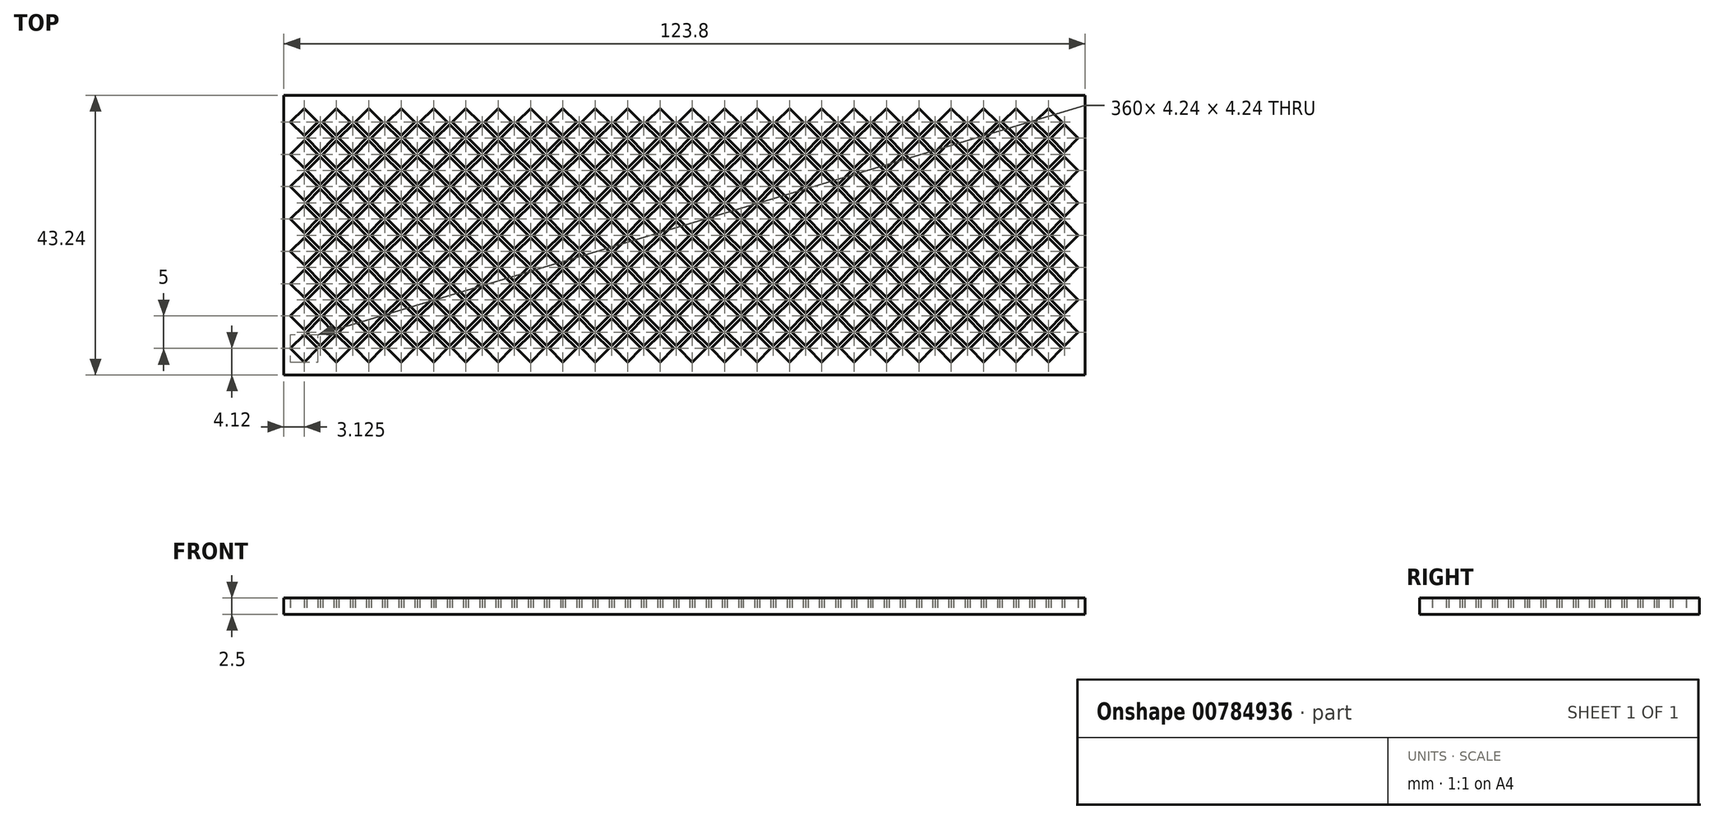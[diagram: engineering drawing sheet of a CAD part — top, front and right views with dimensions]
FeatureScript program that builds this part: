
annotation { "Feature Type Name" : "Feature", "Feature Type Description" : "" }
export const myFeature = defineFeature(function(context is Context, id is Id, definition is map)
    precondition{}
    {
        {
            var Q0;
            Q0=qCreatedBy(makeId("Top.planeOp"),FACE);
            var sketch = newSketch(context, id + "F0", { "sketchPlane" : qUnion([Q0])});
            skLineSegment(sketch, "E0.bottom", {"start": v(61.9, 21.62) * mm, "end": v(-61.9, 21.62) * mm});
            skLineSegment(sketch, "E0.top", {"start": v(61.9, -21.62) * mm, "end": v(-61.9, -21.62) * mm});
            skLineSegment(sketch, "E0.left", {"start": v(61.9, 21.62) * mm, "end": v(61.9, -21.62) * mm});
            skLineSegment(sketch, "E0.right", {"start": v(-61.9, 21.62) * mm, "end": v(-61.9, -21.62) * mm});
            skPoint(sketch, "E0.middle", {"position": v(0, 0) * mm});
            skLineSegment(sketch, "E1.bottom", {"start": v(-60.9, -17.5) * mm, "end": v(-58.77, -15.38) * mm});
            skLineSegment(sketch, "E1.top", {"start": v(-58.77, -19.62) * mm, "end": v(-56.65, -17.5) * mm});
            skLineSegment(sketch, "E1.left", {"start": v(-60.9, -17.5) * mm, "end": v(-58.77, -19.62) * mm});
            skLineSegment(sketch, "E1.right", {"start": v(-58.77, -15.38) * mm, "end": v(-56.65, -17.5) * mm});
            skLineSegment(sketch, "E2.0.1.0", {"start": v(-60.9, -12.5) * mm, "end": v(-58.77, -10.38) * mm});
            skLineSegment(sketch, "E2.0.1.1", {"start": v(-58.77, -14.62) * mm, "end": v(-56.65, -12.5) * mm});
            skLineSegment(sketch, "E2.0.1.2", {"start": v(-60.9, -12.5) * mm, "end": v(-58.77, -14.62) * mm});
            skLineSegment(sketch, "E2.0.1.3", {"start": v(-58.77, -10.38) * mm, "end": v(-56.65, -12.5) * mm});
            skLineSegment(sketch, "E2.0.2.0", {"start": v(-60.9, -7.5) * mm, "end": v(-58.77, -5.38) * mm});
            skLineSegment(sketch, "E2.0.2.1", {"start": v(-58.77, -9.62) * mm, "end": v(-56.65, -7.5) * mm});
            skLineSegment(sketch, "E2.0.2.2", {"start": v(-60.9, -7.5) * mm, "end": v(-58.77, -9.62) * mm});
            skLineSegment(sketch, "E2.0.2.3", {"start": v(-58.77, -5.38) * mm, "end": v(-56.65, -7.5) * mm});
            skLineSegment(sketch, "E2.0.3.0", {"start": v(-60.9, -2.5) * mm, "end": v(-58.77, -0.38) * mm});
            skLineSegment(sketch, "E2.0.3.1", {"start": v(-58.77, -4.62) * mm, "end": v(-56.65, -2.5) * mm});
            skLineSegment(sketch, "E2.0.3.2", {"start": v(-60.9, -2.5) * mm, "end": v(-58.77, -4.62) * mm});
            skLineSegment(sketch, "E2.0.3.3", {"start": v(-58.77, -0.38) * mm, "end": v(-56.65, -2.5) * mm});
            skLineSegment(sketch, "E2.0.4.0", {"start": v(-60.9, 2.5) * mm, "end": v(-58.77, 4.62) * mm});
            skLineSegment(sketch, "E2.0.4.1", {"start": v(-58.77, 0.38) * mm, "end": v(-56.65, 2.5) * mm});
            skLineSegment(sketch, "E2.0.4.2", {"start": v(-60.9, 2.5) * mm, "end": v(-58.77, 0.38) * mm});
            skLineSegment(sketch, "E2.0.4.3", {"start": v(-58.77, 4.62) * mm, "end": v(-56.65, 2.5) * mm});
            skLineSegment(sketch, "E2.0.5.0", {"start": v(-60.9, 7.5) * mm, "end": v(-58.77, 9.62) * mm});
            skLineSegment(sketch, "E2.0.5.1", {"start": v(-58.77, 5.38) * mm, "end": v(-56.65, 7.5) * mm});
            skLineSegment(sketch, "E2.0.5.2", {"start": v(-60.9, 7.5) * mm, "end": v(-58.77, 5.38) * mm});
            skLineSegment(sketch, "E2.0.5.3", {"start": v(-58.77, 9.62) * mm, "end": v(-56.65, 7.5) * mm});
            skLineSegment(sketch, "E2.0.6.0", {"start": v(-60.9, 12.5) * mm, "end": v(-58.77, 14.62) * mm});
            skLineSegment(sketch, "E2.0.6.1", {"start": v(-58.77, 10.38) * mm, "end": v(-56.65, 12.5) * mm});
            skLineSegment(sketch, "E2.0.6.2", {"start": v(-60.9, 12.5) * mm, "end": v(-58.77, 10.38) * mm});
            skLineSegment(sketch, "E2.0.6.3", {"start": v(-58.77, 14.62) * mm, "end": v(-56.65, 12.5) * mm});
            skLineSegment(sketch, "E2.0.7.0", {"start": v(-60.9, 17.5) * mm, "end": v(-58.77, 19.62) * mm});
            skLineSegment(sketch, "E2.0.7.1", {"start": v(-58.77, 15.38) * mm, "end": v(-56.65, 17.5) * mm});
            skLineSegment(sketch, "E2.0.7.2", {"start": v(-60.9, 17.5) * mm, "end": v(-58.77, 15.38) * mm});
            skLineSegment(sketch, "E2.0.7.3", {"start": v(-58.77, 19.62) * mm, "end": v(-56.65, 17.5) * mm});
            skLineSegment(sketch, "E2.1.0.0", {"start": v(-55.9, -17.5) * mm, "end": v(-53.77, -15.38) * mm});
            skLineSegment(sketch, "E2.1.0.1", {"start": v(-53.77, -19.62) * mm, "end": v(-51.65, -17.5) * mm});
            skLineSegment(sketch, "E2.1.0.2", {"start": v(-55.9, -17.5) * mm, "end": v(-53.77, -19.62) * mm});
            skLineSegment(sketch, "E2.1.0.3", {"start": v(-53.77, -15.38) * mm, "end": v(-51.65, -17.5) * mm});
            skLineSegment(sketch, "E2.1.1.0", {"start": v(-55.9, -12.5) * mm, "end": v(-53.77, -10.38) * mm});
            skLineSegment(sketch, "E2.1.1.1", {"start": v(-53.77, -14.62) * mm, "end": v(-51.65, -12.5) * mm});
            skLineSegment(sketch, "E2.1.1.2", {"start": v(-55.9, -12.5) * mm, "end": v(-53.77, -14.62) * mm});
            skLineSegment(sketch, "E2.1.1.3", {"start": v(-53.77, -10.38) * mm, "end": v(-51.65, -12.5) * mm});
            skLineSegment(sketch, "E2.1.2.0", {"start": v(-55.9, -7.5) * mm, "end": v(-53.77, -5.38) * mm});
            skLineSegment(sketch, "E2.1.2.1", {"start": v(-53.77, -9.62) * mm, "end": v(-51.65, -7.5) * mm});
            skLineSegment(sketch, "E2.1.2.2", {"start": v(-55.9, -7.5) * mm, "end": v(-53.77, -9.62) * mm});
            skLineSegment(sketch, "E2.1.2.3", {"start": v(-53.77, -5.38) * mm, "end": v(-51.65, -7.5) * mm});
            skLineSegment(sketch, "E2.1.3.0", {"start": v(-55.9, -2.5) * mm, "end": v(-53.77, -0.38) * mm});
            skLineSegment(sketch, "E2.1.3.1", {"start": v(-53.77, -4.62) * mm, "end": v(-51.65, -2.5) * mm});
            skLineSegment(sketch, "E2.1.3.2", {"start": v(-55.9, -2.5) * mm, "end": v(-53.77, -4.62) * mm});
            skLineSegment(sketch, "E2.1.3.3", {"start": v(-53.77, -0.38) * mm, "end": v(-51.65, -2.5) * mm});
            skLineSegment(sketch, "E2.1.4.0", {"start": v(-55.9, 2.5) * mm, "end": v(-53.77, 4.62) * mm});
            skLineSegment(sketch, "E2.1.4.1", {"start": v(-53.77, 0.38) * mm, "end": v(-51.65, 2.5) * mm});
            skLineSegment(sketch, "E2.1.4.2", {"start": v(-55.9, 2.5) * mm, "end": v(-53.77, 0.38) * mm});
            skLineSegment(sketch, "E2.1.4.3", {"start": v(-53.77, 4.62) * mm, "end": v(-51.65, 2.5) * mm});
            skLineSegment(sketch, "E2.1.5.0", {"start": v(-55.9, 7.5) * mm, "end": v(-53.77, 9.62) * mm});
            skLineSegment(sketch, "E2.1.5.1", {"start": v(-53.77, 5.38) * mm, "end": v(-51.65, 7.5) * mm});
            skLineSegment(sketch, "E2.1.5.2", {"start": v(-55.9, 7.5) * mm, "end": v(-53.77, 5.38) * mm});
            skLineSegment(sketch, "E2.1.5.3", {"start": v(-53.77, 9.62) * mm, "end": v(-51.65, 7.5) * mm});
            skLineSegment(sketch, "E2.1.6.0", {"start": v(-55.9, 12.5) * mm, "end": v(-53.77, 14.62) * mm});
            skLineSegment(sketch, "E2.1.6.1", {"start": v(-53.77, 10.38) * mm, "end": v(-51.65, 12.5) * mm});
            skLineSegment(sketch, "E2.1.6.2", {"start": v(-55.9, 12.5) * mm, "end": v(-53.77, 10.38) * mm});
            skLineSegment(sketch, "E2.1.6.3", {"start": v(-53.77, 14.62) * mm, "end": v(-51.65, 12.5) * mm});
            skLineSegment(sketch, "E2.1.7.0", {"start": v(-55.9, 17.5) * mm, "end": v(-53.77, 19.62) * mm});
            skLineSegment(sketch, "E2.1.7.1", {"start": v(-53.77, 15.38) * mm, "end": v(-51.65, 17.5) * mm});
            skLineSegment(sketch, "E2.1.7.2", {"start": v(-55.9, 17.5) * mm, "end": v(-53.77, 15.38) * mm});
            skLineSegment(sketch, "E2.1.7.3", {"start": v(-53.77, 19.62) * mm, "end": v(-51.65, 17.5) * mm});
            skLineSegment(sketch, "E2.2.0.0", {"start": v(-50.9, -17.5) * mm, "end": v(-48.77, -15.38) * mm});
            skLineSegment(sketch, "E2.2.0.1", {"start": v(-48.77, -19.62) * mm, "end": v(-46.65, -17.5) * mm});
            skLineSegment(sketch, "E2.2.0.2", {"start": v(-50.9, -17.5) * mm, "end": v(-48.77, -19.62) * mm});
            skLineSegment(sketch, "E2.2.0.3", {"start": v(-48.77, -15.38) * mm, "end": v(-46.65, -17.5) * mm});
            skLineSegment(sketch, "E2.2.1.0", {"start": v(-50.9, -12.5) * mm, "end": v(-48.77, -10.38) * mm});
            skLineSegment(sketch, "E2.2.1.1", {"start": v(-48.77, -14.62) * mm, "end": v(-46.65, -12.5) * mm});
            skLineSegment(sketch, "E2.2.1.2", {"start": v(-50.9, -12.5) * mm, "end": v(-48.77, -14.62) * mm});
            skLineSegment(sketch, "E2.2.1.3", {"start": v(-48.77, -10.38) * mm, "end": v(-46.65, -12.5) * mm});
            skLineSegment(sketch, "E2.2.2.0", {"start": v(-50.9, -7.5) * mm, "end": v(-48.77, -5.38) * mm});
            skLineSegment(sketch, "E2.2.2.1", {"start": v(-48.77, -9.62) * mm, "end": v(-46.65, -7.5) * mm});
            skLineSegment(sketch, "E2.2.2.2", {"start": v(-50.9, -7.5) * mm, "end": v(-48.77, -9.62) * mm});
            skLineSegment(sketch, "E2.2.2.3", {"start": v(-48.77, -5.38) * mm, "end": v(-46.65, -7.5) * mm});
            skLineSegment(sketch, "E2.2.3.0", {"start": v(-50.9, -2.5) * mm, "end": v(-48.77, -0.38) * mm});
            skLineSegment(sketch, "E2.2.3.1", {"start": v(-48.77, -4.62) * mm, "end": v(-46.65, -2.5) * mm});
            skLineSegment(sketch, "E2.2.3.2", {"start": v(-50.9, -2.5) * mm, "end": v(-48.77, -4.62) * mm});
            skLineSegment(sketch, "E2.2.3.3", {"start": v(-48.77, -0.38) * mm, "end": v(-46.65, -2.5) * mm});
            skLineSegment(sketch, "E2.2.4.0", {"start": v(-50.9, 2.5) * mm, "end": v(-48.77, 4.62) * mm});
            skLineSegment(sketch, "E2.2.4.1", {"start": v(-48.77, 0.38) * mm, "end": v(-46.65, 2.5) * mm});
            skLineSegment(sketch, "E2.2.4.2", {"start": v(-50.9, 2.5) * mm, "end": v(-48.77, 0.38) * mm});
            skLineSegment(sketch, "E2.2.4.3", {"start": v(-48.77, 4.62) * mm, "end": v(-46.65, 2.5) * mm});
            skLineSegment(sketch, "E2.2.5.0", {"start": v(-50.9, 7.5) * mm, "end": v(-48.77, 9.62) * mm});
            skLineSegment(sketch, "E2.2.5.1", {"start": v(-48.77, 5.38) * mm, "end": v(-46.65, 7.5) * mm});
            skLineSegment(sketch, "E2.2.5.2", {"start": v(-50.9, 7.5) * mm, "end": v(-48.77, 5.38) * mm});
            skLineSegment(sketch, "E2.2.5.3", {"start": v(-48.77, 9.62) * mm, "end": v(-46.65, 7.5) * mm});
            skLineSegment(sketch, "E2.2.6.0", {"start": v(-50.9, 12.5) * mm, "end": v(-48.77, 14.62) * mm});
            skLineSegment(sketch, "E2.2.6.1", {"start": v(-48.77, 10.38) * mm, "end": v(-46.65, 12.5) * mm});
            skLineSegment(sketch, "E2.2.6.2", {"start": v(-50.9, 12.5) * mm, "end": v(-48.77, 10.38) * mm});
            skLineSegment(sketch, "E2.2.6.3", {"start": v(-48.77, 14.62) * mm, "end": v(-46.65, 12.5) * mm});
            skLineSegment(sketch, "E2.2.7.0", {"start": v(-50.9, 17.5) * mm, "end": v(-48.77, 19.62) * mm});
            skLineSegment(sketch, "E2.2.7.1", {"start": v(-48.77, 15.38) * mm, "end": v(-46.65, 17.5) * mm});
            skLineSegment(sketch, "E2.2.7.2", {"start": v(-50.9, 17.5) * mm, "end": v(-48.77, 15.38) * mm});
            skLineSegment(sketch, "E2.2.7.3", {"start": v(-48.77, 19.62) * mm, "end": v(-46.65, 17.5) * mm});
            skLineSegment(sketch, "E2.3.0.0", {"start": v(-45.9, -17.5) * mm, "end": v(-43.77, -15.38) * mm});
            skLineSegment(sketch, "E2.3.0.1", {"start": v(-43.77, -19.62) * mm, "end": v(-41.65, -17.5) * mm});
            skLineSegment(sketch, "E2.3.0.2", {"start": v(-45.9, -17.5) * mm, "end": v(-43.77, -19.62) * mm});
            skLineSegment(sketch, "E2.3.0.3", {"start": v(-43.77, -15.38) * mm, "end": v(-41.65, -17.5) * mm});
            skLineSegment(sketch, "E2.3.1.0", {"start": v(-45.9, -12.5) * mm, "end": v(-43.77, -10.38) * mm});
            skLineSegment(sketch, "E2.3.1.1", {"start": v(-43.77, -14.62) * mm, "end": v(-41.65, -12.5) * mm});
            skLineSegment(sketch, "E2.3.1.2", {"start": v(-45.9, -12.5) * mm, "end": v(-43.77, -14.62) * mm});
            skLineSegment(sketch, "E2.3.1.3", {"start": v(-43.77, -10.38) * mm, "end": v(-41.65, -12.5) * mm});
            skLineSegment(sketch, "E2.3.2.0", {"start": v(-45.9, -7.5) * mm, "end": v(-43.77, -5.38) * mm});
            skLineSegment(sketch, "E2.3.2.1", {"start": v(-43.77, -9.62) * mm, "end": v(-41.65, -7.5) * mm});
            skLineSegment(sketch, "E2.3.2.2", {"start": v(-45.9, -7.5) * mm, "end": v(-43.77, -9.62) * mm});
            skLineSegment(sketch, "E2.3.2.3", {"start": v(-43.77, -5.38) * mm, "end": v(-41.65, -7.5) * mm});
            skLineSegment(sketch, "E2.3.3.0", {"start": v(-45.9, -2.5) * mm, "end": v(-43.77, -0.38) * mm});
            skLineSegment(sketch, "E2.3.3.1", {"start": v(-43.77, -4.62) * mm, "end": v(-41.65, -2.5) * mm});
            skLineSegment(sketch, "E2.3.3.2", {"start": v(-45.9, -2.5) * mm, "end": v(-43.77, -4.62) * mm});
            skLineSegment(sketch, "E2.3.3.3", {"start": v(-43.77, -0.38) * mm, "end": v(-41.65, -2.5) * mm});
            skLineSegment(sketch, "E2.3.4.0", {"start": v(-45.9, 2.5) * mm, "end": v(-43.77, 4.62) * mm});
            skLineSegment(sketch, "E2.3.4.1", {"start": v(-43.77, 0.38) * mm, "end": v(-41.65, 2.5) * mm});
            skLineSegment(sketch, "E2.3.4.2", {"start": v(-45.9, 2.5) * mm, "end": v(-43.77, 0.38) * mm});
            skLineSegment(sketch, "E2.3.4.3", {"start": v(-43.77, 4.62) * mm, "end": v(-41.65, 2.5) * mm});
            skLineSegment(sketch, "E2.3.5.0", {"start": v(-45.9, 7.5) * mm, "end": v(-43.77, 9.62) * mm});
            skLineSegment(sketch, "E2.3.5.1", {"start": v(-43.77, 5.38) * mm, "end": v(-41.65, 7.5) * mm});
            skLineSegment(sketch, "E2.3.5.2", {"start": v(-45.9, 7.5) * mm, "end": v(-43.77, 5.38) * mm});
            skLineSegment(sketch, "E2.3.5.3", {"start": v(-43.77, 9.62) * mm, "end": v(-41.65, 7.5) * mm});
            skLineSegment(sketch, "E2.3.6.0", {"start": v(-45.9, 12.5) * mm, "end": v(-43.77, 14.62) * mm});
            skLineSegment(sketch, "E2.3.6.1", {"start": v(-43.77, 10.38) * mm, "end": v(-41.65, 12.5) * mm});
            skLineSegment(sketch, "E2.3.6.2", {"start": v(-45.9, 12.5) * mm, "end": v(-43.77, 10.38) * mm});
            skLineSegment(sketch, "E2.3.6.3", {"start": v(-43.77, 14.62) * mm, "end": v(-41.65, 12.5) * mm});
            skLineSegment(sketch, "E2.3.7.0", {"start": v(-45.9, 17.5) * mm, "end": v(-43.77, 19.62) * mm});
            skLineSegment(sketch, "E2.3.7.1", {"start": v(-43.77, 15.38) * mm, "end": v(-41.65, 17.5) * mm});
            skLineSegment(sketch, "E2.3.7.2", {"start": v(-45.9, 17.5) * mm, "end": v(-43.77, 15.38) * mm});
            skLineSegment(sketch, "E2.3.7.3", {"start": v(-43.77, 19.62) * mm, "end": v(-41.65, 17.5) * mm});
            skLineSegment(sketch, "E2.4.0.0", {"start": v(-40.9, -17.5) * mm, "end": v(-38.77, -15.38) * mm});
            skLineSegment(sketch, "E2.4.0.1", {"start": v(-38.77, -19.62) * mm, "end": v(-36.65, -17.5) * mm});
            skLineSegment(sketch, "E2.4.0.2", {"start": v(-40.9, -17.5) * mm, "end": v(-38.77, -19.62) * mm});
            skLineSegment(sketch, "E2.4.0.3", {"start": v(-38.77, -15.38) * mm, "end": v(-36.65, -17.5) * mm});
            skLineSegment(sketch, "E2.4.1.0", {"start": v(-40.9, -12.5) * mm, "end": v(-38.77, -10.38) * mm});
            skLineSegment(sketch, "E2.4.1.1", {"start": v(-38.77, -14.62) * mm, "end": v(-36.65, -12.5) * mm});
            skLineSegment(sketch, "E2.4.1.2", {"start": v(-40.9, -12.5) * mm, "end": v(-38.77, -14.62) * mm});
            skLineSegment(sketch, "E2.4.1.3", {"start": v(-38.77, -10.38) * mm, "end": v(-36.65, -12.5) * mm});
            skLineSegment(sketch, "E2.4.2.0", {"start": v(-40.9, -7.5) * mm, "end": v(-38.77, -5.38) * mm});
            skLineSegment(sketch, "E2.4.2.1", {"start": v(-38.77, -9.62) * mm, "end": v(-36.65, -7.5) * mm});
            skLineSegment(sketch, "E2.4.2.2", {"start": v(-40.9, -7.5) * mm, "end": v(-38.77, -9.62) * mm});
            skLineSegment(sketch, "E2.4.2.3", {"start": v(-38.77, -5.38) * mm, "end": v(-36.65, -7.5) * mm});
            skLineSegment(sketch, "E2.4.3.0", {"start": v(-40.9, -2.5) * mm, "end": v(-38.77, -0.38) * mm});
            skLineSegment(sketch, "E2.4.3.1", {"start": v(-38.77, -4.62) * mm, "end": v(-36.65, -2.5) * mm});
            skLineSegment(sketch, "E2.4.3.2", {"start": v(-40.9, -2.5) * mm, "end": v(-38.77, -4.62) * mm});
            skLineSegment(sketch, "E2.4.3.3", {"start": v(-38.77, -0.38) * mm, "end": v(-36.65, -2.5) * mm});
            skLineSegment(sketch, "E2.4.4.0", {"start": v(-40.9, 2.5) * mm, "end": v(-38.77, 4.62) * mm});
            skLineSegment(sketch, "E2.4.4.1", {"start": v(-38.77, 0.38) * mm, "end": v(-36.65, 2.5) * mm});
            skLineSegment(sketch, "E2.4.4.2", {"start": v(-40.9, 2.5) * mm, "end": v(-38.77, 0.38) * mm});
            skLineSegment(sketch, "E2.4.4.3", {"start": v(-38.77, 4.62) * mm, "end": v(-36.65, 2.5) * mm});
            skLineSegment(sketch, "E2.4.5.0", {"start": v(-40.9, 7.5) * mm, "end": v(-38.77, 9.62) * mm});
            skLineSegment(sketch, "E2.4.5.1", {"start": v(-38.77, 5.38) * mm, "end": v(-36.65, 7.5) * mm});
            skLineSegment(sketch, "E2.4.5.2", {"start": v(-40.9, 7.5) * mm, "end": v(-38.77, 5.38) * mm});
            skLineSegment(sketch, "E2.4.5.3", {"start": v(-38.77, 9.62) * mm, "end": v(-36.65, 7.5) * mm});
            skLineSegment(sketch, "E2.4.6.0", {"start": v(-40.9, 12.5) * mm, "end": v(-38.77, 14.62) * mm});
            skLineSegment(sketch, "E2.4.6.1", {"start": v(-38.77, 10.38) * mm, "end": v(-36.65, 12.5) * mm});
            skLineSegment(sketch, "E2.4.6.2", {"start": v(-40.9, 12.5) * mm, "end": v(-38.77, 10.38) * mm});
            skLineSegment(sketch, "E2.4.6.3", {"start": v(-38.77, 14.62) * mm, "end": v(-36.65, 12.5) * mm});
            skLineSegment(sketch, "E2.4.7.0", {"start": v(-40.9, 17.5) * mm, "end": v(-38.77, 19.62) * mm});
            skLineSegment(sketch, "E2.4.7.1", {"start": v(-38.77, 15.38) * mm, "end": v(-36.65, 17.5) * mm});
            skLineSegment(sketch, "E2.4.7.2", {"start": v(-40.9, 17.5) * mm, "end": v(-38.77, 15.38) * mm});
            skLineSegment(sketch, "E2.4.7.3", {"start": v(-38.77, 19.62) * mm, "end": v(-36.65, 17.5) * mm});
            skLineSegment(sketch, "E2.5.0.0", {"start": v(-35.9, -17.5) * mm, "end": v(-33.77, -15.38) * mm});
            skLineSegment(sketch, "E2.5.0.1", {"start": v(-33.77, -19.62) * mm, "end": v(-31.65, -17.5) * mm});
            skLineSegment(sketch, "E2.5.0.2", {"start": v(-35.9, -17.5) * mm, "end": v(-33.77, -19.62) * mm});
            skLineSegment(sketch, "E2.5.0.3", {"start": v(-33.77, -15.38) * mm, "end": v(-31.65, -17.5) * mm});
            skLineSegment(sketch, "E2.5.1.0", {"start": v(-35.9, -12.5) * mm, "end": v(-33.77, -10.38) * mm});
            skLineSegment(sketch, "E2.5.1.1", {"start": v(-33.77, -14.62) * mm, "end": v(-31.65, -12.5) * mm});
            skLineSegment(sketch, "E2.5.1.2", {"start": v(-35.9, -12.5) * mm, "end": v(-33.77, -14.62) * mm});
            skLineSegment(sketch, "E2.5.1.3", {"start": v(-33.77, -10.38) * mm, "end": v(-31.65, -12.5) * mm});
            skLineSegment(sketch, "E2.5.2.0", {"start": v(-35.9, -7.5) * mm, "end": v(-33.77, -5.38) * mm});
            skLineSegment(sketch, "E2.5.2.1", {"start": v(-33.77, -9.62) * mm, "end": v(-31.65, -7.5) * mm});
            skLineSegment(sketch, "E2.5.2.2", {"start": v(-35.9, -7.5) * mm, "end": v(-33.77, -9.62) * mm});
            skLineSegment(sketch, "E2.5.2.3", {"start": v(-33.77, -5.38) * mm, "end": v(-31.65, -7.5) * mm});
            skLineSegment(sketch, "E2.5.3.0", {"start": v(-35.9, -2.5) * mm, "end": v(-33.77, -0.38) * mm});
            skLineSegment(sketch, "E2.5.3.1", {"start": v(-33.77, -4.62) * mm, "end": v(-31.65, -2.5) * mm});
            skLineSegment(sketch, "E2.5.3.2", {"start": v(-35.9, -2.5) * mm, "end": v(-33.77, -4.62) * mm});
            skLineSegment(sketch, "E2.5.3.3", {"start": v(-33.77, -0.38) * mm, "end": v(-31.65, -2.5) * mm});
            skLineSegment(sketch, "E2.5.4.0", {"start": v(-35.9, 2.5) * mm, "end": v(-33.77, 4.62) * mm});
            skLineSegment(sketch, "E2.5.4.1", {"start": v(-33.77, 0.38) * mm, "end": v(-31.65, 2.5) * mm});
            skLineSegment(sketch, "E2.5.4.2", {"start": v(-35.9, 2.5) * mm, "end": v(-33.77, 0.38) * mm});
            skLineSegment(sketch, "E2.5.4.3", {"start": v(-33.77, 4.62) * mm, "end": v(-31.65, 2.5) * mm});
            skLineSegment(sketch, "E2.5.5.0", {"start": v(-35.9, 7.5) * mm, "end": v(-33.77, 9.62) * mm});
            skLineSegment(sketch, "E2.5.5.1", {"start": v(-33.77, 5.38) * mm, "end": v(-31.65, 7.5) * mm});
            skLineSegment(sketch, "E2.5.5.2", {"start": v(-35.9, 7.5) * mm, "end": v(-33.77, 5.38) * mm});
            skLineSegment(sketch, "E2.5.5.3", {"start": v(-33.77, 9.62) * mm, "end": v(-31.65, 7.5) * mm});
            skLineSegment(sketch, "E2.5.6.0", {"start": v(-35.9, 12.5) * mm, "end": v(-33.77, 14.62) * mm});
            skLineSegment(sketch, "E2.5.6.1", {"start": v(-33.77, 10.38) * mm, "end": v(-31.65, 12.5) * mm});
            skLineSegment(sketch, "E2.5.6.2", {"start": v(-35.9, 12.5) * mm, "end": v(-33.77, 10.38) * mm});
            skLineSegment(sketch, "E2.5.6.3", {"start": v(-33.77, 14.62) * mm, "end": v(-31.65, 12.5) * mm});
            skLineSegment(sketch, "E2.5.7.0", {"start": v(-35.9, 17.5) * mm, "end": v(-33.77, 19.62) * mm});
            skLineSegment(sketch, "E2.5.7.1", {"start": v(-33.77, 15.38) * mm, "end": v(-31.65, 17.5) * mm});
            skLineSegment(sketch, "E2.5.7.2", {"start": v(-35.9, 17.5) * mm, "end": v(-33.77, 15.38) * mm});
            skLineSegment(sketch, "E2.5.7.3", {"start": v(-33.77, 19.62) * mm, "end": v(-31.65, 17.5) * mm});
            skLineSegment(sketch, "E2.6.0.0", {"start": v(-30.9, -17.5) * mm, "end": v(-28.77, -15.38) * mm});
            skLineSegment(sketch, "E2.6.0.1", {"start": v(-28.77, -19.62) * mm, "end": v(-26.65, -17.5) * mm});
            skLineSegment(sketch, "E2.6.0.2", {"start": v(-30.9, -17.5) * mm, "end": v(-28.77, -19.62) * mm});
            skLineSegment(sketch, "E2.6.0.3", {"start": v(-28.77, -15.38) * mm, "end": v(-26.65, -17.5) * mm});
            skLineSegment(sketch, "E2.6.1.0", {"start": v(-30.9, -12.5) * mm, "end": v(-28.77, -10.38) * mm});
            skLineSegment(sketch, "E2.6.1.1", {"start": v(-28.77, -14.62) * mm, "end": v(-26.65, -12.5) * mm});
            skLineSegment(sketch, "E2.6.1.2", {"start": v(-30.9, -12.5) * mm, "end": v(-28.77, -14.62) * mm});
            skLineSegment(sketch, "E2.6.1.3", {"start": v(-28.77, -10.38) * mm, "end": v(-26.65, -12.5) * mm});
            skLineSegment(sketch, "E2.6.2.0", {"start": v(-30.9, -7.5) * mm, "end": v(-28.77, -5.38) * mm});
            skLineSegment(sketch, "E2.6.2.1", {"start": v(-28.77, -9.62) * mm, "end": v(-26.65, -7.5) * mm});
            skLineSegment(sketch, "E2.6.2.2", {"start": v(-30.9, -7.5) * mm, "end": v(-28.77, -9.62) * mm});
            skLineSegment(sketch, "E2.6.2.3", {"start": v(-28.77, -5.38) * mm, "end": v(-26.65, -7.5) * mm});
            skLineSegment(sketch, "E2.6.3.0", {"start": v(-30.9, -2.5) * mm, "end": v(-28.77, -0.38) * mm});
            skLineSegment(sketch, "E2.6.3.1", {"start": v(-28.77, -4.62) * mm, "end": v(-26.65, -2.5) * mm});
            skLineSegment(sketch, "E2.6.3.2", {"start": v(-30.9, -2.5) * mm, "end": v(-28.77, -4.62) * mm});
            skLineSegment(sketch, "E2.6.3.3", {"start": v(-28.77, -0.38) * mm, "end": v(-26.65, -2.5) * mm});
            skLineSegment(sketch, "E2.6.4.0", {"start": v(-30.9, 2.5) * mm, "end": v(-28.77, 4.62) * mm});
            skLineSegment(sketch, "E2.6.4.1", {"start": v(-28.77, 0.38) * mm, "end": v(-26.65, 2.5) * mm});
            skLineSegment(sketch, "E2.6.4.2", {"start": v(-30.9, 2.5) * mm, "end": v(-28.77, 0.38) * mm});
            skLineSegment(sketch, "E2.6.4.3", {"start": v(-28.77, 4.62) * mm, "end": v(-26.65, 2.5) * mm});
            skLineSegment(sketch, "E2.6.5.0", {"start": v(-30.9, 7.5) * mm, "end": v(-28.77, 9.62) * mm});
            skLineSegment(sketch, "E2.6.5.1", {"start": v(-28.77, 5.38) * mm, "end": v(-26.65, 7.5) * mm});
            skLineSegment(sketch, "E2.6.5.2", {"start": v(-30.9, 7.5) * mm, "end": v(-28.77, 5.38) * mm});
            skLineSegment(sketch, "E2.6.5.3", {"start": v(-28.77, 9.62) * mm, "end": v(-26.65, 7.5) * mm});
            skLineSegment(sketch, "E2.6.6.0", {"start": v(-30.9, 12.5) * mm, "end": v(-28.77, 14.62) * mm});
            skLineSegment(sketch, "E2.6.6.1", {"start": v(-28.77, 10.38) * mm, "end": v(-26.65, 12.5) * mm});
            skLineSegment(sketch, "E2.6.6.2", {"start": v(-30.9, 12.5) * mm, "end": v(-28.77, 10.38) * mm});
            skLineSegment(sketch, "E2.6.6.3", {"start": v(-28.77, 14.62) * mm, "end": v(-26.65, 12.5) * mm});
            skLineSegment(sketch, "E2.6.7.0", {"start": v(-30.9, 17.5) * mm, "end": v(-28.77, 19.62) * mm});
            skLineSegment(sketch, "E2.6.7.1", {"start": v(-28.77, 15.38) * mm, "end": v(-26.65, 17.5) * mm});
            skLineSegment(sketch, "E2.6.7.2", {"start": v(-30.9, 17.5) * mm, "end": v(-28.77, 15.38) * mm});
            skLineSegment(sketch, "E2.6.7.3", {"start": v(-28.77, 19.62) * mm, "end": v(-26.65, 17.5) * mm});
            skLineSegment(sketch, "E2.7.0.0", {"start": v(-25.9, -17.5) * mm, "end": v(-23.77, -15.38) * mm});
            skLineSegment(sketch, "E2.7.0.1", {"start": v(-23.77, -19.62) * mm, "end": v(-21.65, -17.5) * mm});
            skLineSegment(sketch, "E2.7.0.2", {"start": v(-25.9, -17.5) * mm, "end": v(-23.77, -19.62) * mm});
            skLineSegment(sketch, "E2.7.0.3", {"start": v(-23.77, -15.38) * mm, "end": v(-21.65, -17.5) * mm});
            skLineSegment(sketch, "E2.7.1.0", {"start": v(-25.9, -12.5) * mm, "end": v(-23.77, -10.38) * mm});
            skLineSegment(sketch, "E2.7.1.1", {"start": v(-23.77, -14.62) * mm, "end": v(-21.65, -12.5) * mm});
            skLineSegment(sketch, "E2.7.1.2", {"start": v(-25.9, -12.5) * mm, "end": v(-23.77, -14.62) * mm});
            skLineSegment(sketch, "E2.7.1.3", {"start": v(-23.77, -10.38) * mm, "end": v(-21.65, -12.5) * mm});
            skLineSegment(sketch, "E2.7.2.0", {"start": v(-25.9, -7.5) * mm, "end": v(-23.77, -5.38) * mm});
            skLineSegment(sketch, "E2.7.2.1", {"start": v(-23.77, -9.62) * mm, "end": v(-21.65, -7.5) * mm});
            skLineSegment(sketch, "E2.7.2.2", {"start": v(-25.9, -7.5) * mm, "end": v(-23.77, -9.62) * mm});
            skLineSegment(sketch, "E2.7.2.3", {"start": v(-23.77, -5.38) * mm, "end": v(-21.65, -7.5) * mm});
            skLineSegment(sketch, "E2.7.3.0", {"start": v(-25.9, -2.5) * mm, "end": v(-23.77, -0.38) * mm});
            skLineSegment(sketch, "E2.7.3.1", {"start": v(-23.77, -4.62) * mm, "end": v(-21.65, -2.5) * mm});
            skLineSegment(sketch, "E2.7.3.2", {"start": v(-25.9, -2.5) * mm, "end": v(-23.77, -4.62) * mm});
            skLineSegment(sketch, "E2.7.3.3", {"start": v(-23.77, -0.38) * mm, "end": v(-21.65, -2.5) * mm});
            skLineSegment(sketch, "E2.7.4.0", {"start": v(-25.9, 2.5) * mm, "end": v(-23.77, 4.62) * mm});
            skLineSegment(sketch, "E2.7.4.1", {"start": v(-23.77, 0.38) * mm, "end": v(-21.65, 2.5) * mm});
            skLineSegment(sketch, "E2.7.4.2", {"start": v(-25.9, 2.5) * mm, "end": v(-23.77, 0.38) * mm});
            skLineSegment(sketch, "E2.7.4.3", {"start": v(-23.77, 4.62) * mm, "end": v(-21.65, 2.5) * mm});
            skLineSegment(sketch, "E2.7.5.0", {"start": v(-25.9, 7.5) * mm, "end": v(-23.77, 9.62) * mm});
            skLineSegment(sketch, "E2.7.5.1", {"start": v(-23.77, 5.38) * mm, "end": v(-21.65, 7.5) * mm});
            skLineSegment(sketch, "E2.7.5.2", {"start": v(-25.9, 7.5) * mm, "end": v(-23.77, 5.38) * mm});
            skLineSegment(sketch, "E2.7.5.3", {"start": v(-23.77, 9.62) * mm, "end": v(-21.65, 7.5) * mm});
            skLineSegment(sketch, "E2.7.6.0", {"start": v(-25.9, 12.5) * mm, "end": v(-23.77, 14.62) * mm});
            skLineSegment(sketch, "E2.7.6.1", {"start": v(-23.77, 10.38) * mm, "end": v(-21.65, 12.5) * mm});
            skLineSegment(sketch, "E2.7.6.2", {"start": v(-25.9, 12.5) * mm, "end": v(-23.77, 10.38) * mm});
            skLineSegment(sketch, "E2.7.6.3", {"start": v(-23.77, 14.62) * mm, "end": v(-21.65, 12.5) * mm});
            skLineSegment(sketch, "E2.7.7.0", {"start": v(-25.9, 17.5) * mm, "end": v(-23.77, 19.62) * mm});
            skLineSegment(sketch, "E2.7.7.1", {"start": v(-23.77, 15.38) * mm, "end": v(-21.65, 17.5) * mm});
            skLineSegment(sketch, "E2.7.7.2", {"start": v(-25.9, 17.5) * mm, "end": v(-23.77, 15.38) * mm});
            skLineSegment(sketch, "E2.7.7.3", {"start": v(-23.77, 19.62) * mm, "end": v(-21.65, 17.5) * mm});
            skLineSegment(sketch, "E2.direction1", {"start": v(-58.77, -19.62) * mm, "end": v(-53.77, -19.62) * mm, "construction": true});
            skLineSegment(sketch, "E2.direction2", {"start": v(-58.77, -19.62) * mm, "end": v(-58.77, -14.62) * mm, "construction": true});
            skLineSegment(sketch, "E3", {"start": v(-56.27, -12.88) * mm, "end": v(-54.15, -15) * mm});
            skLineSegment(sketch, "E4", {"start": v(-58.4, -15) * mm, "end": v(-56.27, -17.12) * mm});
            skLineSegment(sketch, "E5", {"start": v(-58.4, -15) * mm, "end": v(-56.27, -12.88) * mm});
            skLineSegment(sketch, "E6", {"start": v(-56.27, -17.12) * mm, "end": v(-54.15, -15) * mm});
            skLineSegment(sketch, "E7.0.1.0", {"start": v(-58.4, -10) * mm, "end": v(-56.27, -7.88) * mm});
            skLineSegment(sketch, "E7.0.1.1", {"start": v(-56.27, -7.88) * mm, "end": v(-54.15, -10) * mm});
            skLineSegment(sketch, "E7.0.1.2", {"start": v(-56.27, -12.12) * mm, "end": v(-54.15, -10) * mm});
            skLineSegment(sketch, "E7.0.1.3", {"start": v(-58.4, -10) * mm, "end": v(-56.27, -12.12) * mm});
            skLineSegment(sketch, "E7.0.2.0", {"start": v(-58.4, -5) * mm, "end": v(-56.27, -2.88) * mm});
            skLineSegment(sketch, "E7.0.2.1", {"start": v(-56.27, -2.88) * mm, "end": v(-54.15, -5) * mm});
            skLineSegment(sketch, "E7.0.2.2", {"start": v(-56.27, -7.12) * mm, "end": v(-54.15, -5) * mm});
            skLineSegment(sketch, "E7.0.2.3", {"start": v(-58.4, -5) * mm, "end": v(-56.27, -7.12) * mm});
            skLineSegment(sketch, "E7.0.3.0", {"start": v(-58.4, 0) * mm, "end": v(-56.27, 2.12) * mm});
            skLineSegment(sketch, "E7.0.3.1", {"start": v(-56.27, 2.12) * mm, "end": v(-54.15, 0) * mm});
            skLineSegment(sketch, "E7.0.3.2", {"start": v(-56.27, -2.12) * mm, "end": v(-54.15, 0) * mm});
            skLineSegment(sketch, "E7.0.3.3", {"start": v(-58.4, 0) * mm, "end": v(-56.27, -2.12) * mm});
            skLineSegment(sketch, "E7.0.4.0", {"start": v(-58.4, 5) * mm, "end": v(-56.27, 7.12) * mm});
            skLineSegment(sketch, "E7.0.4.1", {"start": v(-56.27, 7.12) * mm, "end": v(-54.15, 5) * mm});
            skLineSegment(sketch, "E7.0.4.2", {"start": v(-56.27, 2.88) * mm, "end": v(-54.15, 5) * mm});
            skLineSegment(sketch, "E7.0.4.3", {"start": v(-58.4, 5) * mm, "end": v(-56.27, 2.88) * mm});
            skLineSegment(sketch, "E7.0.5.0", {"start": v(-58.4, 10) * mm, "end": v(-56.27, 12.12) * mm});
            skLineSegment(sketch, "E7.0.5.1", {"start": v(-56.27, 12.12) * mm, "end": v(-54.15, 10) * mm});
            skLineSegment(sketch, "E7.0.5.2", {"start": v(-56.27, 7.88) * mm, "end": v(-54.15, 10) * mm});
            skLineSegment(sketch, "E7.0.5.3", {"start": v(-58.4, 10) * mm, "end": v(-56.27, 7.88) * mm});
            skLineSegment(sketch, "E7.0.6.0", {"start": v(-58.4, 15) * mm, "end": v(-56.27, 17.12) * mm});
            skLineSegment(sketch, "E7.0.6.1", {"start": v(-56.27, 17.12) * mm, "end": v(-54.15, 15) * mm});
            skLineSegment(sketch, "E7.0.6.2", {"start": v(-56.27, 12.88) * mm, "end": v(-54.15, 15) * mm});
            skLineSegment(sketch, "E7.0.6.3", {"start": v(-58.4, 15) * mm, "end": v(-56.27, 12.88) * mm});
            skLineSegment(sketch, "E7.1.0.0", {"start": v(-53.4, -15) * mm, "end": v(-51.27, -12.88) * mm});
            skLineSegment(sketch, "E7.1.0.1", {"start": v(-51.27, -12.88) * mm, "end": v(-49.15, -15) * mm});
            skLineSegment(sketch, "E7.1.0.2", {"start": v(-51.27, -17.12) * mm, "end": v(-49.15, -15) * mm});
            skLineSegment(sketch, "E7.1.0.3", {"start": v(-53.4, -15) * mm, "end": v(-51.27, -17.12) * mm});
            skLineSegment(sketch, "E7.1.1.0", {"start": v(-53.4, -10) * mm, "end": v(-51.27, -7.88) * mm});
            skLineSegment(sketch, "E7.1.1.1", {"start": v(-51.27, -7.88) * mm, "end": v(-49.15, -10) * mm});
            skLineSegment(sketch, "E7.1.1.2", {"start": v(-51.27, -12.12) * mm, "end": v(-49.15, -10) * mm});
            skLineSegment(sketch, "E7.1.1.3", {"start": v(-53.4, -10) * mm, "end": v(-51.27, -12.12) * mm});
            skLineSegment(sketch, "E7.1.2.0", {"start": v(-53.4, -5) * mm, "end": v(-51.27, -2.88) * mm});
            skLineSegment(sketch, "E7.1.2.1", {"start": v(-51.27, -2.88) * mm, "end": v(-49.15, -5) * mm});
            skLineSegment(sketch, "E7.1.2.2", {"start": v(-51.27, -7.12) * mm, "end": v(-49.15, -5) * mm});
            skLineSegment(sketch, "E7.1.2.3", {"start": v(-53.4, -5) * mm, "end": v(-51.27, -7.12) * mm});
            skLineSegment(sketch, "E7.1.3.0", {"start": v(-53.4, 0) * mm, "end": v(-51.27, 2.12) * mm});
            skLineSegment(sketch, "E7.1.3.1", {"start": v(-51.27, 2.12) * mm, "end": v(-49.15, 0) * mm});
            skLineSegment(sketch, "E7.1.3.2", {"start": v(-51.27, -2.12) * mm, "end": v(-49.15, 0) * mm});
            skLineSegment(sketch, "E7.1.3.3", {"start": v(-53.4, 0) * mm, "end": v(-51.27, -2.12) * mm});
            skLineSegment(sketch, "E7.1.4.0", {"start": v(-53.4, 5) * mm, "end": v(-51.27, 7.12) * mm});
            skLineSegment(sketch, "E7.1.4.1", {"start": v(-51.27, 7.12) * mm, "end": v(-49.15, 5) * mm});
            skLineSegment(sketch, "E7.1.4.2", {"start": v(-51.27, 2.88) * mm, "end": v(-49.15, 5) * mm});
            skLineSegment(sketch, "E7.1.4.3", {"start": v(-53.4, 5) * mm, "end": v(-51.27, 2.88) * mm});
            skLineSegment(sketch, "E7.1.5.0", {"start": v(-53.4, 10) * mm, "end": v(-51.27, 12.12) * mm});
            skLineSegment(sketch, "E7.1.5.1", {"start": v(-51.27, 12.12) * mm, "end": v(-49.15, 10) * mm});
            skLineSegment(sketch, "E7.1.5.2", {"start": v(-51.27, 7.88) * mm, "end": v(-49.15, 10) * mm});
            skLineSegment(sketch, "E7.1.5.3", {"start": v(-53.4, 10) * mm, "end": v(-51.27, 7.88) * mm});
            skLineSegment(sketch, "E7.1.6.0", {"start": v(-53.4, 15) * mm, "end": v(-51.27, 17.12) * mm});
            skLineSegment(sketch, "E7.1.6.1", {"start": v(-51.27, 17.12) * mm, "end": v(-49.15, 15) * mm});
            skLineSegment(sketch, "E7.1.6.2", {"start": v(-51.27, 12.88) * mm, "end": v(-49.15, 15) * mm});
            skLineSegment(sketch, "E7.1.6.3", {"start": v(-53.4, 15) * mm, "end": v(-51.27, 12.88) * mm});
            skLineSegment(sketch, "E7.2.0.0", {"start": v(-48.4, -15) * mm, "end": v(-46.27, -12.88) * mm});
            skLineSegment(sketch, "E7.2.0.1", {"start": v(-46.27, -12.88) * mm, "end": v(-44.15, -15) * mm});
            skLineSegment(sketch, "E7.2.0.2", {"start": v(-46.27, -17.12) * mm, "end": v(-44.15, -15) * mm});
            skLineSegment(sketch, "E7.2.0.3", {"start": v(-48.4, -15) * mm, "end": v(-46.27, -17.12) * mm});
            skLineSegment(sketch, "E7.2.1.0", {"start": v(-48.4, -10) * mm, "end": v(-46.27, -7.88) * mm});
            skLineSegment(sketch, "E7.2.1.1", {"start": v(-46.27, -7.88) * mm, "end": v(-44.15, -10) * mm});
            skLineSegment(sketch, "E7.2.1.2", {"start": v(-46.27, -12.12) * mm, "end": v(-44.15, -10) * mm});
            skLineSegment(sketch, "E7.2.1.3", {"start": v(-48.4, -10) * mm, "end": v(-46.27, -12.12) * mm});
            skLineSegment(sketch, "E7.2.2.0", {"start": v(-48.4, -5) * mm, "end": v(-46.27, -2.88) * mm});
            skLineSegment(sketch, "E7.2.2.1", {"start": v(-46.27, -2.88) * mm, "end": v(-44.15, -5) * mm});
            skLineSegment(sketch, "E7.2.2.2", {"start": v(-46.27, -7.12) * mm, "end": v(-44.15, -5) * mm});
            skLineSegment(sketch, "E7.2.2.3", {"start": v(-48.4, -5) * mm, "end": v(-46.27, -7.12) * mm});
            skLineSegment(sketch, "E7.2.3.0", {"start": v(-48.4, 0) * mm, "end": v(-46.27, 2.12) * mm});
            skLineSegment(sketch, "E7.2.3.1", {"start": v(-46.27, 2.12) * mm, "end": v(-44.15, 0) * mm});
            skLineSegment(sketch, "E7.2.3.2", {"start": v(-46.27, -2.12) * mm, "end": v(-44.15, 0) * mm});
            skLineSegment(sketch, "E7.2.3.3", {"start": v(-48.4, 0) * mm, "end": v(-46.27, -2.12) * mm});
            skLineSegment(sketch, "E7.2.4.0", {"start": v(-48.4, 5) * mm, "end": v(-46.27, 7.12) * mm});
            skLineSegment(sketch, "E7.2.4.1", {"start": v(-46.27, 7.12) * mm, "end": v(-44.15, 5) * mm});
            skLineSegment(sketch, "E7.2.4.2", {"start": v(-46.27, 2.88) * mm, "end": v(-44.15, 5) * mm});
            skLineSegment(sketch, "E7.2.4.3", {"start": v(-48.4, 5) * mm, "end": v(-46.27, 2.88) * mm});
            skLineSegment(sketch, "E7.2.5.0", {"start": v(-48.4, 10) * mm, "end": v(-46.27, 12.12) * mm});
            skLineSegment(sketch, "E7.2.5.1", {"start": v(-46.27, 12.12) * mm, "end": v(-44.15, 10) * mm});
            skLineSegment(sketch, "E7.2.5.2", {"start": v(-46.27, 7.88) * mm, "end": v(-44.15, 10) * mm});
            skLineSegment(sketch, "E7.2.5.3", {"start": v(-48.4, 10) * mm, "end": v(-46.27, 7.88) * mm});
            skLineSegment(sketch, "E7.2.6.0", {"start": v(-48.4, 15) * mm, "end": v(-46.27, 17.12) * mm});
            skLineSegment(sketch, "E7.2.6.1", {"start": v(-46.27, 17.12) * mm, "end": v(-44.15, 15) * mm});
            skLineSegment(sketch, "E7.2.6.2", {"start": v(-46.27, 12.88) * mm, "end": v(-44.15, 15) * mm});
            skLineSegment(sketch, "E7.2.6.3", {"start": v(-48.4, 15) * mm, "end": v(-46.27, 12.88) * mm});
            skLineSegment(sketch, "E7.3.0.0", {"start": v(-43.4, -15) * mm, "end": v(-41.27, -12.88) * mm});
            skLineSegment(sketch, "E7.3.0.1", {"start": v(-41.27, -12.88) * mm, "end": v(-39.15, -15) * mm});
            skLineSegment(sketch, "E7.3.0.2", {"start": v(-41.27, -17.12) * mm, "end": v(-39.15, -15) * mm});
            skLineSegment(sketch, "E7.3.0.3", {"start": v(-43.4, -15) * mm, "end": v(-41.27, -17.12) * mm});
            skLineSegment(sketch, "E7.3.1.0", {"start": v(-43.4, -10) * mm, "end": v(-41.27, -7.88) * mm});
            skLineSegment(sketch, "E7.3.1.1", {"start": v(-41.27, -7.88) * mm, "end": v(-39.15, -10) * mm});
            skLineSegment(sketch, "E7.3.1.2", {"start": v(-41.27, -12.12) * mm, "end": v(-39.15, -10) * mm});
            skLineSegment(sketch, "E7.3.1.3", {"start": v(-43.4, -10) * mm, "end": v(-41.27, -12.12) * mm});
            skLineSegment(sketch, "E7.3.2.0", {"start": v(-43.4, -5) * mm, "end": v(-41.27, -2.88) * mm});
            skLineSegment(sketch, "E7.3.2.1", {"start": v(-41.27, -2.88) * mm, "end": v(-39.15, -5) * mm});
            skLineSegment(sketch, "E7.3.2.2", {"start": v(-41.27, -7.12) * mm, "end": v(-39.15, -5) * mm});
            skLineSegment(sketch, "E7.3.2.3", {"start": v(-43.4, -5) * mm, "end": v(-41.27, -7.12) * mm});
            skLineSegment(sketch, "E7.3.3.0", {"start": v(-43.4, 0) * mm, "end": v(-41.27, 2.12) * mm});
            skLineSegment(sketch, "E7.3.3.1", {"start": v(-41.27, 2.12) * mm, "end": v(-39.15, 0) * mm});
            skLineSegment(sketch, "E7.3.3.2", {"start": v(-41.27, -2.12) * mm, "end": v(-39.15, 0) * mm});
            skLineSegment(sketch, "E7.3.3.3", {"start": v(-43.4, 0) * mm, "end": v(-41.27, -2.12) * mm});
            skLineSegment(sketch, "E7.3.4.0", {"start": v(-43.4, 5) * mm, "end": v(-41.27, 7.12) * mm});
            skLineSegment(sketch, "E7.3.4.1", {"start": v(-41.27, 7.12) * mm, "end": v(-39.15, 5) * mm});
            skLineSegment(sketch, "E7.3.4.2", {"start": v(-41.27, 2.88) * mm, "end": v(-39.15, 5) * mm});
            skLineSegment(sketch, "E7.3.4.3", {"start": v(-43.4, 5) * mm, "end": v(-41.27, 2.88) * mm});
            skLineSegment(sketch, "E7.3.5.0", {"start": v(-43.4, 10) * mm, "end": v(-41.27, 12.12) * mm});
            skLineSegment(sketch, "E7.3.5.1", {"start": v(-41.27, 12.12) * mm, "end": v(-39.15, 10) * mm});
            skLineSegment(sketch, "E7.3.5.2", {"start": v(-41.27, 7.88) * mm, "end": v(-39.15, 10) * mm});
            skLineSegment(sketch, "E7.3.5.3", {"start": v(-43.4, 10) * mm, "end": v(-41.27, 7.88) * mm});
            skLineSegment(sketch, "E7.3.6.0", {"start": v(-43.4, 15) * mm, "end": v(-41.27, 17.12) * mm});
            skLineSegment(sketch, "E7.3.6.1", {"start": v(-41.27, 17.12) * mm, "end": v(-39.15, 15) * mm});
            skLineSegment(sketch, "E7.3.6.2", {"start": v(-41.27, 12.88) * mm, "end": v(-39.15, 15) * mm});
            skLineSegment(sketch, "E7.3.6.3", {"start": v(-43.4, 15) * mm, "end": v(-41.27, 12.88) * mm});
            skLineSegment(sketch, "E7.4.0.0", {"start": v(-38.4, -15) * mm, "end": v(-36.27, -12.88) * mm});
            skLineSegment(sketch, "E7.4.0.1", {"start": v(-36.27, -12.88) * mm, "end": v(-34.15, -15) * mm});
            skLineSegment(sketch, "E7.4.0.2", {"start": v(-36.27, -17.12) * mm, "end": v(-34.15, -15) * mm});
            skLineSegment(sketch, "E7.4.0.3", {"start": v(-38.4, -15) * mm, "end": v(-36.27, -17.12) * mm});
            skLineSegment(sketch, "E7.4.1.0", {"start": v(-38.4, -10) * mm, "end": v(-36.27, -7.88) * mm});
            skLineSegment(sketch, "E7.4.1.1", {"start": v(-36.27, -7.88) * mm, "end": v(-34.15, -10) * mm});
            skLineSegment(sketch, "E7.4.1.2", {"start": v(-36.27, -12.12) * mm, "end": v(-34.15, -10) * mm});
            skLineSegment(sketch, "E7.4.1.3", {"start": v(-38.4, -10) * mm, "end": v(-36.27, -12.12) * mm});
            skLineSegment(sketch, "E7.4.2.0", {"start": v(-38.4, -5) * mm, "end": v(-36.27, -2.88) * mm});
            skLineSegment(sketch, "E7.4.2.1", {"start": v(-36.27, -2.88) * mm, "end": v(-34.15, -5) * mm});
            skLineSegment(sketch, "E7.4.2.2", {"start": v(-36.27, -7.12) * mm, "end": v(-34.15, -5) * mm});
            skLineSegment(sketch, "E7.4.2.3", {"start": v(-38.4, -5) * mm, "end": v(-36.27, -7.12) * mm});
            skLineSegment(sketch, "E7.4.3.0", {"start": v(-38.4, 0) * mm, "end": v(-36.27, 2.12) * mm});
            skLineSegment(sketch, "E7.4.3.1", {"start": v(-36.27, 2.12) * mm, "end": v(-34.15, 0) * mm});
            skLineSegment(sketch, "E7.4.3.2", {"start": v(-36.27, -2.12) * mm, "end": v(-34.15, 0) * mm});
            skLineSegment(sketch, "E7.4.3.3", {"start": v(-38.4, 0) * mm, "end": v(-36.27, -2.12) * mm});
            skLineSegment(sketch, "E7.4.4.0", {"start": v(-38.4, 5) * mm, "end": v(-36.27, 7.12) * mm});
            skLineSegment(sketch, "E7.4.4.1", {"start": v(-36.27, 7.12) * mm, "end": v(-34.15, 5) * mm});
            skLineSegment(sketch, "E7.4.4.2", {"start": v(-36.27, 2.88) * mm, "end": v(-34.15, 5) * mm});
            skLineSegment(sketch, "E7.4.4.3", {"start": v(-38.4, 5) * mm, "end": v(-36.27, 2.88) * mm});
            skLineSegment(sketch, "E7.4.5.0", {"start": v(-38.4, 10) * mm, "end": v(-36.27, 12.12) * mm});
            skLineSegment(sketch, "E7.4.5.1", {"start": v(-36.27, 12.12) * mm, "end": v(-34.15, 10) * mm});
            skLineSegment(sketch, "E7.4.5.2", {"start": v(-36.27, 7.88) * mm, "end": v(-34.15, 10) * mm});
            skLineSegment(sketch, "E7.4.5.3", {"start": v(-38.4, 10) * mm, "end": v(-36.27, 7.88) * mm});
            skLineSegment(sketch, "E7.4.6.0", {"start": v(-38.4, 15) * mm, "end": v(-36.27, 17.12) * mm});
            skLineSegment(sketch, "E7.4.6.1", {"start": v(-36.27, 17.12) * mm, "end": v(-34.15, 15) * mm});
            skLineSegment(sketch, "E7.4.6.2", {"start": v(-36.27, 12.88) * mm, "end": v(-34.15, 15) * mm});
            skLineSegment(sketch, "E7.4.6.3", {"start": v(-38.4, 15) * mm, "end": v(-36.27, 12.88) * mm});
            skLineSegment(sketch, "E7.5.0.0", {"start": v(-33.4, -15) * mm, "end": v(-31.27, -12.88) * mm});
            skLineSegment(sketch, "E7.5.0.1", {"start": v(-31.27, -12.88) * mm, "end": v(-29.15, -15) * mm});
            skLineSegment(sketch, "E7.5.0.2", {"start": v(-31.27, -17.12) * mm, "end": v(-29.15, -15) * mm});
            skLineSegment(sketch, "E7.5.0.3", {"start": v(-33.4, -15) * mm, "end": v(-31.27, -17.12) * mm});
            skLineSegment(sketch, "E7.5.1.0", {"start": v(-33.4, -10) * mm, "end": v(-31.27, -7.88) * mm});
            skLineSegment(sketch, "E7.5.1.1", {"start": v(-31.27, -7.88) * mm, "end": v(-29.15, -10) * mm});
            skLineSegment(sketch, "E7.5.1.2", {"start": v(-31.27, -12.12) * mm, "end": v(-29.15, -10) * mm});
            skLineSegment(sketch, "E7.5.1.3", {"start": v(-33.4, -10) * mm, "end": v(-31.27, -12.12) * mm});
            skLineSegment(sketch, "E7.5.2.0", {"start": v(-33.4, -5) * mm, "end": v(-31.27, -2.88) * mm});
            skLineSegment(sketch, "E7.5.2.1", {"start": v(-31.27, -2.88) * mm, "end": v(-29.15, -5) * mm});
            skLineSegment(sketch, "E7.5.2.2", {"start": v(-31.27, -7.12) * mm, "end": v(-29.15, -5) * mm});
            skLineSegment(sketch, "E7.5.2.3", {"start": v(-33.4, -5) * mm, "end": v(-31.27, -7.12) * mm});
            skLineSegment(sketch, "E7.5.3.0", {"start": v(-33.4, 0) * mm, "end": v(-31.27, 2.12) * mm});
            skLineSegment(sketch, "E7.5.3.1", {"start": v(-31.27, 2.12) * mm, "end": v(-29.15, 0) * mm});
            skLineSegment(sketch, "E7.5.3.2", {"start": v(-31.27, -2.12) * mm, "end": v(-29.15, 0) * mm});
            skLineSegment(sketch, "E7.5.3.3", {"start": v(-33.4, 0) * mm, "end": v(-31.27, -2.12) * mm});
            skLineSegment(sketch, "E7.5.4.0", {"start": v(-33.4, 5) * mm, "end": v(-31.27, 7.12) * mm});
            skLineSegment(sketch, "E7.5.4.1", {"start": v(-31.27, 7.12) * mm, "end": v(-29.15, 5) * mm});
            skLineSegment(sketch, "E7.5.4.2", {"start": v(-31.27, 2.88) * mm, "end": v(-29.15, 5) * mm});
            skLineSegment(sketch, "E7.5.4.3", {"start": v(-33.4, 5) * mm, "end": v(-31.27, 2.88) * mm});
            skLineSegment(sketch, "E7.5.5.0", {"start": v(-33.4, 10) * mm, "end": v(-31.27, 12.12) * mm});
            skLineSegment(sketch, "E7.5.5.1", {"start": v(-31.27, 12.12) * mm, "end": v(-29.15, 10) * mm});
            skLineSegment(sketch, "E7.5.5.2", {"start": v(-31.27, 7.88) * mm, "end": v(-29.15, 10) * mm});
            skLineSegment(sketch, "E7.5.5.3", {"start": v(-33.4, 10) * mm, "end": v(-31.27, 7.88) * mm});
            skLineSegment(sketch, "E7.5.6.0", {"start": v(-33.4, 15) * mm, "end": v(-31.27, 17.12) * mm});
            skLineSegment(sketch, "E7.5.6.1", {"start": v(-31.27, 17.12) * mm, "end": v(-29.15, 15) * mm});
            skLineSegment(sketch, "E7.5.6.2", {"start": v(-31.27, 12.88) * mm, "end": v(-29.15, 15) * mm});
            skLineSegment(sketch, "E7.5.6.3", {"start": v(-33.4, 15) * mm, "end": v(-31.27, 12.88) * mm});
            skLineSegment(sketch, "E7.6.0.0", {"start": v(-28.4, -15) * mm, "end": v(-26.27, -12.88) * mm});
            skLineSegment(sketch, "E7.6.0.1", {"start": v(-26.27, -12.88) * mm, "end": v(-24.15, -15) * mm});
            skLineSegment(sketch, "E7.6.0.2", {"start": v(-26.27, -17.12) * mm, "end": v(-24.15, -15) * mm});
            skLineSegment(sketch, "E7.6.0.3", {"start": v(-28.4, -15) * mm, "end": v(-26.27, -17.12) * mm});
            skLineSegment(sketch, "E7.6.1.0", {"start": v(-28.4, -10) * mm, "end": v(-26.27, -7.88) * mm});
            skLineSegment(sketch, "E7.6.1.1", {"start": v(-26.27, -7.88) * mm, "end": v(-24.15, -10) * mm});
            skLineSegment(sketch, "E7.6.1.2", {"start": v(-26.27, -12.12) * mm, "end": v(-24.15, -10) * mm});
            skLineSegment(sketch, "E7.6.1.3", {"start": v(-28.4, -10) * mm, "end": v(-26.27, -12.12) * mm});
            skLineSegment(sketch, "E7.6.2.0", {"start": v(-28.4, -5) * mm, "end": v(-26.27, -2.88) * mm});
            skLineSegment(sketch, "E7.6.2.1", {"start": v(-26.27, -2.88) * mm, "end": v(-24.15, -5) * mm});
            skLineSegment(sketch, "E7.6.2.2", {"start": v(-26.27, -7.12) * mm, "end": v(-24.15, -5) * mm});
            skLineSegment(sketch, "E7.6.2.3", {"start": v(-28.4, -5) * mm, "end": v(-26.27, -7.12) * mm});
            skLineSegment(sketch, "E7.6.3.0", {"start": v(-28.4, 0) * mm, "end": v(-26.27, 2.12) * mm});
            skLineSegment(sketch, "E7.6.3.1", {"start": v(-26.27, 2.12) * mm, "end": v(-24.15, 0) * mm});
            skLineSegment(sketch, "E7.6.3.2", {"start": v(-26.27, -2.12) * mm, "end": v(-24.15, 0) * mm});
            skLineSegment(sketch, "E7.6.3.3", {"start": v(-28.4, 0) * mm, "end": v(-26.27, -2.12) * mm});
            skLineSegment(sketch, "E7.6.4.0", {"start": v(-28.4, 5) * mm, "end": v(-26.27, 7.12) * mm});
            skLineSegment(sketch, "E7.6.4.1", {"start": v(-26.27, 7.12) * mm, "end": v(-24.15, 5) * mm});
            skLineSegment(sketch, "E7.6.4.2", {"start": v(-26.27, 2.88) * mm, "end": v(-24.15, 5) * mm});
            skLineSegment(sketch, "E7.6.4.3", {"start": v(-28.4, 5) * mm, "end": v(-26.27, 2.88) * mm});
            skLineSegment(sketch, "E7.6.5.0", {"start": v(-28.4, 10) * mm, "end": v(-26.27, 12.12) * mm});
            skLineSegment(sketch, "E7.6.5.1", {"start": v(-26.27, 12.12) * mm, "end": v(-24.15, 10) * mm});
            skLineSegment(sketch, "E7.6.5.2", {"start": v(-26.27, 7.88) * mm, "end": v(-24.15, 10) * mm});
            skLineSegment(sketch, "E7.6.5.3", {"start": v(-28.4, 10) * mm, "end": v(-26.27, 7.88) * mm});
            skLineSegment(sketch, "E7.6.6.0", {"start": v(-28.4, 15) * mm, "end": v(-26.27, 17.12) * mm});
            skLineSegment(sketch, "E7.6.6.1", {"start": v(-26.27, 17.12) * mm, "end": v(-24.15, 15) * mm});
            skLineSegment(sketch, "E7.6.6.2", {"start": v(-26.27, 12.88) * mm, "end": v(-24.15, 15) * mm});
            skLineSegment(sketch, "E7.6.6.3", {"start": v(-28.4, 15) * mm, "end": v(-26.27, 12.88) * mm});
            skLineSegment(sketch, "E7.direction1", {"start": v(-58.4, -15) * mm, "end": v(-53.4, -15) * mm, "construction": true});
            skLineSegment(sketch, "E7.direction2", {"start": v(-58.4, -15) * mm, "end": v(-58.4, -10) * mm, "construction": true});
            skLineSegment(sketch, "E8.0.8.0", {"start": v(-20.9, -17.5) * mm, "end": v(-18.77, -15.38) * mm});
            skLineSegment(sketch, "E8.3.8.0", {"start": v(-18.77, -19.62) * mm, "end": v(-16.65, -17.5) * mm});
            skLineSegment(sketch, "E8.6.8.0", {"start": v(-20.9, -17.5) * mm, "end": v(-18.77, -19.62) * mm});
            skLineSegment(sketch, "E8.9.8.0", {"start": v(-18.77, -15.38) * mm, "end": v(-16.65, -17.5) * mm});
            skLineSegment(sketch, "E8.0.8.1", {"start": v(-20.9, -12.5) * mm, "end": v(-18.77, -10.38) * mm});
            skLineSegment(sketch, "E8.3.8.1", {"start": v(-18.77, -14.62) * mm, "end": v(-16.65, -12.5) * mm});
            skLineSegment(sketch, "E8.6.8.1", {"start": v(-20.9, -12.5) * mm, "end": v(-18.77, -14.62) * mm});
            skLineSegment(sketch, "E8.9.8.1", {"start": v(-18.77, -10.38) * mm, "end": v(-16.65, -12.5) * mm});
            skLineSegment(sketch, "E8.0.8.2", {"start": v(-20.9, -7.5) * mm, "end": v(-18.77, -5.38) * mm});
            skLineSegment(sketch, "E8.3.8.2", {"start": v(-18.77, -9.62) * mm, "end": v(-16.65, -7.5) * mm});
            skLineSegment(sketch, "E8.6.8.2", {"start": v(-20.9, -7.5) * mm, "end": v(-18.77, -9.62) * mm});
            skLineSegment(sketch, "E8.9.8.2", {"start": v(-18.77, -5.38) * mm, "end": v(-16.65, -7.5) * mm});
            skLineSegment(sketch, "E8.0.8.3", {"start": v(-20.9, -2.5) * mm, "end": v(-18.77, -0.38) * mm});
            skLineSegment(sketch, "E8.3.8.3", {"start": v(-18.77, -4.62) * mm, "end": v(-16.65, -2.5) * mm});
            skLineSegment(sketch, "E8.6.8.3", {"start": v(-20.9, -2.5) * mm, "end": v(-18.77, -4.62) * mm});
            skLineSegment(sketch, "E8.9.8.3", {"start": v(-18.77, -0.38) * mm, "end": v(-16.65, -2.5) * mm});
            skLineSegment(sketch, "E8.0.8.4", {"start": v(-20.9, 2.5) * mm, "end": v(-18.77, 4.62) * mm});
            skLineSegment(sketch, "E8.3.8.4", {"start": v(-18.77, 0.38) * mm, "end": v(-16.65, 2.5) * mm});
            skLineSegment(sketch, "E8.6.8.4", {"start": v(-20.9, 2.5) * mm, "end": v(-18.77, 0.38) * mm});
            skLineSegment(sketch, "E8.9.8.4", {"start": v(-18.77, 4.62) * mm, "end": v(-16.65, 2.5) * mm});
            skLineSegment(sketch, "E8.0.8.5", {"start": v(-20.9, 7.5) * mm, "end": v(-18.77, 9.62) * mm});
            skLineSegment(sketch, "E8.3.8.5", {"start": v(-18.77, 5.38) * mm, "end": v(-16.65, 7.5) * mm});
            skLineSegment(sketch, "E8.6.8.5", {"start": v(-20.9, 7.5) * mm, "end": v(-18.77, 5.38) * mm});
            skLineSegment(sketch, "E8.9.8.5", {"start": v(-18.77, 9.62) * mm, "end": v(-16.65, 7.5) * mm});
            skLineSegment(sketch, "E8.0.8.6", {"start": v(-20.9, 12.5) * mm, "end": v(-18.77, 14.62) * mm});
            skLineSegment(sketch, "E8.3.8.6", {"start": v(-18.77, 10.38) * mm, "end": v(-16.65, 12.5) * mm});
            skLineSegment(sketch, "E8.6.8.6", {"start": v(-20.9, 12.5) * mm, "end": v(-18.77, 10.38) * mm});
            skLineSegment(sketch, "E8.9.8.6", {"start": v(-18.77, 14.62) * mm, "end": v(-16.65, 12.5) * mm});
            skLineSegment(sketch, "E8.0.8.7", {"start": v(-20.9, 17.5) * mm, "end": v(-18.77, 19.62) * mm});
            skLineSegment(sketch, "E8.3.8.7", {"start": v(-18.77, 15.38) * mm, "end": v(-16.65, 17.5) * mm});
            skLineSegment(sketch, "E8.6.8.7", {"start": v(-20.9, 17.5) * mm, "end": v(-18.77, 15.38) * mm});
            skLineSegment(sketch, "E8.9.8.7", {"start": v(-18.77, 19.62) * mm, "end": v(-16.65, 17.5) * mm});
            skLineSegment(sketch, "E8.0.9.0", {"start": v(-15.9, -17.5) * mm, "end": v(-13.77, -15.38) * mm});
            skLineSegment(sketch, "E8.3.9.0", {"start": v(-13.77, -19.62) * mm, "end": v(-11.65, -17.5) * mm});
            skLineSegment(sketch, "E8.6.9.0", {"start": v(-15.9, -17.5) * mm, "end": v(-13.77, -19.62) * mm});
            skLineSegment(sketch, "E8.9.9.0", {"start": v(-13.77, -15.38) * mm, "end": v(-11.65, -17.5) * mm});
            skLineSegment(sketch, "E8.0.9.1", {"start": v(-15.9, -12.5) * mm, "end": v(-13.77, -10.38) * mm});
            skLineSegment(sketch, "E8.3.9.1", {"start": v(-13.77, -14.62) * mm, "end": v(-11.65, -12.5) * mm});
            skLineSegment(sketch, "E8.6.9.1", {"start": v(-15.9, -12.5) * mm, "end": v(-13.77, -14.62) * mm});
            skLineSegment(sketch, "E8.9.9.1", {"start": v(-13.77, -10.38) * mm, "end": v(-11.65, -12.5) * mm});
            skLineSegment(sketch, "E8.0.9.2", {"start": v(-15.9, -7.5) * mm, "end": v(-13.77, -5.38) * mm});
            skLineSegment(sketch, "E8.3.9.2", {"start": v(-13.77, -9.62) * mm, "end": v(-11.65, -7.5) * mm});
            skLineSegment(sketch, "E8.6.9.2", {"start": v(-15.9, -7.5) * mm, "end": v(-13.77, -9.62) * mm});
            skLineSegment(sketch, "E8.9.9.2", {"start": v(-13.77, -5.38) * mm, "end": v(-11.65, -7.5) * mm});
            skLineSegment(sketch, "E8.0.9.3", {"start": v(-15.9, -2.5) * mm, "end": v(-13.77, -0.38) * mm});
            skLineSegment(sketch, "E8.3.9.3", {"start": v(-13.77, -4.62) * mm, "end": v(-11.65, -2.5) * mm});
            skLineSegment(sketch, "E8.6.9.3", {"start": v(-15.9, -2.5) * mm, "end": v(-13.77, -4.62) * mm});
            skLineSegment(sketch, "E8.9.9.3", {"start": v(-13.77, -0.38) * mm, "end": v(-11.65, -2.5) * mm});
            skLineSegment(sketch, "E8.0.9.4", {"start": v(-15.9, 2.5) * mm, "end": v(-13.77, 4.62) * mm});
            skLineSegment(sketch, "E8.3.9.4", {"start": v(-13.77, 0.38) * mm, "end": v(-11.65, 2.5) * mm});
            skLineSegment(sketch, "E8.6.9.4", {"start": v(-15.9, 2.5) * mm, "end": v(-13.77, 0.38) * mm});
            skLineSegment(sketch, "E8.9.9.4", {"start": v(-13.77, 4.62) * mm, "end": v(-11.65, 2.5) * mm});
            skLineSegment(sketch, "E8.0.9.5", {"start": v(-15.9, 7.5) * mm, "end": v(-13.77, 9.62) * mm});
            skLineSegment(sketch, "E8.3.9.5", {"start": v(-13.77, 5.38) * mm, "end": v(-11.65, 7.5) * mm});
            skLineSegment(sketch, "E8.6.9.5", {"start": v(-15.9, 7.5) * mm, "end": v(-13.77, 5.38) * mm});
            skLineSegment(sketch, "E8.9.9.5", {"start": v(-13.77, 9.62) * mm, "end": v(-11.65, 7.5) * mm});
            skLineSegment(sketch, "E8.0.9.6", {"start": v(-15.9, 12.5) * mm, "end": v(-13.77, 14.62) * mm});
            skLineSegment(sketch, "E8.3.9.6", {"start": v(-13.77, 10.38) * mm, "end": v(-11.65, 12.5) * mm});
            skLineSegment(sketch, "E8.6.9.6", {"start": v(-15.9, 12.5) * mm, "end": v(-13.77, 10.38) * mm});
            skLineSegment(sketch, "E8.9.9.6", {"start": v(-13.77, 14.62) * mm, "end": v(-11.65, 12.5) * mm});
            skLineSegment(sketch, "E8.0.9.7", {"start": v(-15.9, 17.5) * mm, "end": v(-13.77, 19.62) * mm});
            skLineSegment(sketch, "E8.3.9.7", {"start": v(-13.77, 15.38) * mm, "end": v(-11.65, 17.5) * mm});
            skLineSegment(sketch, "E8.6.9.7", {"start": v(-15.9, 17.5) * mm, "end": v(-13.77, 15.38) * mm});
            skLineSegment(sketch, "E8.9.9.7", {"start": v(-13.77, 19.62) * mm, "end": v(-11.65, 17.5) * mm});
            skLineSegment(sketch, "E8.0.10.0", {"start": v(-10.9, -17.5) * mm, "end": v(-8.77, -15.38) * mm});
            skLineSegment(sketch, "E8.3.10.0", {"start": v(-8.77, -19.62) * mm, "end": v(-6.65, -17.5) * mm});
            skLineSegment(sketch, "E8.6.10.0", {"start": v(-10.9, -17.5) * mm, "end": v(-8.77, -19.62) * mm});
            skLineSegment(sketch, "E8.9.10.0", {"start": v(-8.77, -15.38) * mm, "end": v(-6.65, -17.5) * mm});
            skLineSegment(sketch, "E8.0.10.1", {"start": v(-10.9, -12.5) * mm, "end": v(-8.77, -10.38) * mm});
            skLineSegment(sketch, "E8.3.10.1", {"start": v(-8.77, -14.62) * mm, "end": v(-6.65, -12.5) * mm});
            skLineSegment(sketch, "E8.6.10.1", {"start": v(-10.9, -12.5) * mm, "end": v(-8.77, -14.62) * mm});
            skLineSegment(sketch, "E8.9.10.1", {"start": v(-8.77, -10.38) * mm, "end": v(-6.65, -12.5) * mm});
            skLineSegment(sketch, "E8.0.10.2", {"start": v(-10.9, -7.5) * mm, "end": v(-8.77, -5.38) * mm});
            skLineSegment(sketch, "E8.3.10.2", {"start": v(-8.77, -9.62) * mm, "end": v(-6.65, -7.5) * mm});
            skLineSegment(sketch, "E8.6.10.2", {"start": v(-10.9, -7.5) * mm, "end": v(-8.77, -9.62) * mm});
            skLineSegment(sketch, "E8.9.10.2", {"start": v(-8.77, -5.38) * mm, "end": v(-6.65, -7.5) * mm});
            skLineSegment(sketch, "E8.0.10.3", {"start": v(-10.9, -2.5) * mm, "end": v(-8.77, -0.38) * mm});
            skLineSegment(sketch, "E8.3.10.3", {"start": v(-8.77, -4.62) * mm, "end": v(-6.65, -2.5) * mm});
            skLineSegment(sketch, "E8.6.10.3", {"start": v(-10.9, -2.5) * mm, "end": v(-8.77, -4.62) * mm});
            skLineSegment(sketch, "E8.9.10.3", {"start": v(-8.77, -0.38) * mm, "end": v(-6.65, -2.5) * mm});
            skLineSegment(sketch, "E8.0.10.4", {"start": v(-10.9, 2.5) * mm, "end": v(-8.77, 4.62) * mm});
            skLineSegment(sketch, "E8.3.10.4", {"start": v(-8.77, 0.38) * mm, "end": v(-6.65, 2.5) * mm});
            skLineSegment(sketch, "E8.6.10.4", {"start": v(-10.9, 2.5) * mm, "end": v(-8.77, 0.38) * mm});
            skLineSegment(sketch, "E8.9.10.4", {"start": v(-8.77, 4.62) * mm, "end": v(-6.65, 2.5) * mm});
            skLineSegment(sketch, "E8.0.10.5", {"start": v(-10.9, 7.5) * mm, "end": v(-8.77, 9.62) * mm});
            skLineSegment(sketch, "E8.3.10.5", {"start": v(-8.77, 5.38) * mm, "end": v(-6.65, 7.5) * mm});
            skLineSegment(sketch, "E8.6.10.5", {"start": v(-10.9, 7.5) * mm, "end": v(-8.77, 5.38) * mm});
            skLineSegment(sketch, "E8.9.10.5", {"start": v(-8.77, 9.62) * mm, "end": v(-6.65, 7.5) * mm});
            skLineSegment(sketch, "E8.0.10.6", {"start": v(-10.9, 12.5) * mm, "end": v(-8.77, 14.62) * mm});
            skLineSegment(sketch, "E8.3.10.6", {"start": v(-8.77, 10.38) * mm, "end": v(-6.65, 12.5) * mm});
            skLineSegment(sketch, "E8.6.10.6", {"start": v(-10.9, 12.5) * mm, "end": v(-8.77, 10.38) * mm});
            skLineSegment(sketch, "E8.9.10.6", {"start": v(-8.77, 14.62) * mm, "end": v(-6.65, 12.5) * mm});
            skLineSegment(sketch, "E8.0.10.7", {"start": v(-10.9, 17.5) * mm, "end": v(-8.77, 19.62) * mm});
            skLineSegment(sketch, "E8.3.10.7", {"start": v(-8.77, 15.38) * mm, "end": v(-6.65, 17.5) * mm});
            skLineSegment(sketch, "E8.6.10.7", {"start": v(-10.9, 17.5) * mm, "end": v(-8.77, 15.38) * mm});
            skLineSegment(sketch, "E8.9.10.7", {"start": v(-8.77, 19.62) * mm, "end": v(-6.65, 17.5) * mm});
            skLineSegment(sketch, "E8.0.11.0", {"start": v(-5.9, -17.5) * mm, "end": v(-3.77, -15.38) * mm});
            skLineSegment(sketch, "E8.3.11.0", {"start": v(-3.77, -19.62) * mm, "end": v(-1.65, -17.5) * mm});
            skLineSegment(sketch, "E8.6.11.0", {"start": v(-5.9, -17.5) * mm, "end": v(-3.77, -19.62) * mm});
            skLineSegment(sketch, "E8.9.11.0", {"start": v(-3.77, -15.38) * mm, "end": v(-1.65, -17.5) * mm});
            skLineSegment(sketch, "E8.0.11.1", {"start": v(-5.9, -12.5) * mm, "end": v(-3.77, -10.38) * mm});
            skLineSegment(sketch, "E8.3.11.1", {"start": v(-3.77, -14.62) * mm, "end": v(-1.65, -12.5) * mm});
            skLineSegment(sketch, "E8.6.11.1", {"start": v(-5.9, -12.5) * mm, "end": v(-3.77, -14.62) * mm});
            skLineSegment(sketch, "E8.9.11.1", {"start": v(-3.77, -10.38) * mm, "end": v(-1.65, -12.5) * mm});
            skLineSegment(sketch, "E8.0.11.2", {"start": v(-5.9, -7.5) * mm, "end": v(-3.77, -5.38) * mm});
            skLineSegment(sketch, "E8.3.11.2", {"start": v(-3.77, -9.62) * mm, "end": v(-1.65, -7.5) * mm});
            skLineSegment(sketch, "E8.6.11.2", {"start": v(-5.9, -7.5) * mm, "end": v(-3.77, -9.62) * mm});
            skLineSegment(sketch, "E8.9.11.2", {"start": v(-3.77, -5.38) * mm, "end": v(-1.65, -7.5) * mm});
            skLineSegment(sketch, "E8.0.11.3", {"start": v(-5.9, -2.5) * mm, "end": v(-3.77, -0.38) * mm});
            skLineSegment(sketch, "E8.3.11.3", {"start": v(-3.77, -4.62) * mm, "end": v(-1.65, -2.5) * mm});
            skLineSegment(sketch, "E8.6.11.3", {"start": v(-5.9, -2.5) * mm, "end": v(-3.77, -4.62) * mm});
            skLineSegment(sketch, "E8.9.11.3", {"start": v(-3.77, -0.38) * mm, "end": v(-1.65, -2.5) * mm});
            skLineSegment(sketch, "E8.0.11.4", {"start": v(-5.9, 2.5) * mm, "end": v(-3.77, 4.62) * mm});
            skLineSegment(sketch, "E8.3.11.4", {"start": v(-3.77, 0.38) * mm, "end": v(-1.65, 2.5) * mm});
            skLineSegment(sketch, "E8.6.11.4", {"start": v(-5.9, 2.5) * mm, "end": v(-3.77, 0.38) * mm});
            skLineSegment(sketch, "E8.9.11.4", {"start": v(-3.77, 4.62) * mm, "end": v(-1.65, 2.5) * mm});
            skLineSegment(sketch, "E8.0.11.5", {"start": v(-5.9, 7.5) * mm, "end": v(-3.77, 9.62) * mm});
            skLineSegment(sketch, "E8.3.11.5", {"start": v(-3.77, 5.38) * mm, "end": v(-1.65, 7.5) * mm});
            skLineSegment(sketch, "E8.6.11.5", {"start": v(-5.9, 7.5) * mm, "end": v(-3.77, 5.38) * mm});
            skLineSegment(sketch, "E8.9.11.5", {"start": v(-3.77, 9.62) * mm, "end": v(-1.65, 7.5) * mm});
            skLineSegment(sketch, "E8.0.11.6", {"start": v(-5.9, 12.5) * mm, "end": v(-3.77, 14.62) * mm});
            skLineSegment(sketch, "E8.3.11.6", {"start": v(-3.77, 10.38) * mm, "end": v(-1.65, 12.5) * mm});
            skLineSegment(sketch, "E8.6.11.6", {"start": v(-5.9, 12.5) * mm, "end": v(-3.77, 10.38) * mm});
            skLineSegment(sketch, "E8.9.11.6", {"start": v(-3.77, 14.62) * mm, "end": v(-1.65, 12.5) * mm});
            skLineSegment(sketch, "E8.0.11.7", {"start": v(-5.9, 17.5) * mm, "end": v(-3.77, 19.62) * mm});
            skLineSegment(sketch, "E8.3.11.7", {"start": v(-3.77, 15.38) * mm, "end": v(-1.65, 17.5) * mm});
            skLineSegment(sketch, "E8.6.11.7", {"start": v(-5.9, 17.5) * mm, "end": v(-3.77, 15.38) * mm});
            skLineSegment(sketch, "E8.9.11.7", {"start": v(-3.77, 19.62) * mm, "end": v(-1.65, 17.5) * mm});
            skLineSegment(sketch, "E8.0.12.0", {"start": v(-0.9, -17.5) * mm, "end": v(1.23, -15.38) * mm});
            skLineSegment(sketch, "E8.3.12.0", {"start": v(1.23, -19.62) * mm, "end": v(3.35, -17.5) * mm});
            skLineSegment(sketch, "E8.6.12.0", {"start": v(-0.9, -17.5) * mm, "end": v(1.23, -19.62) * mm});
            skLineSegment(sketch, "E8.9.12.0", {"start": v(1.23, -15.38) * mm, "end": v(3.35, -17.5) * mm});
            skLineSegment(sketch, "E8.0.12.1", {"start": v(-0.9, -12.5) * mm, "end": v(1.23, -10.38) * mm});
            skLineSegment(sketch, "E8.3.12.1", {"start": v(1.23, -14.62) * mm, "end": v(3.35, -12.5) * mm});
            skLineSegment(sketch, "E8.6.12.1", {"start": v(-0.9, -12.5) * mm, "end": v(1.23, -14.62) * mm});
            skLineSegment(sketch, "E8.9.12.1", {"start": v(1.23, -10.38) * mm, "end": v(3.35, -12.5) * mm});
            skLineSegment(sketch, "E8.0.12.2", {"start": v(-0.9, -7.5) * mm, "end": v(1.23, -5.38) * mm});
            skLineSegment(sketch, "E8.3.12.2", {"start": v(1.23, -9.62) * mm, "end": v(3.35, -7.5) * mm});
            skLineSegment(sketch, "E8.6.12.2", {"start": v(-0.9, -7.5) * mm, "end": v(1.23, -9.62) * mm});
            skLineSegment(sketch, "E8.9.12.2", {"start": v(1.23, -5.38) * mm, "end": v(3.35, -7.5) * mm});
            skLineSegment(sketch, "E8.0.12.3", {"start": v(-0.9, -2.5) * mm, "end": v(1.23, -0.38) * mm});
            skLineSegment(sketch, "E8.3.12.3", {"start": v(1.23, -4.62) * mm, "end": v(3.35, -2.5) * mm});
            skLineSegment(sketch, "E8.6.12.3", {"start": v(-0.9, -2.5) * mm, "end": v(1.23, -4.62) * mm});
            skLineSegment(sketch, "E8.9.12.3", {"start": v(1.23, -0.38) * mm, "end": v(3.35, -2.5) * mm});
            skLineSegment(sketch, "E8.0.12.4", {"start": v(-0.9, 2.5) * mm, "end": v(1.23, 4.62) * mm});
            skLineSegment(sketch, "E8.3.12.4", {"start": v(1.23, 0.38) * mm, "end": v(3.35, 2.5) * mm});
            skLineSegment(sketch, "E8.6.12.4", {"start": v(-0.9, 2.5) * mm, "end": v(1.23, 0.38) * mm});
            skLineSegment(sketch, "E8.9.12.4", {"start": v(1.23, 4.62) * mm, "end": v(3.35, 2.5) * mm});
            skLineSegment(sketch, "E8.0.12.5", {"start": v(-0.9, 7.5) * mm, "end": v(1.23, 9.62) * mm});
            skLineSegment(sketch, "E8.3.12.5", {"start": v(1.23, 5.38) * mm, "end": v(3.35, 7.5) * mm});
            skLineSegment(sketch, "E8.6.12.5", {"start": v(-0.9, 7.5) * mm, "end": v(1.23, 5.38) * mm});
            skLineSegment(sketch, "E8.9.12.5", {"start": v(1.23, 9.62) * mm, "end": v(3.35, 7.5) * mm});
            skLineSegment(sketch, "E8.0.12.6", {"start": v(-0.9, 12.5) * mm, "end": v(1.23, 14.62) * mm});
            skLineSegment(sketch, "E8.3.12.6", {"start": v(1.23, 10.38) * mm, "end": v(3.35, 12.5) * mm});
            skLineSegment(sketch, "E8.6.12.6", {"start": v(-0.9, 12.5) * mm, "end": v(1.23, 10.38) * mm});
            skLineSegment(sketch, "E8.9.12.6", {"start": v(1.23, 14.62) * mm, "end": v(3.35, 12.5) * mm});
            skLineSegment(sketch, "E8.0.12.7", {"start": v(-0.9, 17.5) * mm, "end": v(1.23, 19.62) * mm});
            skLineSegment(sketch, "E8.3.12.7", {"start": v(1.23, 15.38) * mm, "end": v(3.35, 17.5) * mm});
            skLineSegment(sketch, "E8.6.12.7", {"start": v(-0.9, 17.5) * mm, "end": v(1.23, 15.38) * mm});
            skLineSegment(sketch, "E8.9.12.7", {"start": v(1.23, 19.62) * mm, "end": v(3.35, 17.5) * mm});
            skLineSegment(sketch, "E8.0.13.0", {"start": v(4.1, -17.5) * mm, "end": v(6.23, -15.38) * mm});
            skLineSegment(sketch, "E8.3.13.0", {"start": v(6.23, -19.62) * mm, "end": v(8.35, -17.5) * mm});
            skLineSegment(sketch, "E8.6.13.0", {"start": v(4.1, -17.5) * mm, "end": v(6.23, -19.62) * mm});
            skLineSegment(sketch, "E8.9.13.0", {"start": v(6.23, -15.38) * mm, "end": v(8.35, -17.5) * mm});
            skLineSegment(sketch, "E8.0.13.1", {"start": v(4.1, -12.5) * mm, "end": v(6.23, -10.38) * mm});
            skLineSegment(sketch, "E8.3.13.1", {"start": v(6.23, -14.62) * mm, "end": v(8.35, -12.5) * mm});
            skLineSegment(sketch, "E8.6.13.1", {"start": v(4.1, -12.5) * mm, "end": v(6.23, -14.62) * mm});
            skLineSegment(sketch, "E8.9.13.1", {"start": v(6.23, -10.38) * mm, "end": v(8.35, -12.5) * mm});
            skLineSegment(sketch, "E8.0.13.2", {"start": v(4.1, -7.5) * mm, "end": v(6.23, -5.38) * mm});
            skLineSegment(sketch, "E8.3.13.2", {"start": v(6.23, -9.62) * mm, "end": v(8.35, -7.5) * mm});
            skLineSegment(sketch, "E8.6.13.2", {"start": v(4.1, -7.5) * mm, "end": v(6.23, -9.62) * mm});
            skLineSegment(sketch, "E8.9.13.2", {"start": v(6.23, -5.38) * mm, "end": v(8.35, -7.5) * mm});
            skLineSegment(sketch, "E8.0.13.3", {"start": v(4.1, -2.5) * mm, "end": v(6.23, -0.38) * mm});
            skLineSegment(sketch, "E8.3.13.3", {"start": v(6.23, -4.62) * mm, "end": v(8.35, -2.5) * mm});
            skLineSegment(sketch, "E8.6.13.3", {"start": v(4.1, -2.5) * mm, "end": v(6.23, -4.62) * mm});
            skLineSegment(sketch, "E8.9.13.3", {"start": v(6.23, -0.38) * mm, "end": v(8.35, -2.5) * mm});
            skLineSegment(sketch, "E8.0.13.4", {"start": v(4.1, 2.5) * mm, "end": v(6.23, 4.62) * mm});
            skLineSegment(sketch, "E8.3.13.4", {"start": v(6.23, 0.38) * mm, "end": v(8.35, 2.5) * mm});
            skLineSegment(sketch, "E8.6.13.4", {"start": v(4.1, 2.5) * mm, "end": v(6.23, 0.38) * mm});
            skLineSegment(sketch, "E8.9.13.4", {"start": v(6.23, 4.62) * mm, "end": v(8.35, 2.5) * mm});
            skLineSegment(sketch, "E8.0.13.5", {"start": v(4.1, 7.5) * mm, "end": v(6.23, 9.62) * mm});
            skLineSegment(sketch, "E8.3.13.5", {"start": v(6.23, 5.38) * mm, "end": v(8.35, 7.5) * mm});
            skLineSegment(sketch, "E8.6.13.5", {"start": v(4.1, 7.5) * mm, "end": v(6.23, 5.38) * mm});
            skLineSegment(sketch, "E8.9.13.5", {"start": v(6.23, 9.62) * mm, "end": v(8.35, 7.5) * mm});
            skLineSegment(sketch, "E8.0.13.6", {"start": v(4.1, 12.5) * mm, "end": v(6.23, 14.62) * mm});
            skLineSegment(sketch, "E8.3.13.6", {"start": v(6.23, 10.38) * mm, "end": v(8.35, 12.5) * mm});
            skLineSegment(sketch, "E8.6.13.6", {"start": v(4.1, 12.5) * mm, "end": v(6.23, 10.38) * mm});
            skLineSegment(sketch, "E8.9.13.6", {"start": v(6.23, 14.62) * mm, "end": v(8.35, 12.5) * mm});
            skLineSegment(sketch, "E8.0.13.7", {"start": v(4.1, 17.5) * mm, "end": v(6.23, 19.62) * mm});
            skLineSegment(sketch, "E8.3.13.7", {"start": v(6.23, 15.38) * mm, "end": v(8.35, 17.5) * mm});
            skLineSegment(sketch, "E8.6.13.7", {"start": v(4.1, 17.5) * mm, "end": v(6.23, 15.38) * mm});
            skLineSegment(sketch, "E8.9.13.7", {"start": v(6.23, 19.62) * mm, "end": v(8.35, 17.5) * mm});
            skLineSegment(sketch, "E8.0.14.0", {"start": v(9.1, -17.5) * mm, "end": v(11.23, -15.38) * mm});
            skLineSegment(sketch, "E8.3.14.0", {"start": v(11.23, -19.62) * mm, "end": v(13.35, -17.5) * mm});
            skLineSegment(sketch, "E8.6.14.0", {"start": v(9.1, -17.5) * mm, "end": v(11.23, -19.62) * mm});
            skLineSegment(sketch, "E8.9.14.0", {"start": v(11.23, -15.38) * mm, "end": v(13.35, -17.5) * mm});
            skLineSegment(sketch, "E8.0.14.1", {"start": v(9.1, -12.5) * mm, "end": v(11.23, -10.38) * mm});
            skLineSegment(sketch, "E8.3.14.1", {"start": v(11.23, -14.62) * mm, "end": v(13.35, -12.5) * mm});
            skLineSegment(sketch, "E8.6.14.1", {"start": v(9.1, -12.5) * mm, "end": v(11.23, -14.62) * mm});
            skLineSegment(sketch, "E8.9.14.1", {"start": v(11.23, -10.38) * mm, "end": v(13.35, -12.5) * mm});
            skLineSegment(sketch, "E8.0.14.2", {"start": v(9.1, -7.5) * mm, "end": v(11.23, -5.38) * mm});
            skLineSegment(sketch, "E8.3.14.2", {"start": v(11.23, -9.62) * mm, "end": v(13.35, -7.5) * mm});
            skLineSegment(sketch, "E8.6.14.2", {"start": v(9.1, -7.5) * mm, "end": v(11.23, -9.62) * mm});
            skLineSegment(sketch, "E8.9.14.2", {"start": v(11.23, -5.38) * mm, "end": v(13.35, -7.5) * mm});
            skLineSegment(sketch, "E8.0.14.3", {"start": v(9.1, -2.5) * mm, "end": v(11.23, -0.38) * mm});
            skLineSegment(sketch, "E8.3.14.3", {"start": v(11.23, -4.62) * mm, "end": v(13.35, -2.5) * mm});
            skLineSegment(sketch, "E8.6.14.3", {"start": v(9.1, -2.5) * mm, "end": v(11.23, -4.62) * mm});
            skLineSegment(sketch, "E8.9.14.3", {"start": v(11.23, -0.38) * mm, "end": v(13.35, -2.5) * mm});
            skLineSegment(sketch, "E8.0.14.4", {"start": v(9.1, 2.5) * mm, "end": v(11.23, 4.62) * mm});
            skLineSegment(sketch, "E8.3.14.4", {"start": v(11.23, 0.38) * mm, "end": v(13.35, 2.5) * mm});
            skLineSegment(sketch, "E8.6.14.4", {"start": v(9.1, 2.5) * mm, "end": v(11.23, 0.38) * mm});
            skLineSegment(sketch, "E8.9.14.4", {"start": v(11.23, 4.62) * mm, "end": v(13.35, 2.5) * mm});
            skLineSegment(sketch, "E8.0.14.5", {"start": v(9.1, 7.5) * mm, "end": v(11.23, 9.62) * mm});
            skLineSegment(sketch, "E8.3.14.5", {"start": v(11.23, 5.38) * mm, "end": v(13.35, 7.5) * mm});
            skLineSegment(sketch, "E8.6.14.5", {"start": v(9.1, 7.5) * mm, "end": v(11.23, 5.38) * mm});
            skLineSegment(sketch, "E8.9.14.5", {"start": v(11.23, 9.62) * mm, "end": v(13.35, 7.5) * mm});
            skLineSegment(sketch, "E8.0.14.6", {"start": v(9.1, 12.5) * mm, "end": v(11.23, 14.62) * mm});
            skLineSegment(sketch, "E8.3.14.6", {"start": v(11.23, 10.38) * mm, "end": v(13.35, 12.5) * mm});
            skLineSegment(sketch, "E8.6.14.6", {"start": v(9.1, 12.5) * mm, "end": v(11.23, 10.38) * mm});
            skLineSegment(sketch, "E8.9.14.6", {"start": v(11.23, 14.62) * mm, "end": v(13.35, 12.5) * mm});
            skLineSegment(sketch, "E8.0.14.7", {"start": v(9.1, 17.5) * mm, "end": v(11.23, 19.62) * mm});
            skLineSegment(sketch, "E8.3.14.7", {"start": v(11.23, 15.38) * mm, "end": v(13.35, 17.5) * mm});
            skLineSegment(sketch, "E8.6.14.7", {"start": v(9.1, 17.5) * mm, "end": v(11.23, 15.38) * mm});
            skLineSegment(sketch, "E8.9.14.7", {"start": v(11.23, 19.62) * mm, "end": v(13.35, 17.5) * mm});
            skLineSegment(sketch, "E8.0.15.0", {"start": v(14.1, -17.5) * mm, "end": v(16.23, -15.38) * mm});
            skLineSegment(sketch, "E8.3.15.0", {"start": v(16.23, -19.62) * mm, "end": v(18.35, -17.5) * mm});
            skLineSegment(sketch, "E8.6.15.0", {"start": v(14.1, -17.5) * mm, "end": v(16.23, -19.62) * mm});
            skLineSegment(sketch, "E8.9.15.0", {"start": v(16.23, -15.38) * mm, "end": v(18.35, -17.5) * mm});
            skLineSegment(sketch, "E8.0.15.1", {"start": v(14.1, -12.5) * mm, "end": v(16.23, -10.38) * mm});
            skLineSegment(sketch, "E8.3.15.1", {"start": v(16.23, -14.62) * mm, "end": v(18.35, -12.5) * mm});
            skLineSegment(sketch, "E8.6.15.1", {"start": v(14.1, -12.5) * mm, "end": v(16.23, -14.62) * mm});
            skLineSegment(sketch, "E8.9.15.1", {"start": v(16.23, -10.38) * mm, "end": v(18.35, -12.5) * mm});
            skLineSegment(sketch, "E8.0.15.2", {"start": v(14.1, -7.5) * mm, "end": v(16.23, -5.38) * mm});
            skLineSegment(sketch, "E8.3.15.2", {"start": v(16.23, -9.62) * mm, "end": v(18.35, -7.5) * mm});
            skLineSegment(sketch, "E8.6.15.2", {"start": v(14.1, -7.5) * mm, "end": v(16.23, -9.62) * mm});
            skLineSegment(sketch, "E8.9.15.2", {"start": v(16.23, -5.38) * mm, "end": v(18.35, -7.5) * mm});
            skLineSegment(sketch, "E8.0.15.3", {"start": v(14.1, -2.5) * mm, "end": v(16.23, -0.38) * mm});
            skLineSegment(sketch, "E8.3.15.3", {"start": v(16.23, -4.62) * mm, "end": v(18.35, -2.5) * mm});
            skLineSegment(sketch, "E8.6.15.3", {"start": v(14.1, -2.5) * mm, "end": v(16.23, -4.62) * mm});
            skLineSegment(sketch, "E8.9.15.3", {"start": v(16.23, -0.38) * mm, "end": v(18.35, -2.5) * mm});
            skLineSegment(sketch, "E8.0.15.4", {"start": v(14.1, 2.5) * mm, "end": v(16.23, 4.62) * mm});
            skLineSegment(sketch, "E8.3.15.4", {"start": v(16.23, 0.38) * mm, "end": v(18.35, 2.5) * mm});
            skLineSegment(sketch, "E8.6.15.4", {"start": v(14.1, 2.5) * mm, "end": v(16.23, 0.38) * mm});
            skLineSegment(sketch, "E8.9.15.4", {"start": v(16.23, 4.62) * mm, "end": v(18.35, 2.5) * mm});
            skLineSegment(sketch, "E8.0.15.5", {"start": v(14.1, 7.5) * mm, "end": v(16.23, 9.62) * mm});
            skLineSegment(sketch, "E8.3.15.5", {"start": v(16.23, 5.38) * mm, "end": v(18.35, 7.5) * mm});
            skLineSegment(sketch, "E8.6.15.5", {"start": v(14.1, 7.5) * mm, "end": v(16.23, 5.38) * mm});
            skLineSegment(sketch, "E8.9.15.5", {"start": v(16.23, 9.62) * mm, "end": v(18.35, 7.5) * mm});
            skLineSegment(sketch, "E8.0.15.6", {"start": v(14.1, 12.5) * mm, "end": v(16.23, 14.62) * mm});
            skLineSegment(sketch, "E8.3.15.6", {"start": v(16.23, 10.38) * mm, "end": v(18.35, 12.5) * mm});
            skLineSegment(sketch, "E8.6.15.6", {"start": v(14.1, 12.5) * mm, "end": v(16.23, 10.38) * mm});
            skLineSegment(sketch, "E8.9.15.6", {"start": v(16.23, 14.62) * mm, "end": v(18.35, 12.5) * mm});
            skLineSegment(sketch, "E8.0.15.7", {"start": v(14.1, 17.5) * mm, "end": v(16.23, 19.62) * mm});
            skLineSegment(sketch, "E8.3.15.7", {"start": v(16.23, 15.38) * mm, "end": v(18.35, 17.5) * mm});
            skLineSegment(sketch, "E8.6.15.7", {"start": v(14.1, 17.5) * mm, "end": v(16.23, 15.38) * mm});
            skLineSegment(sketch, "E8.9.15.7", {"start": v(16.23, 19.62) * mm, "end": v(18.35, 17.5) * mm});
            skLineSegment(sketch, "E8.0.16.0", {"start": v(19.1, -17.5) * mm, "end": v(21.23, -15.38) * mm});
            skLineSegment(sketch, "E8.3.16.0", {"start": v(21.23, -19.62) * mm, "end": v(23.35, -17.5) * mm});
            skLineSegment(sketch, "E8.6.16.0", {"start": v(19.1, -17.5) * mm, "end": v(21.23, -19.62) * mm});
            skLineSegment(sketch, "E8.9.16.0", {"start": v(21.23, -15.38) * mm, "end": v(23.35, -17.5) * mm});
            skLineSegment(sketch, "E8.0.16.1", {"start": v(19.1, -12.5) * mm, "end": v(21.23, -10.38) * mm});
            skLineSegment(sketch, "E8.3.16.1", {"start": v(21.23, -14.62) * mm, "end": v(23.35, -12.5) * mm});
            skLineSegment(sketch, "E8.6.16.1", {"start": v(19.1, -12.5) * mm, "end": v(21.23, -14.62) * mm});
            skLineSegment(sketch, "E8.9.16.1", {"start": v(21.23, -10.38) * mm, "end": v(23.35, -12.5) * mm});
            skLineSegment(sketch, "E8.0.16.2", {"start": v(19.1, -7.5) * mm, "end": v(21.23, -5.38) * mm});
            skLineSegment(sketch, "E8.3.16.2", {"start": v(21.23, -9.62) * mm, "end": v(23.35, -7.5) * mm});
            skLineSegment(sketch, "E8.6.16.2", {"start": v(19.1, -7.5) * mm, "end": v(21.23, -9.62) * mm});
            skLineSegment(sketch, "E8.9.16.2", {"start": v(21.23, -5.38) * mm, "end": v(23.35, -7.5) * mm});
            skLineSegment(sketch, "E8.0.16.3", {"start": v(19.1, -2.5) * mm, "end": v(21.23, -0.38) * mm});
            skLineSegment(sketch, "E8.3.16.3", {"start": v(21.23, -4.62) * mm, "end": v(23.35, -2.5) * mm});
            skLineSegment(sketch, "E8.6.16.3", {"start": v(19.1, -2.5) * mm, "end": v(21.23, -4.62) * mm});
            skLineSegment(sketch, "E8.9.16.3", {"start": v(21.23, -0.38) * mm, "end": v(23.35, -2.5) * mm});
            skLineSegment(sketch, "E8.0.16.4", {"start": v(19.1, 2.5) * mm, "end": v(21.23, 4.62) * mm});
            skLineSegment(sketch, "E8.3.16.4", {"start": v(21.23, 0.38) * mm, "end": v(23.35, 2.5) * mm});
            skLineSegment(sketch, "E8.6.16.4", {"start": v(19.1, 2.5) * mm, "end": v(21.23, 0.38) * mm});
            skLineSegment(sketch, "E8.9.16.4", {"start": v(21.23, 4.62) * mm, "end": v(23.35, 2.5) * mm});
            skLineSegment(sketch, "E8.0.16.5", {"start": v(19.1, 7.5) * mm, "end": v(21.23, 9.62) * mm});
            skLineSegment(sketch, "E8.3.16.5", {"start": v(21.23, 5.38) * mm, "end": v(23.35, 7.5) * mm});
            skLineSegment(sketch, "E8.6.16.5", {"start": v(19.1, 7.5) * mm, "end": v(21.23, 5.38) * mm});
            skLineSegment(sketch, "E8.9.16.5", {"start": v(21.23, 9.62) * mm, "end": v(23.35, 7.5) * mm});
            skLineSegment(sketch, "E8.0.16.6", {"start": v(19.1, 12.5) * mm, "end": v(21.23, 14.62) * mm});
            skLineSegment(sketch, "E8.3.16.6", {"start": v(21.23, 10.38) * mm, "end": v(23.35, 12.5) * mm});
            skLineSegment(sketch, "E8.6.16.6", {"start": v(19.1, 12.5) * mm, "end": v(21.23, 10.38) * mm});
            skLineSegment(sketch, "E8.9.16.6", {"start": v(21.23, 14.62) * mm, "end": v(23.35, 12.5) * mm});
            skLineSegment(sketch, "E8.0.16.7", {"start": v(19.1, 17.5) * mm, "end": v(21.23, 19.62) * mm});
            skLineSegment(sketch, "E8.3.16.7", {"start": v(21.23, 15.38) * mm, "end": v(23.35, 17.5) * mm});
            skLineSegment(sketch, "E8.6.16.7", {"start": v(19.1, 17.5) * mm, "end": v(21.23, 15.38) * mm});
            skLineSegment(sketch, "E8.9.16.7", {"start": v(21.23, 19.62) * mm, "end": v(23.35, 17.5) * mm});
            skLineSegment(sketch, "E8.0.17.0", {"start": v(24.1, -17.5) * mm, "end": v(26.23, -15.38) * mm});
            skLineSegment(sketch, "E8.3.17.0", {"start": v(26.23, -19.62) * mm, "end": v(28.35, -17.5) * mm});
            skLineSegment(sketch, "E8.6.17.0", {"start": v(24.1, -17.5) * mm, "end": v(26.23, -19.62) * mm});
            skLineSegment(sketch, "E8.9.17.0", {"start": v(26.23, -15.38) * mm, "end": v(28.35, -17.5) * mm});
            skLineSegment(sketch, "E8.0.17.1", {"start": v(24.1, -12.5) * mm, "end": v(26.23, -10.38) * mm});
            skLineSegment(sketch, "E8.3.17.1", {"start": v(26.23, -14.62) * mm, "end": v(28.35, -12.5) * mm});
            skLineSegment(sketch, "E8.6.17.1", {"start": v(24.1, -12.5) * mm, "end": v(26.23, -14.62) * mm});
            skLineSegment(sketch, "E8.9.17.1", {"start": v(26.23, -10.38) * mm, "end": v(28.35, -12.5) * mm});
            skLineSegment(sketch, "E8.0.17.2", {"start": v(24.1, -7.5) * mm, "end": v(26.23, -5.38) * mm});
            skLineSegment(sketch, "E8.3.17.2", {"start": v(26.23, -9.62) * mm, "end": v(28.35, -7.5) * mm});
            skLineSegment(sketch, "E8.6.17.2", {"start": v(24.1, -7.5) * mm, "end": v(26.23, -9.62) * mm});
            skLineSegment(sketch, "E8.9.17.2", {"start": v(26.23, -5.38) * mm, "end": v(28.35, -7.5) * mm});
            skLineSegment(sketch, "E8.0.17.3", {"start": v(24.1, -2.5) * mm, "end": v(26.23, -0.38) * mm});
            skLineSegment(sketch, "E8.3.17.3", {"start": v(26.23, -4.62) * mm, "end": v(28.35, -2.5) * mm});
            skLineSegment(sketch, "E8.6.17.3", {"start": v(24.1, -2.5) * mm, "end": v(26.23, -4.62) * mm});
            skLineSegment(sketch, "E8.9.17.3", {"start": v(26.23, -0.38) * mm, "end": v(28.35, -2.5) * mm});
            skLineSegment(sketch, "E8.0.17.4", {"start": v(24.1, 2.5) * mm, "end": v(26.23, 4.62) * mm});
            skLineSegment(sketch, "E8.3.17.4", {"start": v(26.23, 0.38) * mm, "end": v(28.35, 2.5) * mm});
            skLineSegment(sketch, "E8.6.17.4", {"start": v(24.1, 2.5) * mm, "end": v(26.23, 0.38) * mm});
            skLineSegment(sketch, "E8.9.17.4", {"start": v(26.23, 4.62) * mm, "end": v(28.35, 2.5) * mm});
            skLineSegment(sketch, "E8.0.17.5", {"start": v(24.1, 7.5) * mm, "end": v(26.23, 9.62) * mm});
            skLineSegment(sketch, "E8.3.17.5", {"start": v(26.23, 5.38) * mm, "end": v(28.35, 7.5) * mm});
            skLineSegment(sketch, "E8.6.17.5", {"start": v(24.1, 7.5) * mm, "end": v(26.23, 5.38) * mm});
            skLineSegment(sketch, "E8.9.17.5", {"start": v(26.23, 9.62) * mm, "end": v(28.35, 7.5) * mm});
            skLineSegment(sketch, "E8.0.17.6", {"start": v(24.1, 12.5) * mm, "end": v(26.23, 14.62) * mm});
            skLineSegment(sketch, "E8.3.17.6", {"start": v(26.23, 10.38) * mm, "end": v(28.35, 12.5) * mm});
            skLineSegment(sketch, "E8.6.17.6", {"start": v(24.1, 12.5) * mm, "end": v(26.23, 10.38) * mm});
            skLineSegment(sketch, "E8.9.17.6", {"start": v(26.23, 14.62) * mm, "end": v(28.35, 12.5) * mm});
            skLineSegment(sketch, "E8.0.17.7", {"start": v(24.1, 17.5) * mm, "end": v(26.23, 19.62) * mm});
            skLineSegment(sketch, "E8.3.17.7", {"start": v(26.23, 15.38) * mm, "end": v(28.35, 17.5) * mm});
            skLineSegment(sketch, "E8.6.17.7", {"start": v(24.1, 17.5) * mm, "end": v(26.23, 15.38) * mm});
            skLineSegment(sketch, "E8.9.17.7", {"start": v(26.23, 19.62) * mm, "end": v(28.35, 17.5) * mm});
            skLineSegment(sketch, "E8.0.18.0", {"start": v(29.1, -17.5) * mm, "end": v(31.23, -15.38) * mm});
            skLineSegment(sketch, "E8.3.18.0", {"start": v(31.23, -19.62) * mm, "end": v(33.35, -17.5) * mm});
            skLineSegment(sketch, "E8.6.18.0", {"start": v(29.1, -17.5) * mm, "end": v(31.23, -19.62) * mm});
            skLineSegment(sketch, "E8.9.18.0", {"start": v(31.23, -15.38) * mm, "end": v(33.35, -17.5) * mm});
            skLineSegment(sketch, "E8.0.18.1", {"start": v(29.1, -12.5) * mm, "end": v(31.23, -10.38) * mm});
            skLineSegment(sketch, "E8.3.18.1", {"start": v(31.23, -14.62) * mm, "end": v(33.35, -12.5) * mm});
            skLineSegment(sketch, "E8.6.18.1", {"start": v(29.1, -12.5) * mm, "end": v(31.23, -14.62) * mm});
            skLineSegment(sketch, "E8.9.18.1", {"start": v(31.23, -10.38) * mm, "end": v(33.35, -12.5) * mm});
            skLineSegment(sketch, "E8.0.18.2", {"start": v(29.1, -7.5) * mm, "end": v(31.23, -5.38) * mm});
            skLineSegment(sketch, "E8.3.18.2", {"start": v(31.23, -9.62) * mm, "end": v(33.35, -7.5) * mm});
            skLineSegment(sketch, "E8.6.18.2", {"start": v(29.1, -7.5) * mm, "end": v(31.23, -9.62) * mm});
            skLineSegment(sketch, "E8.9.18.2", {"start": v(31.23, -5.38) * mm, "end": v(33.35, -7.5) * mm});
            skLineSegment(sketch, "E8.0.18.3", {"start": v(29.1, -2.5) * mm, "end": v(31.23, -0.38) * mm});
            skLineSegment(sketch, "E8.3.18.3", {"start": v(31.23, -4.62) * mm, "end": v(33.35, -2.5) * mm});
            skLineSegment(sketch, "E8.6.18.3", {"start": v(29.1, -2.5) * mm, "end": v(31.23, -4.62) * mm});
            skLineSegment(sketch, "E8.9.18.3", {"start": v(31.23, -0.38) * mm, "end": v(33.35, -2.5) * mm});
            skLineSegment(sketch, "E8.0.18.4", {"start": v(29.1, 2.5) * mm, "end": v(31.23, 4.62) * mm});
            skLineSegment(sketch, "E8.3.18.4", {"start": v(31.23, 0.38) * mm, "end": v(33.35, 2.5) * mm});
            skLineSegment(sketch, "E8.6.18.4", {"start": v(29.1, 2.5) * mm, "end": v(31.23, 0.38) * mm});
            skLineSegment(sketch, "E8.9.18.4", {"start": v(31.23, 4.62) * mm, "end": v(33.35, 2.5) * mm});
            skLineSegment(sketch, "E8.0.18.5", {"start": v(29.1, 7.5) * mm, "end": v(31.23, 9.62) * mm});
            skLineSegment(sketch, "E8.3.18.5", {"start": v(31.23, 5.38) * mm, "end": v(33.35, 7.5) * mm});
            skLineSegment(sketch, "E8.6.18.5", {"start": v(29.1, 7.5) * mm, "end": v(31.23, 5.38) * mm});
            skLineSegment(sketch, "E8.9.18.5", {"start": v(31.23, 9.62) * mm, "end": v(33.35, 7.5) * mm});
            skLineSegment(sketch, "E8.0.18.6", {"start": v(29.1, 12.5) * mm, "end": v(31.23, 14.62) * mm});
            skLineSegment(sketch, "E8.3.18.6", {"start": v(31.23, 10.38) * mm, "end": v(33.35, 12.5) * mm});
            skLineSegment(sketch, "E8.6.18.6", {"start": v(29.1, 12.5) * mm, "end": v(31.23, 10.38) * mm});
            skLineSegment(sketch, "E8.9.18.6", {"start": v(31.23, 14.62) * mm, "end": v(33.35, 12.5) * mm});
            skLineSegment(sketch, "E8.0.18.7", {"start": v(29.1, 17.5) * mm, "end": v(31.23, 19.62) * mm});
            skLineSegment(sketch, "E8.3.18.7", {"start": v(31.23, 15.38) * mm, "end": v(33.35, 17.5) * mm});
            skLineSegment(sketch, "E8.6.18.7", {"start": v(29.1, 17.5) * mm, "end": v(31.23, 15.38) * mm});
            skLineSegment(sketch, "E8.9.18.7", {"start": v(31.23, 19.62) * mm, "end": v(33.35, 17.5) * mm});
            skLineSegment(sketch, "E8.0.19.0", {"start": v(34.1, -17.5) * mm, "end": v(36.23, -15.38) * mm});
            skLineSegment(sketch, "E8.3.19.0", {"start": v(36.23, -19.62) * mm, "end": v(38.35, -17.5) * mm});
            skLineSegment(sketch, "E8.6.19.0", {"start": v(34.1, -17.5) * mm, "end": v(36.23, -19.62) * mm});
            skLineSegment(sketch, "E8.9.19.0", {"start": v(36.23, -15.38) * mm, "end": v(38.35, -17.5) * mm});
            skLineSegment(sketch, "E8.0.19.1", {"start": v(34.1, -12.5) * mm, "end": v(36.23, -10.38) * mm});
            skLineSegment(sketch, "E8.3.19.1", {"start": v(36.23, -14.62) * mm, "end": v(38.35, -12.5) * mm});
            skLineSegment(sketch, "E8.6.19.1", {"start": v(34.1, -12.5) * mm, "end": v(36.23, -14.62) * mm});
            skLineSegment(sketch, "E8.9.19.1", {"start": v(36.23, -10.38) * mm, "end": v(38.35, -12.5) * mm});
            skLineSegment(sketch, "E8.0.19.2", {"start": v(34.1, -7.5) * mm, "end": v(36.23, -5.38) * mm});
            skLineSegment(sketch, "E8.3.19.2", {"start": v(36.23, -9.62) * mm, "end": v(38.35, -7.5) * mm});
            skLineSegment(sketch, "E8.6.19.2", {"start": v(34.1, -7.5) * mm, "end": v(36.23, -9.62) * mm});
            skLineSegment(sketch, "E8.9.19.2", {"start": v(36.23, -5.38) * mm, "end": v(38.35, -7.5) * mm});
            skLineSegment(sketch, "E8.0.19.3", {"start": v(34.1, -2.5) * mm, "end": v(36.23, -0.38) * mm});
            skLineSegment(sketch, "E8.3.19.3", {"start": v(36.23, -4.62) * mm, "end": v(38.35, -2.5) * mm});
            skLineSegment(sketch, "E8.6.19.3", {"start": v(34.1, -2.5) * mm, "end": v(36.23, -4.62) * mm});
            skLineSegment(sketch, "E8.9.19.3", {"start": v(36.23, -0.38) * mm, "end": v(38.35, -2.5) * mm});
            skLineSegment(sketch, "E8.0.19.4", {"start": v(34.1, 2.5) * mm, "end": v(36.23, 4.62) * mm});
            skLineSegment(sketch, "E8.3.19.4", {"start": v(36.23, 0.38) * mm, "end": v(38.35, 2.5) * mm});
            skLineSegment(sketch, "E8.6.19.4", {"start": v(34.1, 2.5) * mm, "end": v(36.23, 0.38) * mm});
            skLineSegment(sketch, "E8.9.19.4", {"start": v(36.23, 4.62) * mm, "end": v(38.35, 2.5) * mm});
            skLineSegment(sketch, "E8.0.19.5", {"start": v(34.1, 7.5) * mm, "end": v(36.23, 9.62) * mm});
            skLineSegment(sketch, "E8.3.19.5", {"start": v(36.23, 5.38) * mm, "end": v(38.35, 7.5) * mm});
            skLineSegment(sketch, "E8.6.19.5", {"start": v(34.1, 7.5) * mm, "end": v(36.23, 5.38) * mm});
            skLineSegment(sketch, "E8.9.19.5", {"start": v(36.23, 9.62) * mm, "end": v(38.35, 7.5) * mm});
            skLineSegment(sketch, "E8.0.19.6", {"start": v(34.1, 12.5) * mm, "end": v(36.23, 14.62) * mm});
            skLineSegment(sketch, "E8.3.19.6", {"start": v(36.23, 10.38) * mm, "end": v(38.35, 12.5) * mm});
            skLineSegment(sketch, "E8.6.19.6", {"start": v(34.1, 12.5) * mm, "end": v(36.23, 10.38) * mm});
            skLineSegment(sketch, "E8.9.19.6", {"start": v(36.23, 14.62) * mm, "end": v(38.35, 12.5) * mm});
            skLineSegment(sketch, "E8.0.19.7", {"start": v(34.1, 17.5) * mm, "end": v(36.23, 19.62) * mm});
            skLineSegment(sketch, "E8.3.19.7", {"start": v(36.23, 15.38) * mm, "end": v(38.35, 17.5) * mm});
            skLineSegment(sketch, "E8.6.19.7", {"start": v(34.1, 17.5) * mm, "end": v(36.23, 15.38) * mm});
            skLineSegment(sketch, "E8.9.19.7", {"start": v(36.23, 19.62) * mm, "end": v(38.35, 17.5) * mm});
            skLineSegment(sketch, "E8.0.20.0", {"start": v(39.1, -17.5) * mm, "end": v(41.23, -15.38) * mm});
            skLineSegment(sketch, "E8.3.20.0", {"start": v(41.23, -19.62) * mm, "end": v(43.35, -17.5) * mm});
            skLineSegment(sketch, "E8.6.20.0", {"start": v(39.1, -17.5) * mm, "end": v(41.23, -19.62) * mm});
            skLineSegment(sketch, "E8.9.20.0", {"start": v(41.23, -15.38) * mm, "end": v(43.35, -17.5) * mm});
            skLineSegment(sketch, "E8.0.20.1", {"start": v(39.1, -12.5) * mm, "end": v(41.23, -10.38) * mm});
            skLineSegment(sketch, "E8.3.20.1", {"start": v(41.23, -14.62) * mm, "end": v(43.35, -12.5) * mm});
            skLineSegment(sketch, "E8.6.20.1", {"start": v(39.1, -12.5) * mm, "end": v(41.23, -14.62) * mm});
            skLineSegment(sketch, "E8.9.20.1", {"start": v(41.23, -10.38) * mm, "end": v(43.35, -12.5) * mm});
            skLineSegment(sketch, "E8.0.20.2", {"start": v(39.1, -7.5) * mm, "end": v(41.23, -5.38) * mm});
            skLineSegment(sketch, "E8.3.20.2", {"start": v(41.23, -9.62) * mm, "end": v(43.35, -7.5) * mm});
            skLineSegment(sketch, "E8.6.20.2", {"start": v(39.1, -7.5) * mm, "end": v(41.23, -9.62) * mm});
            skLineSegment(sketch, "E8.9.20.2", {"start": v(41.23, -5.38) * mm, "end": v(43.35, -7.5) * mm});
            skLineSegment(sketch, "E8.0.20.3", {"start": v(39.1, -2.5) * mm, "end": v(41.23, -0.38) * mm});
            skLineSegment(sketch, "E8.3.20.3", {"start": v(41.23, -4.62) * mm, "end": v(43.35, -2.5) * mm});
            skLineSegment(sketch, "E8.6.20.3", {"start": v(39.1, -2.5) * mm, "end": v(41.23, -4.62) * mm});
            skLineSegment(sketch, "E8.9.20.3", {"start": v(41.23, -0.38) * mm, "end": v(43.35, -2.5) * mm});
            skLineSegment(sketch, "E8.0.20.4", {"start": v(39.1, 2.5) * mm, "end": v(41.23, 4.62) * mm});
            skLineSegment(sketch, "E8.3.20.4", {"start": v(41.23, 0.38) * mm, "end": v(43.35, 2.5) * mm});
            skLineSegment(sketch, "E8.6.20.4", {"start": v(39.1, 2.5) * mm, "end": v(41.23, 0.38) * mm});
            skLineSegment(sketch, "E8.9.20.4", {"start": v(41.23, 4.62) * mm, "end": v(43.35, 2.5) * mm});
            skLineSegment(sketch, "E8.0.20.5", {"start": v(39.1, 7.5) * mm, "end": v(41.23, 9.62) * mm});
            skLineSegment(sketch, "E8.3.20.5", {"start": v(41.23, 5.38) * mm, "end": v(43.35, 7.5) * mm});
            skLineSegment(sketch, "E8.6.20.5", {"start": v(39.1, 7.5) * mm, "end": v(41.23, 5.38) * mm});
            skLineSegment(sketch, "E8.9.20.5", {"start": v(41.23, 9.62) * mm, "end": v(43.35, 7.5) * mm});
            skLineSegment(sketch, "E8.0.20.6", {"start": v(39.1, 12.5) * mm, "end": v(41.23, 14.62) * mm});
            skLineSegment(sketch, "E8.3.20.6", {"start": v(41.23, 10.38) * mm, "end": v(43.35, 12.5) * mm});
            skLineSegment(sketch, "E8.6.20.6", {"start": v(39.1, 12.5) * mm, "end": v(41.23, 10.38) * mm});
            skLineSegment(sketch, "E8.9.20.6", {"start": v(41.23, 14.62) * mm, "end": v(43.35, 12.5) * mm});
            skLineSegment(sketch, "E8.0.20.7", {"start": v(39.1, 17.5) * mm, "end": v(41.23, 19.62) * mm});
            skLineSegment(sketch, "E8.3.20.7", {"start": v(41.23, 15.38) * mm, "end": v(43.35, 17.5) * mm});
            skLineSegment(sketch, "E8.6.20.7", {"start": v(39.1, 17.5) * mm, "end": v(41.23, 15.38) * mm});
            skLineSegment(sketch, "E8.9.20.7", {"start": v(41.23, 19.62) * mm, "end": v(43.35, 17.5) * mm});
            skLineSegment(sketch, "E8.0.21.0", {"start": v(44.1, -17.5) * mm, "end": v(46.23, -15.38) * mm});
            skLineSegment(sketch, "E8.3.21.0", {"start": v(46.23, -19.62) * mm, "end": v(48.35, -17.5) * mm});
            skLineSegment(sketch, "E8.6.21.0", {"start": v(44.1, -17.5) * mm, "end": v(46.23, -19.62) * mm});
            skLineSegment(sketch, "E8.9.21.0", {"start": v(46.23, -15.38) * mm, "end": v(48.35, -17.5) * mm});
            skLineSegment(sketch, "E8.0.21.1", {"start": v(44.1, -12.5) * mm, "end": v(46.23, -10.38) * mm});
            skLineSegment(sketch, "E8.3.21.1", {"start": v(46.23, -14.62) * mm, "end": v(48.35, -12.5) * mm});
            skLineSegment(sketch, "E8.6.21.1", {"start": v(44.1, -12.5) * mm, "end": v(46.23, -14.62) * mm});
            skLineSegment(sketch, "E8.9.21.1", {"start": v(46.23, -10.38) * mm, "end": v(48.35, -12.5) * mm});
            skLineSegment(sketch, "E8.0.21.2", {"start": v(44.1, -7.5) * mm, "end": v(46.23, -5.38) * mm});
            skLineSegment(sketch, "E8.3.21.2", {"start": v(46.23, -9.62) * mm, "end": v(48.35, -7.5) * mm});
            skLineSegment(sketch, "E8.6.21.2", {"start": v(44.1, -7.5) * mm, "end": v(46.23, -9.62) * mm});
            skLineSegment(sketch, "E8.9.21.2", {"start": v(46.23, -5.38) * mm, "end": v(48.35, -7.5) * mm});
            skLineSegment(sketch, "E8.0.21.3", {"start": v(44.1, -2.5) * mm, "end": v(46.23, -0.38) * mm});
            skLineSegment(sketch, "E8.3.21.3", {"start": v(46.23, -4.62) * mm, "end": v(48.35, -2.5) * mm});
            skLineSegment(sketch, "E8.6.21.3", {"start": v(44.1, -2.5) * mm, "end": v(46.23, -4.62) * mm});
            skLineSegment(sketch, "E8.9.21.3", {"start": v(46.23, -0.38) * mm, "end": v(48.35, -2.5) * mm});
            skLineSegment(sketch, "E8.0.21.4", {"start": v(44.1, 2.5) * mm, "end": v(46.23, 4.62) * mm});
            skLineSegment(sketch, "E8.3.21.4", {"start": v(46.23, 0.38) * mm, "end": v(48.35, 2.5) * mm});
            skLineSegment(sketch, "E8.6.21.4", {"start": v(44.1, 2.5) * mm, "end": v(46.23, 0.38) * mm});
            skLineSegment(sketch, "E8.9.21.4", {"start": v(46.23, 4.62) * mm, "end": v(48.35, 2.5) * mm});
            skLineSegment(sketch, "E8.0.21.5", {"start": v(44.1, 7.5) * mm, "end": v(46.23, 9.62) * mm});
            skLineSegment(sketch, "E8.3.21.5", {"start": v(46.23, 5.38) * mm, "end": v(48.35, 7.5) * mm});
            skLineSegment(sketch, "E8.6.21.5", {"start": v(44.1, 7.5) * mm, "end": v(46.23, 5.38) * mm});
            skLineSegment(sketch, "E8.9.21.5", {"start": v(46.23, 9.62) * mm, "end": v(48.35, 7.5) * mm});
            skLineSegment(sketch, "E8.0.21.6", {"start": v(44.1, 12.5) * mm, "end": v(46.23, 14.62) * mm});
            skLineSegment(sketch, "E8.3.21.6", {"start": v(46.23, 10.38) * mm, "end": v(48.35, 12.5) * mm});
            skLineSegment(sketch, "E8.6.21.6", {"start": v(44.1, 12.5) * mm, "end": v(46.23, 10.38) * mm});
            skLineSegment(sketch, "E8.9.21.6", {"start": v(46.23, 14.62) * mm, "end": v(48.35, 12.5) * mm});
            skLineSegment(sketch, "E8.0.21.7", {"start": v(44.1, 17.5) * mm, "end": v(46.23, 19.62) * mm});
            skLineSegment(sketch, "E8.3.21.7", {"start": v(46.23, 15.38) * mm, "end": v(48.35, 17.5) * mm});
            skLineSegment(sketch, "E8.6.21.7", {"start": v(44.1, 17.5) * mm, "end": v(46.23, 15.38) * mm});
            skLineSegment(sketch, "E8.9.21.7", {"start": v(46.23, 19.62) * mm, "end": v(48.35, 17.5) * mm});
            skLineSegment(sketch, "E8.0.22.0", {"start": v(49.1, -17.5) * mm, "end": v(51.23, -15.38) * mm});
            skLineSegment(sketch, "E8.3.22.0", {"start": v(51.23, -19.62) * mm, "end": v(53.35, -17.5) * mm});
            skLineSegment(sketch, "E8.6.22.0", {"start": v(49.1, -17.5) * mm, "end": v(51.23, -19.62) * mm});
            skLineSegment(sketch, "E8.9.22.0", {"start": v(51.23, -15.38) * mm, "end": v(53.35, -17.5) * mm});
            skLineSegment(sketch, "E8.0.22.1", {"start": v(49.1, -12.5) * mm, "end": v(51.23, -10.38) * mm});
            skLineSegment(sketch, "E8.3.22.1", {"start": v(51.23, -14.62) * mm, "end": v(53.35, -12.5) * mm});
            skLineSegment(sketch, "E8.6.22.1", {"start": v(49.1, -12.5) * mm, "end": v(51.23, -14.62) * mm});
            skLineSegment(sketch, "E8.9.22.1", {"start": v(51.23, -10.38) * mm, "end": v(53.35, -12.5) * mm});
            skLineSegment(sketch, "E8.0.22.2", {"start": v(49.1, -7.5) * mm, "end": v(51.23, -5.38) * mm});
            skLineSegment(sketch, "E8.3.22.2", {"start": v(51.23, -9.62) * mm, "end": v(53.35, -7.5) * mm});
            skLineSegment(sketch, "E8.6.22.2", {"start": v(49.1, -7.5) * mm, "end": v(51.23, -9.62) * mm});
            skLineSegment(sketch, "E8.9.22.2", {"start": v(51.23, -5.38) * mm, "end": v(53.35, -7.5) * mm});
            skLineSegment(sketch, "E8.0.22.3", {"start": v(49.1, -2.5) * mm, "end": v(51.23, -0.38) * mm});
            skLineSegment(sketch, "E8.3.22.3", {"start": v(51.23, -4.62) * mm, "end": v(53.35, -2.5) * mm});
            skLineSegment(sketch, "E8.6.22.3", {"start": v(49.1, -2.5) * mm, "end": v(51.23, -4.62) * mm});
            skLineSegment(sketch, "E8.9.22.3", {"start": v(51.23, -0.38) * mm, "end": v(53.35, -2.5) * mm});
            skLineSegment(sketch, "E8.0.22.4", {"start": v(49.1, 2.5) * mm, "end": v(51.23, 4.62) * mm});
            skLineSegment(sketch, "E8.3.22.4", {"start": v(51.23, 0.38) * mm, "end": v(53.35, 2.5) * mm});
            skLineSegment(sketch, "E8.6.22.4", {"start": v(49.1, 2.5) * mm, "end": v(51.23, 0.38) * mm});
            skLineSegment(sketch, "E8.9.22.4", {"start": v(51.23, 4.62) * mm, "end": v(53.35, 2.5) * mm});
            skLineSegment(sketch, "E8.0.22.5", {"start": v(49.1, 7.5) * mm, "end": v(51.23, 9.62) * mm});
            skLineSegment(sketch, "E8.3.22.5", {"start": v(51.23, 5.38) * mm, "end": v(53.35, 7.5) * mm});
            skLineSegment(sketch, "E8.6.22.5", {"start": v(49.1, 7.5) * mm, "end": v(51.23, 5.38) * mm});
            skLineSegment(sketch, "E8.9.22.5", {"start": v(51.23, 9.62) * mm, "end": v(53.35, 7.5) * mm});
            skLineSegment(sketch, "E8.0.22.6", {"start": v(49.1, 12.5) * mm, "end": v(51.23, 14.62) * mm});
            skLineSegment(sketch, "E8.3.22.6", {"start": v(51.23, 10.38) * mm, "end": v(53.35, 12.5) * mm});
            skLineSegment(sketch, "E8.6.22.6", {"start": v(49.1, 12.5) * mm, "end": v(51.23, 10.38) * mm});
            skLineSegment(sketch, "E8.9.22.6", {"start": v(51.23, 14.62) * mm, "end": v(53.35, 12.5) * mm});
            skLineSegment(sketch, "E8.0.22.7", {"start": v(49.1, 17.5) * mm, "end": v(51.23, 19.62) * mm});
            skLineSegment(sketch, "E8.3.22.7", {"start": v(51.23, 15.38) * mm, "end": v(53.35, 17.5) * mm});
            skLineSegment(sketch, "E8.6.22.7", {"start": v(49.1, 17.5) * mm, "end": v(51.23, 15.38) * mm});
            skLineSegment(sketch, "E8.9.22.7", {"start": v(51.23, 19.62) * mm, "end": v(53.35, 17.5) * mm});
            skLineSegment(sketch, "E8.0.23.0", {"start": v(54.1, -17.5) * mm, "end": v(56.23, -15.38) * mm});
            skLineSegment(sketch, "E8.3.23.0", {"start": v(56.23, -19.62) * mm, "end": v(58.35, -17.5) * mm});
            skLineSegment(sketch, "E8.6.23.0", {"start": v(54.1, -17.5) * mm, "end": v(56.23, -19.62) * mm});
            skLineSegment(sketch, "E8.9.23.0", {"start": v(56.23, -15.38) * mm, "end": v(58.35, -17.5) * mm});
            skLineSegment(sketch, "E8.0.23.1", {"start": v(54.1, -12.5) * mm, "end": v(56.23, -10.38) * mm});
            skLineSegment(sketch, "E8.3.23.1", {"start": v(56.23, -14.62) * mm, "end": v(58.35, -12.5) * mm});
            skLineSegment(sketch, "E8.6.23.1", {"start": v(54.1, -12.5) * mm, "end": v(56.23, -14.62) * mm});
            skLineSegment(sketch, "E8.9.23.1", {"start": v(56.23, -10.38) * mm, "end": v(58.35, -12.5) * mm});
            skLineSegment(sketch, "E8.0.23.2", {"start": v(54.1, -7.5) * mm, "end": v(56.23, -5.38) * mm});
            skLineSegment(sketch, "E8.3.23.2", {"start": v(56.23, -9.62) * mm, "end": v(58.35, -7.5) * mm});
            skLineSegment(sketch, "E8.6.23.2", {"start": v(54.1, -7.5) * mm, "end": v(56.23, -9.62) * mm});
            skLineSegment(sketch, "E8.9.23.2", {"start": v(56.23, -5.38) * mm, "end": v(58.35, -7.5) * mm});
            skLineSegment(sketch, "E8.0.23.3", {"start": v(54.1, -2.5) * mm, "end": v(56.23, -0.38) * mm});
            skLineSegment(sketch, "E8.3.23.3", {"start": v(56.23, -4.62) * mm, "end": v(58.35, -2.5) * mm});
            skLineSegment(sketch, "E8.6.23.3", {"start": v(54.1, -2.5) * mm, "end": v(56.23, -4.62) * mm});
            skLineSegment(sketch, "E8.9.23.3", {"start": v(56.23, -0.38) * mm, "end": v(58.35, -2.5) * mm});
            skLineSegment(sketch, "E8.0.23.4", {"start": v(54.1, 2.5) * mm, "end": v(56.23, 4.62) * mm});
            skLineSegment(sketch, "E8.3.23.4", {"start": v(56.23, 0.38) * mm, "end": v(58.35, 2.5) * mm});
            skLineSegment(sketch, "E8.6.23.4", {"start": v(54.1, 2.5) * mm, "end": v(56.23, 0.38) * mm});
            skLineSegment(sketch, "E8.9.23.4", {"start": v(56.23, 4.62) * mm, "end": v(58.35, 2.5) * mm});
            skLineSegment(sketch, "E8.0.23.5", {"start": v(54.1, 7.5) * mm, "end": v(56.23, 9.62) * mm});
            skLineSegment(sketch, "E8.3.23.5", {"start": v(56.23, 5.38) * mm, "end": v(58.35, 7.5) * mm});
            skLineSegment(sketch, "E8.6.23.5", {"start": v(54.1, 7.5) * mm, "end": v(56.23, 5.38) * mm});
            skLineSegment(sketch, "E8.9.23.5", {"start": v(56.23, 9.62) * mm, "end": v(58.35, 7.5) * mm});
            skLineSegment(sketch, "E8.0.23.6", {"start": v(54.1, 12.5) * mm, "end": v(56.23, 14.62) * mm});
            skLineSegment(sketch, "E8.3.23.6", {"start": v(56.23, 10.38) * mm, "end": v(58.35, 12.5) * mm});
            skLineSegment(sketch, "E8.6.23.6", {"start": v(54.1, 12.5) * mm, "end": v(56.23, 10.38) * mm});
            skLineSegment(sketch, "E8.9.23.6", {"start": v(56.23, 14.62) * mm, "end": v(58.35, 12.5) * mm});
            skLineSegment(sketch, "E8.0.23.7", {"start": v(54.1, 17.5) * mm, "end": v(56.23, 19.62) * mm});
            skLineSegment(sketch, "E8.3.23.7", {"start": v(56.23, 15.38) * mm, "end": v(58.35, 17.5) * mm});
            skLineSegment(sketch, "E8.6.23.7", {"start": v(54.1, 17.5) * mm, "end": v(56.23, 15.38) * mm});
            skLineSegment(sketch, "E8.9.23.7", {"start": v(56.23, 19.62) * mm, "end": v(58.35, 17.5) * mm});
            skLineSegment(sketch, "E9.0.7.0", {"start": v(-23.4, -15) * mm, "end": v(-21.27, -12.88) * mm});
            skLineSegment(sketch, "E9.3.7.0", {"start": v(-21.27, -12.88) * mm, "end": v(-19.15, -15) * mm});
            skLineSegment(sketch, "E9.6.7.0", {"start": v(-21.27, -17.12) * mm, "end": v(-19.15, -15) * mm});
            skLineSegment(sketch, "E9.9.7.0", {"start": v(-23.4, -15) * mm, "end": v(-21.27, -17.12) * mm});
            skLineSegment(sketch, "E9.0.7.1", {"start": v(-23.4, -10) * mm, "end": v(-21.27, -7.88) * mm});
            skLineSegment(sketch, "E9.3.7.1", {"start": v(-21.27, -7.88) * mm, "end": v(-19.15, -10) * mm});
            skLineSegment(sketch, "E9.6.7.1", {"start": v(-21.27, -12.12) * mm, "end": v(-19.15, -10) * mm});
            skLineSegment(sketch, "E9.9.7.1", {"start": v(-23.4, -10) * mm, "end": v(-21.27, -12.12) * mm});
            skLineSegment(sketch, "E9.0.7.2", {"start": v(-23.4, -5) * mm, "end": v(-21.27, -2.88) * mm});
            skLineSegment(sketch, "E9.3.7.2", {"start": v(-21.27, -2.88) * mm, "end": v(-19.15, -5) * mm});
            skLineSegment(sketch, "E9.6.7.2", {"start": v(-21.27, -7.12) * mm, "end": v(-19.15, -5) * mm});
            skLineSegment(sketch, "E9.9.7.2", {"start": v(-23.4, -5) * mm, "end": v(-21.27, -7.12) * mm});
            skLineSegment(sketch, "E9.0.7.3", {"start": v(-23.4, 0) * mm, "end": v(-21.27, 2.12) * mm});
            skLineSegment(sketch, "E9.3.7.3", {"start": v(-21.27, 2.12) * mm, "end": v(-19.15, 0) * mm});
            skLineSegment(sketch, "E9.6.7.3", {"start": v(-21.27, -2.12) * mm, "end": v(-19.15, 0) * mm});
            skLineSegment(sketch, "E9.9.7.3", {"start": v(-23.4, 0) * mm, "end": v(-21.27, -2.12) * mm});
            skLineSegment(sketch, "E9.0.7.4", {"start": v(-23.4, 5) * mm, "end": v(-21.27, 7.12) * mm});
            skLineSegment(sketch, "E9.3.7.4", {"start": v(-21.27, 7.12) * mm, "end": v(-19.15, 5) * mm});
            skLineSegment(sketch, "E9.6.7.4", {"start": v(-21.27, 2.88) * mm, "end": v(-19.15, 5) * mm});
            skLineSegment(sketch, "E9.9.7.4", {"start": v(-23.4, 5) * mm, "end": v(-21.27, 2.88) * mm});
            skLineSegment(sketch, "E9.0.7.5", {"start": v(-23.4, 10) * mm, "end": v(-21.27, 12.12) * mm});
            skLineSegment(sketch, "E9.3.7.5", {"start": v(-21.27, 12.12) * mm, "end": v(-19.15, 10) * mm});
            skLineSegment(sketch, "E9.6.7.5", {"start": v(-21.27, 7.88) * mm, "end": v(-19.15, 10) * mm});
            skLineSegment(sketch, "E9.9.7.5", {"start": v(-23.4, 10) * mm, "end": v(-21.27, 7.88) * mm});
            skLineSegment(sketch, "E9.0.7.6", {"start": v(-23.4, 15) * mm, "end": v(-21.27, 17.12) * mm});
            skLineSegment(sketch, "E9.3.7.6", {"start": v(-21.27, 17.12) * mm, "end": v(-19.15, 15) * mm});
            skLineSegment(sketch, "E9.6.7.6", {"start": v(-21.27, 12.88) * mm, "end": v(-19.15, 15) * mm});
            skLineSegment(sketch, "E9.9.7.6", {"start": v(-23.4, 15) * mm, "end": v(-21.27, 12.88) * mm});
            skLineSegment(sketch, "E9.0.8.0", {"start": v(-18.4, -15) * mm, "end": v(-16.27, -12.88) * mm});
            skLineSegment(sketch, "E9.3.8.0", {"start": v(-16.27, -12.88) * mm, "end": v(-14.15, -15) * mm});
            skLineSegment(sketch, "E9.6.8.0", {"start": v(-16.27, -17.12) * mm, "end": v(-14.15, -15) * mm});
            skLineSegment(sketch, "E9.9.8.0", {"start": v(-18.4, -15) * mm, "end": v(-16.27, -17.12) * mm});
            skLineSegment(sketch, "E9.0.8.1", {"start": v(-18.4, -10) * mm, "end": v(-16.27, -7.88) * mm});
            skLineSegment(sketch, "E9.3.8.1", {"start": v(-16.27, -7.88) * mm, "end": v(-14.15, -10) * mm});
            skLineSegment(sketch, "E9.6.8.1", {"start": v(-16.27, -12.12) * mm, "end": v(-14.15, -10) * mm});
            skLineSegment(sketch, "E9.9.8.1", {"start": v(-18.4, -10) * mm, "end": v(-16.27, -12.12) * mm});
            skLineSegment(sketch, "E9.0.8.2", {"start": v(-18.4, -5) * mm, "end": v(-16.27, -2.88) * mm});
            skLineSegment(sketch, "E9.3.8.2", {"start": v(-16.27, -2.88) * mm, "end": v(-14.15, -5) * mm});
            skLineSegment(sketch, "E9.6.8.2", {"start": v(-16.27, -7.12) * mm, "end": v(-14.15, -5) * mm});
            skLineSegment(sketch, "E9.9.8.2", {"start": v(-18.4, -5) * mm, "end": v(-16.27, -7.12) * mm});
            skLineSegment(sketch, "E9.0.8.3", {"start": v(-18.4, 0) * mm, "end": v(-16.27, 2.12) * mm});
            skLineSegment(sketch, "E9.3.8.3", {"start": v(-16.27, 2.12) * mm, "end": v(-14.15, 0) * mm});
            skLineSegment(sketch, "E9.6.8.3", {"start": v(-16.27, -2.12) * mm, "end": v(-14.15, 0) * mm});
            skLineSegment(sketch, "E9.9.8.3", {"start": v(-18.4, 0) * mm, "end": v(-16.27, -2.12) * mm});
            skLineSegment(sketch, "E9.0.8.4", {"start": v(-18.4, 5) * mm, "end": v(-16.27, 7.12) * mm});
            skLineSegment(sketch, "E9.3.8.4", {"start": v(-16.27, 7.12) * mm, "end": v(-14.15, 5) * mm});
            skLineSegment(sketch, "E9.6.8.4", {"start": v(-16.27, 2.88) * mm, "end": v(-14.15, 5) * mm});
            skLineSegment(sketch, "E9.9.8.4", {"start": v(-18.4, 5) * mm, "end": v(-16.27, 2.88) * mm});
            skLineSegment(sketch, "E9.0.8.5", {"start": v(-18.4, 10) * mm, "end": v(-16.27, 12.12) * mm});
            skLineSegment(sketch, "E9.3.8.5", {"start": v(-16.27, 12.12) * mm, "end": v(-14.15, 10) * mm});
            skLineSegment(sketch, "E9.6.8.5", {"start": v(-16.27, 7.88) * mm, "end": v(-14.15, 10) * mm});
            skLineSegment(sketch, "E9.9.8.5", {"start": v(-18.4, 10) * mm, "end": v(-16.27, 7.88) * mm});
            skLineSegment(sketch, "E9.0.8.6", {"start": v(-18.4, 15) * mm, "end": v(-16.27, 17.12) * mm});
            skLineSegment(sketch, "E9.3.8.6", {"start": v(-16.27, 17.12) * mm, "end": v(-14.15, 15) * mm});
            skLineSegment(sketch, "E9.6.8.6", {"start": v(-16.27, 12.88) * mm, "end": v(-14.15, 15) * mm});
            skLineSegment(sketch, "E9.9.8.6", {"start": v(-18.4, 15) * mm, "end": v(-16.27, 12.88) * mm});
            skLineSegment(sketch, "E9.0.9.0", {"start": v(-13.4, -15) * mm, "end": v(-11.27, -12.88) * mm});
            skLineSegment(sketch, "E9.3.9.0", {"start": v(-11.27, -12.88) * mm, "end": v(-9.15, -15) * mm});
            skLineSegment(sketch, "E9.6.9.0", {"start": v(-11.27, -17.12) * mm, "end": v(-9.15, -15) * mm});
            skLineSegment(sketch, "E9.9.9.0", {"start": v(-13.4, -15) * mm, "end": v(-11.27, -17.12) * mm});
            skLineSegment(sketch, "E9.0.9.1", {"start": v(-13.4, -10) * mm, "end": v(-11.27, -7.88) * mm});
            skLineSegment(sketch, "E9.3.9.1", {"start": v(-11.27, -7.88) * mm, "end": v(-9.15, -10) * mm});
            skLineSegment(sketch, "E9.6.9.1", {"start": v(-11.27, -12.12) * mm, "end": v(-9.15, -10) * mm});
            skLineSegment(sketch, "E9.9.9.1", {"start": v(-13.4, -10) * mm, "end": v(-11.27, -12.12) * mm});
            skLineSegment(sketch, "E9.0.9.2", {"start": v(-13.4, -5) * mm, "end": v(-11.27, -2.88) * mm});
            skLineSegment(sketch, "E9.3.9.2", {"start": v(-11.27, -2.88) * mm, "end": v(-9.15, -5) * mm});
            skLineSegment(sketch, "E9.6.9.2", {"start": v(-11.27, -7.12) * mm, "end": v(-9.15, -5) * mm});
            skLineSegment(sketch, "E9.9.9.2", {"start": v(-13.4, -5) * mm, "end": v(-11.27, -7.12) * mm});
            skLineSegment(sketch, "E9.0.9.3", {"start": v(-13.4, 0) * mm, "end": v(-11.27, 2.12) * mm});
            skLineSegment(sketch, "E9.3.9.3", {"start": v(-11.27, 2.12) * mm, "end": v(-9.15, 0) * mm});
            skLineSegment(sketch, "E9.6.9.3", {"start": v(-11.27, -2.12) * mm, "end": v(-9.15, 0) * mm});
            skLineSegment(sketch, "E9.9.9.3", {"start": v(-13.4, 0) * mm, "end": v(-11.27, -2.12) * mm});
            skLineSegment(sketch, "E9.0.9.4", {"start": v(-13.4, 5) * mm, "end": v(-11.27, 7.12) * mm});
            skLineSegment(sketch, "E9.3.9.4", {"start": v(-11.27, 7.12) * mm, "end": v(-9.15, 5) * mm});
            skLineSegment(sketch, "E9.6.9.4", {"start": v(-11.27, 2.88) * mm, "end": v(-9.15, 5) * mm});
            skLineSegment(sketch, "E9.9.9.4", {"start": v(-13.4, 5) * mm, "end": v(-11.27, 2.88) * mm});
            skLineSegment(sketch, "E9.0.9.5", {"start": v(-13.4, 10) * mm, "end": v(-11.27, 12.12) * mm});
            skLineSegment(sketch, "E9.3.9.5", {"start": v(-11.27, 12.12) * mm, "end": v(-9.15, 10) * mm});
            skLineSegment(sketch, "E9.6.9.5", {"start": v(-11.27, 7.88) * mm, "end": v(-9.15, 10) * mm});
            skLineSegment(sketch, "E9.9.9.5", {"start": v(-13.4, 10) * mm, "end": v(-11.27, 7.88) * mm});
            skLineSegment(sketch, "E9.0.9.6", {"start": v(-13.4, 15) * mm, "end": v(-11.27, 17.12) * mm});
            skLineSegment(sketch, "E9.3.9.6", {"start": v(-11.27, 17.12) * mm, "end": v(-9.15, 15) * mm});
            skLineSegment(sketch, "E9.6.9.6", {"start": v(-11.27, 12.88) * mm, "end": v(-9.15, 15) * mm});
            skLineSegment(sketch, "E9.9.9.6", {"start": v(-13.4, 15) * mm, "end": v(-11.27, 12.88) * mm});
            skLineSegment(sketch, "E9.0.10.0", {"start": v(-8.4, -15) * mm, "end": v(-6.27, -12.88) * mm});
            skLineSegment(sketch, "E9.3.10.0", {"start": v(-6.27, -12.88) * mm, "end": v(-4.15, -15) * mm});
            skLineSegment(sketch, "E9.6.10.0", {"start": v(-6.27, -17.12) * mm, "end": v(-4.15, -15) * mm});
            skLineSegment(sketch, "E9.9.10.0", {"start": v(-8.4, -15) * mm, "end": v(-6.27, -17.12) * mm});
            skLineSegment(sketch, "E9.0.10.1", {"start": v(-8.4, -10) * mm, "end": v(-6.27, -7.88) * mm});
            skLineSegment(sketch, "E9.3.10.1", {"start": v(-6.27, -7.88) * mm, "end": v(-4.15, -10) * mm});
            skLineSegment(sketch, "E9.6.10.1", {"start": v(-6.27, -12.12) * mm, "end": v(-4.15, -10) * mm});
            skLineSegment(sketch, "E9.9.10.1", {"start": v(-8.4, -10) * mm, "end": v(-6.27, -12.12) * mm});
            skLineSegment(sketch, "E9.0.10.2", {"start": v(-8.4, -5) * mm, "end": v(-6.27, -2.88) * mm});
            skLineSegment(sketch, "E9.3.10.2", {"start": v(-6.27, -2.88) * mm, "end": v(-4.15, -5) * mm});
            skLineSegment(sketch, "E9.6.10.2", {"start": v(-6.27, -7.12) * mm, "end": v(-4.15, -5) * mm});
            skLineSegment(sketch, "E9.9.10.2", {"start": v(-8.4, -5) * mm, "end": v(-6.27, -7.12) * mm});
            skLineSegment(sketch, "E9.0.10.3", {"start": v(-8.4, 0) * mm, "end": v(-6.27, 2.12) * mm});
            skLineSegment(sketch, "E9.3.10.3", {"start": v(-6.27, 2.12) * mm, "end": v(-4.15, 0) * mm});
            skLineSegment(sketch, "E9.6.10.3", {"start": v(-6.27, -2.12) * mm, "end": v(-4.15, 0) * mm});
            skLineSegment(sketch, "E9.9.10.3", {"start": v(-8.4, 0) * mm, "end": v(-6.27, -2.12) * mm});
            skLineSegment(sketch, "E9.0.10.4", {"start": v(-8.4, 5) * mm, "end": v(-6.27, 7.12) * mm});
            skLineSegment(sketch, "E9.3.10.4", {"start": v(-6.27, 7.12) * mm, "end": v(-4.15, 5) * mm});
            skLineSegment(sketch, "E9.6.10.4", {"start": v(-6.27, 2.88) * mm, "end": v(-4.15, 5) * mm});
            skLineSegment(sketch, "E9.9.10.4", {"start": v(-8.4, 5) * mm, "end": v(-6.27, 2.88) * mm});
            skLineSegment(sketch, "E9.0.10.5", {"start": v(-8.4, 10) * mm, "end": v(-6.27, 12.12) * mm});
            skLineSegment(sketch, "E9.3.10.5", {"start": v(-6.27, 12.12) * mm, "end": v(-4.15, 10) * mm});
            skLineSegment(sketch, "E9.6.10.5", {"start": v(-6.27, 7.88) * mm, "end": v(-4.15, 10) * mm});
            skLineSegment(sketch, "E9.9.10.5", {"start": v(-8.4, 10) * mm, "end": v(-6.27, 7.88) * mm});
            skLineSegment(sketch, "E9.0.10.6", {"start": v(-8.4, 15) * mm, "end": v(-6.27, 17.12) * mm});
            skLineSegment(sketch, "E9.3.10.6", {"start": v(-6.27, 17.12) * mm, "end": v(-4.15, 15) * mm});
            skLineSegment(sketch, "E9.6.10.6", {"start": v(-6.27, 12.88) * mm, "end": v(-4.15, 15) * mm});
            skLineSegment(sketch, "E9.9.10.6", {"start": v(-8.4, 15) * mm, "end": v(-6.27, 12.88) * mm});
            skLineSegment(sketch, "E9.0.11.0", {"start": v(-3.4, -15) * mm, "end": v(-1.27, -12.88) * mm});
            skLineSegment(sketch, "E9.3.11.0", {"start": v(-1.27, -12.88) * mm, "end": v(0.85, -15) * mm});
            skLineSegment(sketch, "E9.6.11.0", {"start": v(-1.27, -17.12) * mm, "end": v(0.85, -15) * mm});
            skLineSegment(sketch, "E9.9.11.0", {"start": v(-3.4, -15) * mm, "end": v(-1.27, -17.12) * mm});
            skLineSegment(sketch, "E9.0.11.1", {"start": v(-3.4, -10) * mm, "end": v(-1.27, -7.88) * mm});
            skLineSegment(sketch, "E9.3.11.1", {"start": v(-1.27, -7.88) * mm, "end": v(0.85, -10) * mm});
            skLineSegment(sketch, "E9.6.11.1", {"start": v(-1.27, -12.12) * mm, "end": v(0.85, -10) * mm});
            skLineSegment(sketch, "E9.9.11.1", {"start": v(-3.4, -10) * mm, "end": v(-1.27, -12.12) * mm});
            skLineSegment(sketch, "E9.0.11.2", {"start": v(-3.4, -5) * mm, "end": v(-1.27, -2.88) * mm});
            skLineSegment(sketch, "E9.3.11.2", {"start": v(-1.27, -2.88) * mm, "end": v(0.85, -5) * mm});
            skLineSegment(sketch, "E9.6.11.2", {"start": v(-1.27, -7.12) * mm, "end": v(0.85, -5) * mm});
            skLineSegment(sketch, "E9.9.11.2", {"start": v(-3.4, -5) * mm, "end": v(-1.27, -7.12) * mm});
            skLineSegment(sketch, "E9.0.11.3", {"start": v(-3.4, 0) * mm, "end": v(-1.27, 2.12) * mm});
            skLineSegment(sketch, "E9.3.11.3", {"start": v(-1.27, 2.12) * mm, "end": v(0.85, 0) * mm});
            skLineSegment(sketch, "E9.6.11.3", {"start": v(-1.27, -2.12) * mm, "end": v(0.85, 0) * mm});
            skLineSegment(sketch, "E9.9.11.3", {"start": v(-3.4, 0) * mm, "end": v(-1.27, -2.12) * mm});
            skLineSegment(sketch, "E9.0.11.4", {"start": v(-3.4, 5) * mm, "end": v(-1.27, 7.12) * mm});
            skLineSegment(sketch, "E9.3.11.4", {"start": v(-1.27, 7.12) * mm, "end": v(0.85, 5) * mm});
            skLineSegment(sketch, "E9.6.11.4", {"start": v(-1.27, 2.88) * mm, "end": v(0.85, 5) * mm});
            skLineSegment(sketch, "E9.9.11.4", {"start": v(-3.4, 5) * mm, "end": v(-1.27, 2.88) * mm});
            skLineSegment(sketch, "E9.0.11.5", {"start": v(-3.4, 10) * mm, "end": v(-1.27, 12.12) * mm});
            skLineSegment(sketch, "E9.3.11.5", {"start": v(-1.27, 12.12) * mm, "end": v(0.85, 10) * mm});
            skLineSegment(sketch, "E9.6.11.5", {"start": v(-1.27, 7.88) * mm, "end": v(0.85, 10) * mm});
            skLineSegment(sketch, "E9.9.11.5", {"start": v(-3.4, 10) * mm, "end": v(-1.27, 7.88) * mm});
            skLineSegment(sketch, "E9.0.11.6", {"start": v(-3.4, 15) * mm, "end": v(-1.27, 17.12) * mm});
            skLineSegment(sketch, "E9.3.11.6", {"start": v(-1.27, 17.12) * mm, "end": v(0.85, 15) * mm});
            skLineSegment(sketch, "E9.6.11.6", {"start": v(-1.27, 12.88) * mm, "end": v(0.85, 15) * mm});
            skLineSegment(sketch, "E9.9.11.6", {"start": v(-3.4, 15) * mm, "end": v(-1.27, 12.88) * mm});
            skLineSegment(sketch, "E9.0.12.0", {"start": v(1.6, -15) * mm, "end": v(3.73, -12.88) * mm});
            skLineSegment(sketch, "E9.3.12.0", {"start": v(3.73, -12.88) * mm, "end": v(5.85, -15) * mm});
            skLineSegment(sketch, "E9.6.12.0", {"start": v(3.73, -17.12) * mm, "end": v(5.85, -15) * mm});
            skLineSegment(sketch, "E9.9.12.0", {"start": v(1.6, -15) * mm, "end": v(3.73, -17.12) * mm});
            skLineSegment(sketch, "E9.0.12.1", {"start": v(1.6, -10) * mm, "end": v(3.73, -7.88) * mm});
            skLineSegment(sketch, "E9.3.12.1", {"start": v(3.73, -7.88) * mm, "end": v(5.85, -10) * mm});
            skLineSegment(sketch, "E9.6.12.1", {"start": v(3.73, -12.12) * mm, "end": v(5.85, -10) * mm});
            skLineSegment(sketch, "E9.9.12.1", {"start": v(1.6, -10) * mm, "end": v(3.73, -12.12) * mm});
            skLineSegment(sketch, "E9.0.12.2", {"start": v(1.6, -5) * mm, "end": v(3.73, -2.88) * mm});
            skLineSegment(sketch, "E9.3.12.2", {"start": v(3.73, -2.88) * mm, "end": v(5.85, -5) * mm});
            skLineSegment(sketch, "E9.6.12.2", {"start": v(3.73, -7.12) * mm, "end": v(5.85, -5) * mm});
            skLineSegment(sketch, "E9.9.12.2", {"start": v(1.6, -5) * mm, "end": v(3.73, -7.12) * mm});
            skLineSegment(sketch, "E9.0.12.3", {"start": v(1.6, 0) * mm, "end": v(3.73, 2.12) * mm});
            skLineSegment(sketch, "E9.3.12.3", {"start": v(3.73, 2.12) * mm, "end": v(5.85, 0) * mm});
            skLineSegment(sketch, "E9.6.12.3", {"start": v(3.73, -2.12) * mm, "end": v(5.85, 0) * mm});
            skLineSegment(sketch, "E9.9.12.3", {"start": v(1.6, 0) * mm, "end": v(3.73, -2.12) * mm});
            skLineSegment(sketch, "E9.0.12.4", {"start": v(1.6, 5) * mm, "end": v(3.73, 7.12) * mm});
            skLineSegment(sketch, "E9.3.12.4", {"start": v(3.73, 7.12) * mm, "end": v(5.85, 5) * mm});
            skLineSegment(sketch, "E9.6.12.4", {"start": v(3.73, 2.88) * mm, "end": v(5.85, 5) * mm});
            skLineSegment(sketch, "E9.9.12.4", {"start": v(1.6, 5) * mm, "end": v(3.73, 2.88) * mm});
            skLineSegment(sketch, "E9.0.12.5", {"start": v(1.6, 10) * mm, "end": v(3.73, 12.12) * mm});
            skLineSegment(sketch, "E9.3.12.5", {"start": v(3.73, 12.12) * mm, "end": v(5.85, 10) * mm});
            skLineSegment(sketch, "E9.6.12.5", {"start": v(3.73, 7.88) * mm, "end": v(5.85, 10) * mm});
            skLineSegment(sketch, "E9.9.12.5", {"start": v(1.6, 10) * mm, "end": v(3.73, 7.88) * mm});
            skLineSegment(sketch, "E9.0.12.6", {"start": v(1.6, 15) * mm, "end": v(3.73, 17.12) * mm});
            skLineSegment(sketch, "E9.3.12.6", {"start": v(3.73, 17.12) * mm, "end": v(5.85, 15) * mm});
            skLineSegment(sketch, "E9.6.12.6", {"start": v(3.73, 12.88) * mm, "end": v(5.85, 15) * mm});
            skLineSegment(sketch, "E9.9.12.6", {"start": v(1.6, 15) * mm, "end": v(3.73, 12.88) * mm});
            skLineSegment(sketch, "E9.0.13.0", {"start": v(6.6, -15) * mm, "end": v(8.73, -12.88) * mm});
            skLineSegment(sketch, "E9.3.13.0", {"start": v(8.73, -12.88) * mm, "end": v(10.85, -15) * mm});
            skLineSegment(sketch, "E9.6.13.0", {"start": v(8.73, -17.12) * mm, "end": v(10.85, -15) * mm});
            skLineSegment(sketch, "E9.9.13.0", {"start": v(6.6, -15) * mm, "end": v(8.73, -17.12) * mm});
            skLineSegment(sketch, "E9.0.13.1", {"start": v(6.6, -10) * mm, "end": v(8.73, -7.88) * mm});
            skLineSegment(sketch, "E9.3.13.1", {"start": v(8.73, -7.88) * mm, "end": v(10.85, -10) * mm});
            skLineSegment(sketch, "E9.6.13.1", {"start": v(8.73, -12.12) * mm, "end": v(10.85, -10) * mm});
            skLineSegment(sketch, "E9.9.13.1", {"start": v(6.6, -10) * mm, "end": v(8.73, -12.12) * mm});
            skLineSegment(sketch, "E9.0.13.2", {"start": v(6.6, -5) * mm, "end": v(8.73, -2.88) * mm});
            skLineSegment(sketch, "E9.3.13.2", {"start": v(8.73, -2.88) * mm, "end": v(10.85, -5) * mm});
            skLineSegment(sketch, "E9.6.13.2", {"start": v(8.73, -7.12) * mm, "end": v(10.85, -5) * mm});
            skLineSegment(sketch, "E9.9.13.2", {"start": v(6.6, -5) * mm, "end": v(8.73, -7.12) * mm});
            skLineSegment(sketch, "E9.0.13.3", {"start": v(6.6, 0) * mm, "end": v(8.73, 2.12) * mm});
            skLineSegment(sketch, "E9.3.13.3", {"start": v(8.73, 2.12) * mm, "end": v(10.85, 0) * mm});
            skLineSegment(sketch, "E9.6.13.3", {"start": v(8.73, -2.12) * mm, "end": v(10.85, 0) * mm});
            skLineSegment(sketch, "E9.9.13.3", {"start": v(6.6, 0) * mm, "end": v(8.73, -2.12) * mm});
            skLineSegment(sketch, "E9.0.13.4", {"start": v(6.6, 5) * mm, "end": v(8.73, 7.12) * mm});
            skLineSegment(sketch, "E9.3.13.4", {"start": v(8.73, 7.12) * mm, "end": v(10.85, 5) * mm});
            skLineSegment(sketch, "E9.6.13.4", {"start": v(8.73, 2.88) * mm, "end": v(10.85, 5) * mm});
            skLineSegment(sketch, "E9.9.13.4", {"start": v(6.6, 5) * mm, "end": v(8.73, 2.88) * mm});
            skLineSegment(sketch, "E9.0.13.5", {"start": v(6.6, 10) * mm, "end": v(8.73, 12.12) * mm});
            skLineSegment(sketch, "E9.3.13.5", {"start": v(8.73, 12.12) * mm, "end": v(10.85, 10) * mm});
            skLineSegment(sketch, "E9.6.13.5", {"start": v(8.73, 7.88) * mm, "end": v(10.85, 10) * mm});
            skLineSegment(sketch, "E9.9.13.5", {"start": v(6.6, 10) * mm, "end": v(8.73, 7.88) * mm});
            skLineSegment(sketch, "E9.0.13.6", {"start": v(6.6, 15) * mm, "end": v(8.73, 17.12) * mm});
            skLineSegment(sketch, "E9.3.13.6", {"start": v(8.73, 17.12) * mm, "end": v(10.85, 15) * mm});
            skLineSegment(sketch, "E9.6.13.6", {"start": v(8.73, 12.88) * mm, "end": v(10.85, 15) * mm});
            skLineSegment(sketch, "E9.9.13.6", {"start": v(6.6, 15) * mm, "end": v(8.73, 12.88) * mm});
            skLineSegment(sketch, "E9.0.14.0", {"start": v(11.6, -15) * mm, "end": v(13.73, -12.88) * mm});
            skLineSegment(sketch, "E9.3.14.0", {"start": v(13.73, -12.88) * mm, "end": v(15.85, -15) * mm});
            skLineSegment(sketch, "E9.6.14.0", {"start": v(13.73, -17.12) * mm, "end": v(15.85, -15) * mm});
            skLineSegment(sketch, "E9.9.14.0", {"start": v(11.6, -15) * mm, "end": v(13.73, -17.12) * mm});
            skLineSegment(sketch, "E9.0.14.1", {"start": v(11.6, -10) * mm, "end": v(13.73, -7.88) * mm});
            skLineSegment(sketch, "E9.3.14.1", {"start": v(13.73, -7.88) * mm, "end": v(15.85, -10) * mm});
            skLineSegment(sketch, "E9.6.14.1", {"start": v(13.73, -12.12) * mm, "end": v(15.85, -10) * mm});
            skLineSegment(sketch, "E9.9.14.1", {"start": v(11.6, -10) * mm, "end": v(13.73, -12.12) * mm});
            skLineSegment(sketch, "E9.0.14.2", {"start": v(11.6, -5) * mm, "end": v(13.73, -2.88) * mm});
            skLineSegment(sketch, "E9.3.14.2", {"start": v(13.73, -2.88) * mm, "end": v(15.85, -5) * mm});
            skLineSegment(sketch, "E9.6.14.2", {"start": v(13.73, -7.12) * mm, "end": v(15.85, -5) * mm});
            skLineSegment(sketch, "E9.9.14.2", {"start": v(11.6, -5) * mm, "end": v(13.73, -7.12) * mm});
            skLineSegment(sketch, "E9.0.14.3", {"start": v(11.6, 0) * mm, "end": v(13.73, 2.12) * mm});
            skLineSegment(sketch, "E9.3.14.3", {"start": v(13.73, 2.12) * mm, "end": v(15.85, 0) * mm});
            skLineSegment(sketch, "E9.6.14.3", {"start": v(13.73, -2.12) * mm, "end": v(15.85, 0) * mm});
            skLineSegment(sketch, "E9.9.14.3", {"start": v(11.6, 0) * mm, "end": v(13.73, -2.12) * mm});
            skLineSegment(sketch, "E9.0.14.4", {"start": v(11.6, 5) * mm, "end": v(13.73, 7.12) * mm});
            skLineSegment(sketch, "E9.3.14.4", {"start": v(13.73, 7.12) * mm, "end": v(15.85, 5) * mm});
            skLineSegment(sketch, "E9.6.14.4", {"start": v(13.73, 2.88) * mm, "end": v(15.85, 5) * mm});
            skLineSegment(sketch, "E9.9.14.4", {"start": v(11.6, 5) * mm, "end": v(13.73, 2.88) * mm});
            skLineSegment(sketch, "E9.0.14.5", {"start": v(11.6, 10) * mm, "end": v(13.73, 12.12) * mm});
            skLineSegment(sketch, "E9.3.14.5", {"start": v(13.73, 12.12) * mm, "end": v(15.85, 10) * mm});
            skLineSegment(sketch, "E9.6.14.5", {"start": v(13.73, 7.88) * mm, "end": v(15.85, 10) * mm});
            skLineSegment(sketch, "E9.9.14.5", {"start": v(11.6, 10) * mm, "end": v(13.73, 7.88) * mm});
            skLineSegment(sketch, "E9.0.14.6", {"start": v(11.6, 15) * mm, "end": v(13.73, 17.12) * mm});
            skLineSegment(sketch, "E9.3.14.6", {"start": v(13.73, 17.12) * mm, "end": v(15.85, 15) * mm});
            skLineSegment(sketch, "E9.6.14.6", {"start": v(13.73, 12.88) * mm, "end": v(15.85, 15) * mm});
            skLineSegment(sketch, "E9.9.14.6", {"start": v(11.6, 15) * mm, "end": v(13.73, 12.88) * mm});
            skLineSegment(sketch, "E9.0.15.0", {"start": v(16.6, -15) * mm, "end": v(18.73, -12.88) * mm});
            skLineSegment(sketch, "E9.3.15.0", {"start": v(18.73, -12.88) * mm, "end": v(20.85, -15) * mm});
            skLineSegment(sketch, "E9.6.15.0", {"start": v(18.73, -17.12) * mm, "end": v(20.85, -15) * mm});
            skLineSegment(sketch, "E9.9.15.0", {"start": v(16.6, -15) * mm, "end": v(18.73, -17.12) * mm});
            skLineSegment(sketch, "E9.0.15.1", {"start": v(16.6, -10) * mm, "end": v(18.73, -7.88) * mm});
            skLineSegment(sketch, "E9.3.15.1", {"start": v(18.73, -7.88) * mm, "end": v(20.85, -10) * mm});
            skLineSegment(sketch, "E9.6.15.1", {"start": v(18.73, -12.12) * mm, "end": v(20.85, -10) * mm});
            skLineSegment(sketch, "E9.9.15.1", {"start": v(16.6, -10) * mm, "end": v(18.73, -12.12) * mm});
            skLineSegment(sketch, "E9.0.15.2", {"start": v(16.6, -5) * mm, "end": v(18.73, -2.88) * mm});
            skLineSegment(sketch, "E9.3.15.2", {"start": v(18.73, -2.88) * mm, "end": v(20.85, -5) * mm});
            skLineSegment(sketch, "E9.6.15.2", {"start": v(18.73, -7.12) * mm, "end": v(20.85, -5) * mm});
            skLineSegment(sketch, "E9.9.15.2", {"start": v(16.6, -5) * mm, "end": v(18.73, -7.12) * mm});
            skLineSegment(sketch, "E9.0.15.3", {"start": v(16.6, 0) * mm, "end": v(18.73, 2.12) * mm});
            skLineSegment(sketch, "E9.3.15.3", {"start": v(18.73, 2.12) * mm, "end": v(20.85, 0) * mm});
            skLineSegment(sketch, "E9.6.15.3", {"start": v(18.73, -2.12) * mm, "end": v(20.85, 0) * mm});
            skLineSegment(sketch, "E9.9.15.3", {"start": v(16.6, 0) * mm, "end": v(18.73, -2.12) * mm});
            skLineSegment(sketch, "E9.0.15.4", {"start": v(16.6, 5) * mm, "end": v(18.73, 7.12) * mm});
            skLineSegment(sketch, "E9.3.15.4", {"start": v(18.73, 7.12) * mm, "end": v(20.85, 5) * mm});
            skLineSegment(sketch, "E9.6.15.4", {"start": v(18.73, 2.88) * mm, "end": v(20.85, 5) * mm});
            skLineSegment(sketch, "E9.9.15.4", {"start": v(16.6, 5) * mm, "end": v(18.73, 2.88) * mm});
            skLineSegment(sketch, "E9.0.15.5", {"start": v(16.6, 10) * mm, "end": v(18.73, 12.12) * mm});
            skLineSegment(sketch, "E9.3.15.5", {"start": v(18.73, 12.12) * mm, "end": v(20.85, 10) * mm});
            skLineSegment(sketch, "E9.6.15.5", {"start": v(18.73, 7.88) * mm, "end": v(20.85, 10) * mm});
            skLineSegment(sketch, "E9.9.15.5", {"start": v(16.6, 10) * mm, "end": v(18.73, 7.88) * mm});
            skLineSegment(sketch, "E9.0.15.6", {"start": v(16.6, 15) * mm, "end": v(18.73, 17.12) * mm});
            skLineSegment(sketch, "E9.3.15.6", {"start": v(18.73, 17.12) * mm, "end": v(20.85, 15) * mm});
            skLineSegment(sketch, "E9.6.15.6", {"start": v(18.73, 12.88) * mm, "end": v(20.85, 15) * mm});
            skLineSegment(sketch, "E9.9.15.6", {"start": v(16.6, 15) * mm, "end": v(18.73, 12.88) * mm});
            skLineSegment(sketch, "E9.0.16.0", {"start": v(21.6, -15) * mm, "end": v(23.73, -12.88) * mm});
            skLineSegment(sketch, "E9.3.16.0", {"start": v(23.73, -12.88) * mm, "end": v(25.85, -15) * mm});
            skLineSegment(sketch, "E9.6.16.0", {"start": v(23.73, -17.12) * mm, "end": v(25.85, -15) * mm});
            skLineSegment(sketch, "E9.9.16.0", {"start": v(21.6, -15) * mm, "end": v(23.73, -17.12) * mm});
            skLineSegment(sketch, "E9.0.16.1", {"start": v(21.6, -10) * mm, "end": v(23.73, -7.88) * mm});
            skLineSegment(sketch, "E9.3.16.1", {"start": v(23.73, -7.88) * mm, "end": v(25.85, -10) * mm});
            skLineSegment(sketch, "E9.6.16.1", {"start": v(23.73, -12.12) * mm, "end": v(25.85, -10) * mm});
            skLineSegment(sketch, "E9.9.16.1", {"start": v(21.6, -10) * mm, "end": v(23.73, -12.12) * mm});
            skLineSegment(sketch, "E9.0.16.2", {"start": v(21.6, -5) * mm, "end": v(23.73, -2.88) * mm});
            skLineSegment(sketch, "E9.3.16.2", {"start": v(23.73, -2.88) * mm, "end": v(25.85, -5) * mm});
            skLineSegment(sketch, "E9.6.16.2", {"start": v(23.73, -7.12) * mm, "end": v(25.85, -5) * mm});
            skLineSegment(sketch, "E9.9.16.2", {"start": v(21.6, -5) * mm, "end": v(23.73, -7.12) * mm});
            skLineSegment(sketch, "E9.0.16.3", {"start": v(21.6, 0) * mm, "end": v(23.73, 2.12) * mm});
            skLineSegment(sketch, "E9.3.16.3", {"start": v(23.73, 2.12) * mm, "end": v(25.85, 0) * mm});
            skLineSegment(sketch, "E9.6.16.3", {"start": v(23.73, -2.12) * mm, "end": v(25.85, 0) * mm});
            skLineSegment(sketch, "E9.9.16.3", {"start": v(21.6, 0) * mm, "end": v(23.73, -2.12) * mm});
            skLineSegment(sketch, "E9.0.16.4", {"start": v(21.6, 5) * mm, "end": v(23.73, 7.12) * mm});
            skLineSegment(sketch, "E9.3.16.4", {"start": v(23.73, 7.12) * mm, "end": v(25.85, 5) * mm});
            skLineSegment(sketch, "E9.6.16.4", {"start": v(23.73, 2.88) * mm, "end": v(25.85, 5) * mm});
            skLineSegment(sketch, "E9.9.16.4", {"start": v(21.6, 5) * mm, "end": v(23.73, 2.88) * mm});
            skLineSegment(sketch, "E9.0.16.5", {"start": v(21.6, 10) * mm, "end": v(23.73, 12.12) * mm});
            skLineSegment(sketch, "E9.3.16.5", {"start": v(23.73, 12.12) * mm, "end": v(25.85, 10) * mm});
            skLineSegment(sketch, "E9.6.16.5", {"start": v(23.73, 7.88) * mm, "end": v(25.85, 10) * mm});
            skLineSegment(sketch, "E9.9.16.5", {"start": v(21.6, 10) * mm, "end": v(23.73, 7.88) * mm});
            skLineSegment(sketch, "E9.0.16.6", {"start": v(21.6, 15) * mm, "end": v(23.73, 17.12) * mm});
            skLineSegment(sketch, "E9.3.16.6", {"start": v(23.73, 17.12) * mm, "end": v(25.85, 15) * mm});
            skLineSegment(sketch, "E9.6.16.6", {"start": v(23.73, 12.88) * mm, "end": v(25.85, 15) * mm});
            skLineSegment(sketch, "E9.9.16.6", {"start": v(21.6, 15) * mm, "end": v(23.73, 12.88) * mm});
            skLineSegment(sketch, "E9.0.17.0", {"start": v(26.6, -15) * mm, "end": v(28.73, -12.88) * mm});
            skLineSegment(sketch, "E9.3.17.0", {"start": v(28.73, -12.88) * mm, "end": v(30.85, -15) * mm});
            skLineSegment(sketch, "E9.6.17.0", {"start": v(28.73, -17.12) * mm, "end": v(30.85, -15) * mm});
            skLineSegment(sketch, "E9.9.17.0", {"start": v(26.6, -15) * mm, "end": v(28.73, -17.12) * mm});
            skLineSegment(sketch, "E9.0.17.1", {"start": v(26.6, -10) * mm, "end": v(28.73, -7.88) * mm});
            skLineSegment(sketch, "E9.3.17.1", {"start": v(28.73, -7.88) * mm, "end": v(30.85, -10) * mm});
            skLineSegment(sketch, "E9.6.17.1", {"start": v(28.73, -12.12) * mm, "end": v(30.85, -10) * mm});
            skLineSegment(sketch, "E9.9.17.1", {"start": v(26.6, -10) * mm, "end": v(28.73, -12.12) * mm});
            skLineSegment(sketch, "E9.0.17.2", {"start": v(26.6, -5) * mm, "end": v(28.73, -2.88) * mm});
            skLineSegment(sketch, "E9.3.17.2", {"start": v(28.73, -2.88) * mm, "end": v(30.85, -5) * mm});
            skLineSegment(sketch, "E9.6.17.2", {"start": v(28.73, -7.12) * mm, "end": v(30.85, -5) * mm});
            skLineSegment(sketch, "E9.9.17.2", {"start": v(26.6, -5) * mm, "end": v(28.73, -7.12) * mm});
            skLineSegment(sketch, "E9.0.17.3", {"start": v(26.6, 0) * mm, "end": v(28.73, 2.12) * mm});
            skLineSegment(sketch, "E9.3.17.3", {"start": v(28.73, 2.12) * mm, "end": v(30.85, 0) * mm});
            skLineSegment(sketch, "E9.6.17.3", {"start": v(28.73, -2.12) * mm, "end": v(30.85, 0) * mm});
            skLineSegment(sketch, "E9.9.17.3", {"start": v(26.6, 0) * mm, "end": v(28.73, -2.12) * mm});
            skLineSegment(sketch, "E9.0.17.4", {"start": v(26.6, 5) * mm, "end": v(28.73, 7.12) * mm});
            skLineSegment(sketch, "E9.3.17.4", {"start": v(28.73, 7.12) * mm, "end": v(30.85, 5) * mm});
            skLineSegment(sketch, "E9.6.17.4", {"start": v(28.73, 2.88) * mm, "end": v(30.85, 5) * mm});
            skLineSegment(sketch, "E9.9.17.4", {"start": v(26.6, 5) * mm, "end": v(28.73, 2.88) * mm});
            skLineSegment(sketch, "E9.0.17.5", {"start": v(26.6, 10) * mm, "end": v(28.73, 12.12) * mm});
            skLineSegment(sketch, "E9.3.17.5", {"start": v(28.73, 12.12) * mm, "end": v(30.85, 10) * mm});
            skLineSegment(sketch, "E9.6.17.5", {"start": v(28.73, 7.88) * mm, "end": v(30.85, 10) * mm});
            skLineSegment(sketch, "E9.9.17.5", {"start": v(26.6, 10) * mm, "end": v(28.73, 7.88) * mm});
            skLineSegment(sketch, "E9.0.17.6", {"start": v(26.6, 15) * mm, "end": v(28.73, 17.12) * mm});
            skLineSegment(sketch, "E9.3.17.6", {"start": v(28.73, 17.12) * mm, "end": v(30.85, 15) * mm});
            skLineSegment(sketch, "E9.6.17.6", {"start": v(28.73, 12.88) * mm, "end": v(30.85, 15) * mm});
            skLineSegment(sketch, "E9.9.17.6", {"start": v(26.6, 15) * mm, "end": v(28.73, 12.88) * mm});
            skLineSegment(sketch, "E9.0.18.0", {"start": v(31.6, -15) * mm, "end": v(33.73, -12.88) * mm});
            skLineSegment(sketch, "E9.3.18.0", {"start": v(33.73, -12.88) * mm, "end": v(35.85, -15) * mm});
            skLineSegment(sketch, "E9.6.18.0", {"start": v(33.73, -17.12) * mm, "end": v(35.85, -15) * mm});
            skLineSegment(sketch, "E9.9.18.0", {"start": v(31.6, -15) * mm, "end": v(33.73, -17.12) * mm});
            skLineSegment(sketch, "E9.0.18.1", {"start": v(31.6, -10) * mm, "end": v(33.73, -7.88) * mm});
            skLineSegment(sketch, "E9.3.18.1", {"start": v(33.73, -7.88) * mm, "end": v(35.85, -10) * mm});
            skLineSegment(sketch, "E9.6.18.1", {"start": v(33.73, -12.12) * mm, "end": v(35.85, -10) * mm});
            skLineSegment(sketch, "E9.9.18.1", {"start": v(31.6, -10) * mm, "end": v(33.73, -12.12) * mm});
            skLineSegment(sketch, "E9.0.18.2", {"start": v(31.6, -5) * mm, "end": v(33.73, -2.88) * mm});
            skLineSegment(sketch, "E9.3.18.2", {"start": v(33.73, -2.88) * mm, "end": v(35.85, -5) * mm});
            skLineSegment(sketch, "E9.6.18.2", {"start": v(33.73, -7.12) * mm, "end": v(35.85, -5) * mm});
            skLineSegment(sketch, "E9.9.18.2", {"start": v(31.6, -5) * mm, "end": v(33.73, -7.12) * mm});
            skLineSegment(sketch, "E9.0.18.3", {"start": v(31.6, 0) * mm, "end": v(33.73, 2.12) * mm});
            skLineSegment(sketch, "E9.3.18.3", {"start": v(33.73, 2.12) * mm, "end": v(35.85, 0) * mm});
            skLineSegment(sketch, "E9.6.18.3", {"start": v(33.73, -2.12) * mm, "end": v(35.85, 0) * mm});
            skLineSegment(sketch, "E9.9.18.3", {"start": v(31.6, 0) * mm, "end": v(33.73, -2.12) * mm});
            skLineSegment(sketch, "E9.0.18.4", {"start": v(31.6, 5) * mm, "end": v(33.73, 7.12) * mm});
            skLineSegment(sketch, "E9.3.18.4", {"start": v(33.73, 7.12) * mm, "end": v(35.85, 5) * mm});
            skLineSegment(sketch, "E9.6.18.4", {"start": v(33.73, 2.88) * mm, "end": v(35.85, 5) * mm});
            skLineSegment(sketch, "E9.9.18.4", {"start": v(31.6, 5) * mm, "end": v(33.73, 2.88) * mm});
            skLineSegment(sketch, "E9.0.18.5", {"start": v(31.6, 10) * mm, "end": v(33.73, 12.12) * mm});
            skLineSegment(sketch, "E9.3.18.5", {"start": v(33.73, 12.12) * mm, "end": v(35.85, 10) * mm});
            skLineSegment(sketch, "E9.6.18.5", {"start": v(33.73, 7.88) * mm, "end": v(35.85, 10) * mm});
            skLineSegment(sketch, "E9.9.18.5", {"start": v(31.6, 10) * mm, "end": v(33.73, 7.88) * mm});
            skLineSegment(sketch, "E9.0.18.6", {"start": v(31.6, 15) * mm, "end": v(33.73, 17.12) * mm});
            skLineSegment(sketch, "E9.3.18.6", {"start": v(33.73, 17.12) * mm, "end": v(35.85, 15) * mm});
            skLineSegment(sketch, "E9.6.18.6", {"start": v(33.73, 12.88) * mm, "end": v(35.85, 15) * mm});
            skLineSegment(sketch, "E9.9.18.6", {"start": v(31.6, 15) * mm, "end": v(33.73, 12.88) * mm});
            skLineSegment(sketch, "E9.0.19.0", {"start": v(36.6, -15) * mm, "end": v(38.73, -12.88) * mm});
            skLineSegment(sketch, "E9.3.19.0", {"start": v(38.73, -12.88) * mm, "end": v(40.85, -15) * mm});
            skLineSegment(sketch, "E9.6.19.0", {"start": v(38.73, -17.12) * mm, "end": v(40.85, -15) * mm});
            skLineSegment(sketch, "E9.9.19.0", {"start": v(36.6, -15) * mm, "end": v(38.73, -17.12) * mm});
            skLineSegment(sketch, "E9.0.19.1", {"start": v(36.6, -10) * mm, "end": v(38.73, -7.88) * mm});
            skLineSegment(sketch, "E9.3.19.1", {"start": v(38.73, -7.88) * mm, "end": v(40.85, -10) * mm});
            skLineSegment(sketch, "E9.6.19.1", {"start": v(38.73, -12.12) * mm, "end": v(40.85, -10) * mm});
            skLineSegment(sketch, "E9.9.19.1", {"start": v(36.6, -10) * mm, "end": v(38.73, -12.12) * mm});
            skLineSegment(sketch, "E9.0.19.2", {"start": v(36.6, -5) * mm, "end": v(38.73, -2.88) * mm});
            skLineSegment(sketch, "E9.3.19.2", {"start": v(38.73, -2.88) * mm, "end": v(40.85, -5) * mm});
            skLineSegment(sketch, "E9.6.19.2", {"start": v(38.73, -7.12) * mm, "end": v(40.85, -5) * mm});
            skLineSegment(sketch, "E9.9.19.2", {"start": v(36.6, -5) * mm, "end": v(38.73, -7.12) * mm});
            skLineSegment(sketch, "E9.0.19.3", {"start": v(36.6, 0) * mm, "end": v(38.73, 2.12) * mm});
            skLineSegment(sketch, "E9.3.19.3", {"start": v(38.73, 2.12) * mm, "end": v(40.85, 0) * mm});
            skLineSegment(sketch, "E9.6.19.3", {"start": v(38.73, -2.12) * mm, "end": v(40.85, 0) * mm});
            skLineSegment(sketch, "E9.9.19.3", {"start": v(36.6, 0) * mm, "end": v(38.73, -2.12) * mm});
            skLineSegment(sketch, "E9.0.19.4", {"start": v(36.6, 5) * mm, "end": v(38.73, 7.12) * mm});
            skLineSegment(sketch, "E9.3.19.4", {"start": v(38.73, 7.12) * mm, "end": v(40.85, 5) * mm});
            skLineSegment(sketch, "E9.6.19.4", {"start": v(38.73, 2.88) * mm, "end": v(40.85, 5) * mm});
            skLineSegment(sketch, "E9.9.19.4", {"start": v(36.6, 5) * mm, "end": v(38.73, 2.88) * mm});
            skLineSegment(sketch, "E9.0.19.5", {"start": v(36.6, 10) * mm, "end": v(38.73, 12.12) * mm});
            skLineSegment(sketch, "E9.3.19.5", {"start": v(38.73, 12.12) * mm, "end": v(40.85, 10) * mm});
            skLineSegment(sketch, "E9.6.19.5", {"start": v(38.73, 7.88) * mm, "end": v(40.85, 10) * mm});
            skLineSegment(sketch, "E9.9.19.5", {"start": v(36.6, 10) * mm, "end": v(38.73, 7.88) * mm});
            skLineSegment(sketch, "E9.0.19.6", {"start": v(36.6, 15) * mm, "end": v(38.73, 17.12) * mm});
            skLineSegment(sketch, "E9.3.19.6", {"start": v(38.73, 17.12) * mm, "end": v(40.85, 15) * mm});
            skLineSegment(sketch, "E9.6.19.6", {"start": v(38.73, 12.88) * mm, "end": v(40.85, 15) * mm});
            skLineSegment(sketch, "E9.9.19.6", {"start": v(36.6, 15) * mm, "end": v(38.73, 12.88) * mm});
            skLineSegment(sketch, "E9.0.20.0", {"start": v(41.6, -15) * mm, "end": v(43.73, -12.88) * mm});
            skLineSegment(sketch, "E9.3.20.0", {"start": v(43.73, -12.88) * mm, "end": v(45.85, -15) * mm});
            skLineSegment(sketch, "E9.6.20.0", {"start": v(43.73, -17.12) * mm, "end": v(45.85, -15) * mm});
            skLineSegment(sketch, "E9.9.20.0", {"start": v(41.6, -15) * mm, "end": v(43.73, -17.12) * mm});
            skLineSegment(sketch, "E9.0.20.1", {"start": v(41.6, -10) * mm, "end": v(43.73, -7.88) * mm});
            skLineSegment(sketch, "E9.3.20.1", {"start": v(43.73, -7.88) * mm, "end": v(45.85, -10) * mm});
            skLineSegment(sketch, "E9.6.20.1", {"start": v(43.73, -12.12) * mm, "end": v(45.85, -10) * mm});
            skLineSegment(sketch, "E9.9.20.1", {"start": v(41.6, -10) * mm, "end": v(43.73, -12.12) * mm});
            skLineSegment(sketch, "E9.0.20.2", {"start": v(41.6, -5) * mm, "end": v(43.73, -2.88) * mm});
            skLineSegment(sketch, "E9.3.20.2", {"start": v(43.73, -2.88) * mm, "end": v(45.85, -5) * mm});
            skLineSegment(sketch, "E9.6.20.2", {"start": v(43.73, -7.12) * mm, "end": v(45.85, -5) * mm});
            skLineSegment(sketch, "E9.9.20.2", {"start": v(41.6, -5) * mm, "end": v(43.73, -7.12) * mm});
            skLineSegment(sketch, "E9.0.20.3", {"start": v(41.6, 0) * mm, "end": v(43.73, 2.12) * mm});
            skLineSegment(sketch, "E9.3.20.3", {"start": v(43.73, 2.12) * mm, "end": v(45.85, 0) * mm});
            skLineSegment(sketch, "E9.6.20.3", {"start": v(43.73, -2.12) * mm, "end": v(45.85, 0) * mm});
            skLineSegment(sketch, "E9.9.20.3", {"start": v(41.6, 0) * mm, "end": v(43.73, -2.12) * mm});
            skLineSegment(sketch, "E9.0.20.4", {"start": v(41.6, 5) * mm, "end": v(43.73, 7.12) * mm});
            skLineSegment(sketch, "E9.3.20.4", {"start": v(43.73, 7.12) * mm, "end": v(45.85, 5) * mm});
            skLineSegment(sketch, "E9.6.20.4", {"start": v(43.73, 2.88) * mm, "end": v(45.85, 5) * mm});
            skLineSegment(sketch, "E9.9.20.4", {"start": v(41.6, 5) * mm, "end": v(43.73, 2.88) * mm});
            skLineSegment(sketch, "E9.0.20.5", {"start": v(41.6, 10) * mm, "end": v(43.73, 12.12) * mm});
            skLineSegment(sketch, "E9.3.20.5", {"start": v(43.73, 12.12) * mm, "end": v(45.85, 10) * mm});
            skLineSegment(sketch, "E9.6.20.5", {"start": v(43.73, 7.88) * mm, "end": v(45.85, 10) * mm});
            skLineSegment(sketch, "E9.9.20.5", {"start": v(41.6, 10) * mm, "end": v(43.73, 7.88) * mm});
            skLineSegment(sketch, "E9.0.20.6", {"start": v(41.6, 15) * mm, "end": v(43.73, 17.12) * mm});
            skLineSegment(sketch, "E9.3.20.6", {"start": v(43.73, 17.12) * mm, "end": v(45.85, 15) * mm});
            skLineSegment(sketch, "E9.6.20.6", {"start": v(43.73, 12.88) * mm, "end": v(45.85, 15) * mm});
            skLineSegment(sketch, "E9.9.20.6", {"start": v(41.6, 15) * mm, "end": v(43.73, 12.88) * mm});
            skLineSegment(sketch, "E10.0.21.0", {"start": v(46.6, -15) * mm, "end": v(48.73, -12.88) * mm});
            skLineSegment(sketch, "E10.3.21.0", {"start": v(48.73, -12.88) * mm, "end": v(50.85, -15) * mm});
            skLineSegment(sketch, "E10.6.21.0", {"start": v(48.73, -17.12) * mm, "end": v(50.85, -15) * mm});
            skLineSegment(sketch, "E10.9.21.0", {"start": v(46.6, -15) * mm, "end": v(48.73, -17.12) * mm});
            skLineSegment(sketch, "E10.0.21.1", {"start": v(46.6, -10) * mm, "end": v(48.73, -7.88) * mm});
            skLineSegment(sketch, "E10.3.21.1", {"start": v(48.73, -7.88) * mm, "end": v(50.85, -10) * mm});
            skLineSegment(sketch, "E10.6.21.1", {"start": v(48.73, -12.12) * mm, "end": v(50.85, -10) * mm});
            skLineSegment(sketch, "E10.9.21.1", {"start": v(46.6, -10) * mm, "end": v(48.73, -12.12) * mm});
            skLineSegment(sketch, "E10.0.21.2", {"start": v(46.6, -5) * mm, "end": v(48.73, -2.88) * mm});
            skLineSegment(sketch, "E10.3.21.2", {"start": v(48.73, -2.88) * mm, "end": v(50.85, -5) * mm});
            skLineSegment(sketch, "E10.6.21.2", {"start": v(48.73, -7.12) * mm, "end": v(50.85, -5) * mm});
            skLineSegment(sketch, "E10.9.21.2", {"start": v(46.6, -5) * mm, "end": v(48.73, -7.12) * mm});
            skLineSegment(sketch, "E10.0.21.3", {"start": v(46.6, 0) * mm, "end": v(48.73, 2.12) * mm});
            skLineSegment(sketch, "E10.3.21.3", {"start": v(48.73, 2.12) * mm, "end": v(50.85, 0) * mm});
            skLineSegment(sketch, "E10.6.21.3", {"start": v(48.73, -2.12) * mm, "end": v(50.85, 0) * mm});
            skLineSegment(sketch, "E10.9.21.3", {"start": v(46.6, 0) * mm, "end": v(48.73, -2.12) * mm});
            skLineSegment(sketch, "E10.0.21.4", {"start": v(46.6, 5) * mm, "end": v(48.73, 7.12) * mm});
            skLineSegment(sketch, "E10.3.21.4", {"start": v(48.73, 7.12) * mm, "end": v(50.85, 5) * mm});
            skLineSegment(sketch, "E10.6.21.4", {"start": v(48.73, 2.88) * mm, "end": v(50.85, 5) * mm});
            skLineSegment(sketch, "E10.9.21.4", {"start": v(46.6, 5) * mm, "end": v(48.73, 2.88) * mm});
            skLineSegment(sketch, "E10.0.21.5", {"start": v(46.6, 10) * mm, "end": v(48.73, 12.12) * mm});
            skLineSegment(sketch, "E10.3.21.5", {"start": v(48.73, 12.12) * mm, "end": v(50.85, 10) * mm});
            skLineSegment(sketch, "E10.6.21.5", {"start": v(48.73, 7.88) * mm, "end": v(50.85, 10) * mm});
            skLineSegment(sketch, "E10.9.21.5", {"start": v(46.6, 10) * mm, "end": v(48.73, 7.88) * mm});
            skLineSegment(sketch, "E10.0.21.6", {"start": v(46.6, 15) * mm, "end": v(48.73, 17.12) * mm});
            skLineSegment(sketch, "E10.3.21.6", {"start": v(48.73, 17.12) * mm, "end": v(50.85, 15) * mm});
            skLineSegment(sketch, "E10.6.21.6", {"start": v(48.73, 12.88) * mm, "end": v(50.85, 15) * mm});
            skLineSegment(sketch, "E10.9.21.6", {"start": v(46.6, 15) * mm, "end": v(48.73, 12.88) * mm});
            skLineSegment(sketch, "E10.0.22.0", {"start": v(51.6, -15) * mm, "end": v(53.73, -12.88) * mm});
            skLineSegment(sketch, "E10.3.22.0", {"start": v(53.73, -12.88) * mm, "end": v(55.85, -15) * mm});
            skLineSegment(sketch, "E10.6.22.0", {"start": v(53.73, -17.12) * mm, "end": v(55.85, -15) * mm});
            skLineSegment(sketch, "E10.9.22.0", {"start": v(51.6, -15) * mm, "end": v(53.73, -17.12) * mm});
            skLineSegment(sketch, "E10.0.22.1", {"start": v(51.6, -10) * mm, "end": v(53.73, -7.88) * mm});
            skLineSegment(sketch, "E10.3.22.1", {"start": v(53.73, -7.88) * mm, "end": v(55.85, -10) * mm});
            skLineSegment(sketch, "E10.6.22.1", {"start": v(53.73, -12.12) * mm, "end": v(55.85, -10) * mm});
            skLineSegment(sketch, "E10.9.22.1", {"start": v(51.6, -10) * mm, "end": v(53.73, -12.12) * mm});
            skLineSegment(sketch, "E10.0.22.2", {"start": v(51.6, -5) * mm, "end": v(53.73, -2.88) * mm});
            skLineSegment(sketch, "E10.3.22.2", {"start": v(53.73, -2.88) * mm, "end": v(55.85, -5) * mm});
            skLineSegment(sketch, "E10.6.22.2", {"start": v(53.73, -7.12) * mm, "end": v(55.85, -5) * mm});
            skLineSegment(sketch, "E10.9.22.2", {"start": v(51.6, -5) * mm, "end": v(53.73, -7.12) * mm});
            skLineSegment(sketch, "E10.0.22.3", {"start": v(51.6, 0) * mm, "end": v(53.73, 2.12) * mm});
            skLineSegment(sketch, "E10.3.22.3", {"start": v(53.73, 2.12) * mm, "end": v(55.85, 0) * mm});
            skLineSegment(sketch, "E10.6.22.3", {"start": v(53.73, -2.12) * mm, "end": v(55.85, 0) * mm});
            skLineSegment(sketch, "E10.9.22.3", {"start": v(51.6, 0) * mm, "end": v(53.73, -2.12) * mm});
            skLineSegment(sketch, "E10.0.22.4", {"start": v(51.6, 5) * mm, "end": v(53.73, 7.12) * mm});
            skLineSegment(sketch, "E10.3.22.4", {"start": v(53.73, 7.12) * mm, "end": v(55.85, 5) * mm});
            skLineSegment(sketch, "E10.6.22.4", {"start": v(53.73, 2.88) * mm, "end": v(55.85, 5) * mm});
            skLineSegment(sketch, "E10.9.22.4", {"start": v(51.6, 5) * mm, "end": v(53.73, 2.88) * mm});
            skLineSegment(sketch, "E10.0.22.5", {"start": v(51.6, 10) * mm, "end": v(53.73, 12.12) * mm});
            skLineSegment(sketch, "E10.3.22.5", {"start": v(53.73, 12.12) * mm, "end": v(55.85, 10) * mm});
            skLineSegment(sketch, "E10.6.22.5", {"start": v(53.73, 7.88) * mm, "end": v(55.85, 10) * mm});
            skLineSegment(sketch, "E10.9.22.5", {"start": v(51.6, 10) * mm, "end": v(53.73, 7.88) * mm});
            skLineSegment(sketch, "E10.0.22.6", {"start": v(51.6, 15) * mm, "end": v(53.73, 17.12) * mm});
            skLineSegment(sketch, "E10.3.22.6", {"start": v(53.73, 17.12) * mm, "end": v(55.85, 15) * mm});
            skLineSegment(sketch, "E10.6.22.6", {"start": v(53.73, 12.88) * mm, "end": v(55.85, 15) * mm});
            skLineSegment(sketch, "E10.9.22.6", {"start": v(51.6, 15) * mm, "end": v(53.73, 12.88) * mm});
            skLineSegment(sketch, "E10.0.23.0", {"start": v(56.6, -15) * mm, "end": v(58.73, -12.88) * mm});
            skLineSegment(sketch, "E10.3.23.0", {"start": v(58.73, -12.88) * mm, "end": v(60.85, -15) * mm});
            skLineSegment(sketch, "E10.6.23.0", {"start": v(58.73, -17.12) * mm, "end": v(60.85, -15) * mm});
            skLineSegment(sketch, "E10.9.23.0", {"start": v(56.6, -15) * mm, "end": v(58.73, -17.12) * mm});
            skLineSegment(sketch, "E10.0.23.1", {"start": v(56.6, -10) * mm, "end": v(58.73, -7.88) * mm});
            skLineSegment(sketch, "E10.3.23.1", {"start": v(58.73, -7.88) * mm, "end": v(60.85, -10) * mm});
            skLineSegment(sketch, "E10.6.23.1", {"start": v(58.73, -12.12) * mm, "end": v(60.85, -10) * mm});
            skLineSegment(sketch, "E10.9.23.1", {"start": v(56.6, -10) * mm, "end": v(58.73, -12.12) * mm});
            skLineSegment(sketch, "E10.0.23.2", {"start": v(56.6, -5) * mm, "end": v(58.73, -2.88) * mm});
            skLineSegment(sketch, "E10.3.23.2", {"start": v(58.73, -2.88) * mm, "end": v(60.85, -5) * mm});
            skLineSegment(sketch, "E10.6.23.2", {"start": v(58.73, -7.12) * mm, "end": v(60.85, -5) * mm});
            skLineSegment(sketch, "E10.9.23.2", {"start": v(56.6, -5) * mm, "end": v(58.73, -7.12) * mm});
            skLineSegment(sketch, "E10.0.23.3", {"start": v(56.6, 0) * mm, "end": v(58.73, 2.12) * mm});
            skLineSegment(sketch, "E10.3.23.3", {"start": v(58.73, 2.12) * mm, "end": v(60.85, 0) * mm});
            skLineSegment(sketch, "E10.6.23.3", {"start": v(58.73, -2.12) * mm, "end": v(60.85, 0) * mm});
            skLineSegment(sketch, "E10.9.23.3", {"start": v(56.6, 0) * mm, "end": v(58.73, -2.12) * mm});
            skLineSegment(sketch, "E10.0.23.4", {"start": v(56.6, 5) * mm, "end": v(58.73, 7.12) * mm});
            skLineSegment(sketch, "E10.3.23.4", {"start": v(58.73, 7.12) * mm, "end": v(60.85, 5) * mm});
            skLineSegment(sketch, "E10.6.23.4", {"start": v(58.73, 2.88) * mm, "end": v(60.85, 5) * mm});
            skLineSegment(sketch, "E10.9.23.4", {"start": v(56.6, 5) * mm, "end": v(58.73, 2.88) * mm});
            skLineSegment(sketch, "E10.0.23.5", {"start": v(56.6, 10) * mm, "end": v(58.73, 12.12) * mm});
            skLineSegment(sketch, "E10.3.23.5", {"start": v(58.73, 12.12) * mm, "end": v(60.85, 10) * mm});
            skLineSegment(sketch, "E10.6.23.5", {"start": v(58.73, 7.88) * mm, "end": v(60.85, 10) * mm});
            skLineSegment(sketch, "E10.9.23.5", {"start": v(56.6, 10) * mm, "end": v(58.73, 7.88) * mm});
            skLineSegment(sketch, "E10.0.23.6", {"start": v(56.6, 15) * mm, "end": v(58.73, 17.12) * mm});
            skLineSegment(sketch, "E10.3.23.6", {"start": v(58.73, 17.12) * mm, "end": v(60.85, 15) * mm});
            skLineSegment(sketch, "E10.6.23.6", {"start": v(58.73, 12.88) * mm, "end": v(60.85, 15) * mm});
            skLineSegment(sketch, "E10.9.23.6", {"start": v(56.6, 15) * mm, "end": v(58.73, 12.88) * mm});
            skSolve(sketch);
        }
        {
            var Q0;
            {var subQ71=sQuery(id+"F0.wireOp",EDGE,"E0.top");Q0=makeQuery(id+"F0.imprint","IMPRINT",FACE,{"disambiguationData":[TD([[makeQuery(id+"F0.imprint","IMPRINT",EDGE,{"derivedFrom":subQ71}),-1.0]])]});}
            extrude(context, id + "F1", {"entities" : qUnion([Q0]), "depth" : 2.5 * mm, "offsetDistance" : 25 * mm});
        }
    });
